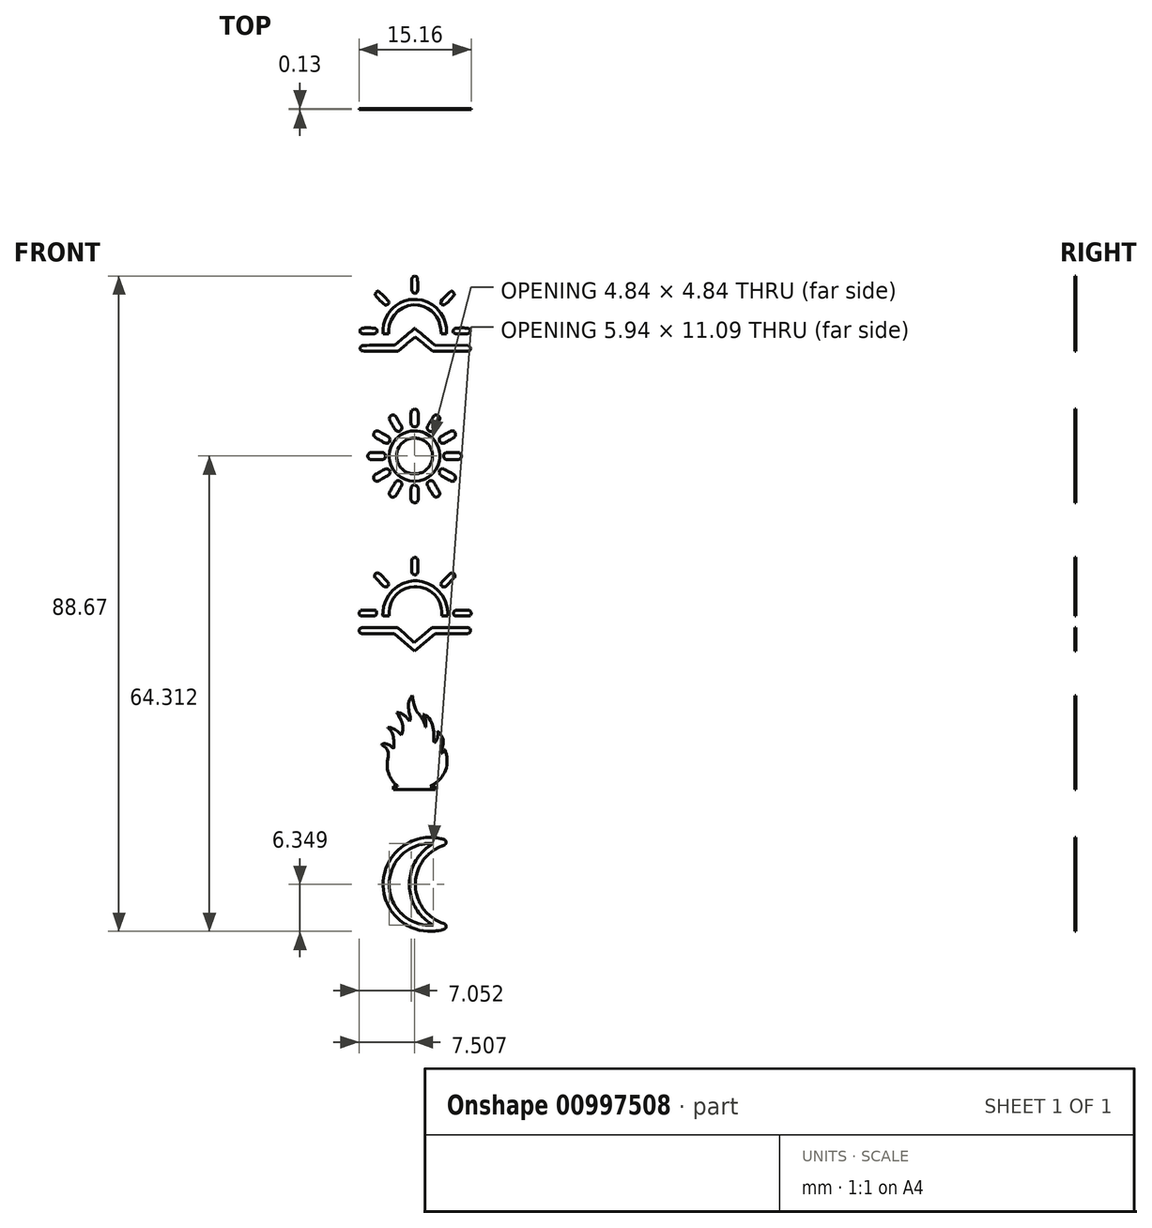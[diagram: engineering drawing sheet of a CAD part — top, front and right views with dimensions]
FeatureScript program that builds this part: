
annotation { "Feature Type Name" : "Feature", "Feature Type Description" : "" }
export const myFeature = defineFeature(function(context is Context, id is Id, definition is map)
    precondition{}
    {
        {
            var Q0;
            Q0=qCreatedBy(makeId("Front.planeOp"),FACE);
            var sketch = newSketch(context, id + "F0", { "sketchPlane" : qUnion([Q0])});
            skLineSegment(sketch, "E0", {"start": v(10.8, 42.86) * mm, "end": v(-8.25, 61.91) * mm});
            skLineSegment(sketch, "E1", {"start": v(-8.26, 61.91) * mm, "end": v(-10.8, 61.91) * mm});
            skLineSegment(sketch, "E2", {"start": v(-10.8, 61.91) * mm, "end": v(-10.8, -61.91) * mm});
            skLineSegment(sketch, "E3", {"start": v(-8.26, -61.91) * mm, "end": v(-10.8, -61.91) * mm});
            skLineSegment(sketch, "E4", {"start": v(-8.26, -61.91) * mm, "end": v(10.8, -42.86) * mm});
            skLineSegment(sketch, "E5", {"start": v(10.8, 42.86) * mm, "end": v(10.8, -42.86) * mm});
            skSolve(sketch);
        }
        {
            var Q0;
            Q0=makeQuery(id+"F0.imprint","IMPRINT",FACE,{"disambiguationData":[TD([[makeQuery(id+"F0.imprint","IMPRINT",EDGE,{"derivedFrom":sQuery(id+"F0.wireOp",EDGE,"E0")}),1.0]])]});
            var sketch = newSketch(context, id + "F1", { "sketchPlane" : qUnion([Q0])});
            skLineSegment(sketch, "E6", {"start": v(4.23, 3.04) * mm, "end": v(5.34, 4.15) * mm});
            skLineSegment(sketch, "E7", {"start": v(5.34, 4.15) * mm, "end": v(5.36, 4.18) * mm});
            skLineSegment(sketch, "E8", {"start": v(5.36, 4.18) * mm, "end": v(5.43, 4.28) * mm});
            skLineSegment(sketch, "E9", {"start": v(5.43, 4.28) * mm, "end": v(5.46, 4.43) * mm});
            skLineSegment(sketch, "E10", {"start": v(5.46, 4.43) * mm, "end": v(5.43, 4.57) * mm});
            skLineSegment(sketch, "E11", {"start": v(5.43, 4.57) * mm, "end": v(5.36, 4.68) * mm});
            skLineSegment(sketch, "E12", {"start": v(5.36, 4.68) * mm, "end": v(5.34, 4.7) * mm});
            skLineSegment(sketch, "E13", {"start": v(5.34, 4.7) * mm, "end": v(5.3, 4.73) * mm});
            skLineSegment(sketch, "E14", {"start": v(5.3, 4.73) * mm, "end": v(5.2, 4.8) * mm});
            skLineSegment(sketch, "E15", {"start": v(5.2, 4.8) * mm, "end": v(5.06, 4.82) * mm});
            skLineSegment(sketch, "E16", {"start": v(5.06, 4.82) * mm, "end": v(4.91, 4.8) * mm});
            skLineSegment(sketch, "E17", {"start": v(4.91, 4.8) * mm, "end": v(4.8, 4.73) * mm});
            skLineSegment(sketch, "E18", {"start": v(4.8, 4.73) * mm, "end": v(4.78, 4.7) * mm});
            skLineSegment(sketch, "E19", {"start": v(4.78, 4.7) * mm, "end": v(3.67, 3.6) * mm});
            skLineSegment(sketch, "E20", {"start": v(3.67, 3.6) * mm, "end": v(3.64, 3.57) * mm});
            skLineSegment(sketch, "E21", {"start": v(3.64, 3.57) * mm, "end": v(3.58, 3.46) * mm});
            skLineSegment(sketch, "E22", {"start": v(3.58, 3.46) * mm, "end": v(3.55, 3.32) * mm});
            skLineSegment(sketch, "E23", {"start": v(3.55, 3.32) * mm, "end": v(3.58, 3.17) * mm});
            skLineSegment(sketch, "E24", {"start": v(3.58, 3.17) * mm, "end": v(3.64, 3.07) * mm});
            skLineSegment(sketch, "E25", {"start": v(3.64, 3.07) * mm, "end": v(3.67, 3.04) * mm});
            skLineSegment(sketch, "E26", {"start": v(3.67, 3.04) * mm, "end": v(3.7, 3) * mm});
            skLineSegment(sketch, "E27", {"start": v(3.7, 3) * mm, "end": v(3.81, 2.95) * mm});
            skLineSegment(sketch, "E28", {"start": v(3.81, 2.95) * mm, "end": v(3.98, 2.92) * mm});
            skLineSegment(sketch, "E29", {"start": v(3.98, 2.92) * mm, "end": v(4.13, 2.95) * mm});
            skLineSegment(sketch, "E30", {"start": v(4.13, 2.95) * mm, "end": v(4.21, 3.01) * mm});
            skLineSegment(sketch, "E31", {"start": v(4.21, 3.01) * mm, "end": v(4.23, 3.04) * mm});
            skLineSegment(sketch, "E32", {"start": v(0.02, 4.54) * mm, "end": v(0.06, 4.54) * mm});
            skLineSegment(sketch, "E33", {"start": v(0.06, 4.54) * mm, "end": v(0.18, 4.57) * mm});
            skLineSegment(sketch, "E34", {"start": v(0.18, 4.57) * mm, "end": v(0.31, 4.65) * mm});
            skLineSegment(sketch, "E35", {"start": v(0.31, 4.65) * mm, "end": v(0.4, 4.78) * mm});
            skLineSegment(sketch, "E36", {"start": v(0.4, 4.78) * mm, "end": v(0.42, 4.9) * mm});
            skLineSegment(sketch, "E37", {"start": v(0.42, 4.9) * mm, "end": v(0.42, 4.94) * mm});
            skLineSegment(sketch, "E38", {"start": v(0.42, 4.94) * mm, "end": v(0.42, 6.53) * mm});
            skLineSegment(sketch, "E39", {"start": v(0.42, 6.53) * mm, "end": v(0.42, 6.57) * mm});
            skLineSegment(sketch, "E40", {"start": v(0.42, 6.57) * mm, "end": v(0.4, 6.69) * mm});
            skLineSegment(sketch, "E41", {"start": v(0.4, 6.69) * mm, "end": v(0.31, 6.82) * mm});
            skLineSegment(sketch, "E42", {"start": v(0.31, 6.82) * mm, "end": v(0.19, 6.9) * mm});
            skLineSegment(sketch, "E43", {"start": v(0.19, 6.9) * mm, "end": v(0.06, 6.93) * mm});
            skLineSegment(sketch, "E44", {"start": v(0.06, 6.93) * mm, "end": v(0.02, 6.93) * mm});
            skLineSegment(sketch, "E45", {"start": v(0.02, 6.93) * mm, "end": v(0, 6.93) * mm});
            skLineSegment(sketch, "E46", {"start": v(0, 6.93) * mm, "end": v(-0.1, 6.9) * mm});
            skLineSegment(sketch, "E47", {"start": v(-0.1, 6.9) * mm, "end": v(-0.24, 6.82) * mm});
            skLineSegment(sketch, "E48", {"start": v(-0.24, 6.82) * mm, "end": v(-0.34, 6.7) * mm});
            skLineSegment(sketch, "E49", {"start": v(-0.34, 6.7) * mm, "end": v(-0.38, 6.57) * mm});
            skLineSegment(sketch, "E50", {"start": v(-0.38, 6.57) * mm, "end": v(-0.38, 6.53) * mm});
            skLineSegment(sketch, "E51", {"start": v(-0.38, 6.53) * mm, "end": v(-0.38, 4.94) * mm});
            skLineSegment(sketch, "E52", {"start": v(-0.38, 4.94) * mm, "end": v(-0.38, 4.9) * mm});
            skLineSegment(sketch, "E53", {"start": v(-0.38, 4.9) * mm, "end": v(-0.34, 4.78) * mm});
            skLineSegment(sketch, "E54", {"start": v(-0.34, 4.78) * mm, "end": v(-0.24, 4.65) * mm});
            skLineSegment(sketch, "E55", {"start": v(-0.24, 4.65) * mm, "end": v(-0.1, 4.57) * mm});
            skLineSegment(sketch, "E56", {"start": v(-0.1, 4.57) * mm, "end": v(-0.01, 4.54) * mm});
            skLineSegment(sketch, "E57", {"start": v(-0.01, 4.54) * mm, "end": v(0.02, 4.54) * mm});
            skLineSegment(sketch, "E58", {"start": v(5.26, -0.61) * mm, "end": v(5.26, -0.65) * mm});
            skLineSegment(sketch, "E59", {"start": v(5.26, -0.65) * mm, "end": v(5.29, -0.78) * mm});
            skLineSegment(sketch, "E60", {"start": v(5.29, -0.78) * mm, "end": v(5.37, -0.9) * mm});
            skLineSegment(sketch, "E61", {"start": v(5.37, -0.9) * mm, "end": v(5.5, -0.98) * mm});
            skLineSegment(sketch, "E62", {"start": v(5.5, -0.98) * mm, "end": v(5.62, -1.01) * mm});
            skLineSegment(sketch, "E63", {"start": v(5.62, -1.01) * mm, "end": v(5.66, -1.01) * mm});
            skLineSegment(sketch, "E64", {"start": v(5.66, -1.01) * mm, "end": v(7.24, -1.01) * mm});
            skLineSegment(sketch, "E65", {"start": v(7.24, -1.01) * mm, "end": v(7.28, -1.01) * mm});
            skLineSegment(sketch, "E66", {"start": v(7.28, -1.01) * mm, "end": v(7.4, -0.98) * mm});
            skLineSegment(sketch, "E67", {"start": v(7.4, -0.98) * mm, "end": v(7.53, -0.9) * mm});
            skLineSegment(sketch, "E68", {"start": v(7.53, -0.9) * mm, "end": v(7.61, -0.78) * mm});
            skLineSegment(sketch, "E69", {"start": v(7.61, -0.78) * mm, "end": v(7.64, -0.65) * mm});
            skLineSegment(sketch, "E70", {"start": v(7.64, -0.65) * mm, "end": v(7.64, -0.61) * mm});
            skLineSegment(sketch, "E71", {"start": v(7.64, -0.61) * mm, "end": v(7.64, -0.57) * mm});
            skLineSegment(sketch, "E72", {"start": v(7.64, -0.57) * mm, "end": v(7.61, -0.45) * mm});
            skLineSegment(sketch, "E73", {"start": v(7.61, -0.45) * mm, "end": v(7.53, -0.32) * mm});
            skLineSegment(sketch, "E74", {"start": v(7.53, -0.32) * mm, "end": v(7.4, -0.24) * mm});
            skLineSegment(sketch, "E75", {"start": v(7.4, -0.24) * mm, "end": v(7.28, -0.21) * mm});
            skLineSegment(sketch, "E76", {"start": v(7.28, -0.21) * mm, "end": v(7.24, -0.21) * mm});
            skLineSegment(sketch, "E77", {"start": v(7.24, -0.21) * mm, "end": v(5.66, -0.21) * mm});
            skLineSegment(sketch, "E78", {"start": v(5.66, -0.21) * mm, "end": v(5.62, -0.21) * mm});
            skLineSegment(sketch, "E79", {"start": v(5.62, -0.21) * mm, "end": v(5.5, -0.25) * mm});
            skLineSegment(sketch, "E80", {"start": v(5.5, -0.25) * mm, "end": v(5.37, -0.35) * mm});
            skLineSegment(sketch, "E81", {"start": v(5.37, -0.35) * mm, "end": v(5.29, -0.48) * mm});
            skLineSegment(sketch, "E82", {"start": v(5.29, -0.48) * mm, "end": v(5.26, -0.58) * mm});
            skLineSegment(sketch, "E83", {"start": v(5.26, -0.58) * mm, "end": v(5.26, -0.61) * mm});
            skLineSegment(sketch, "E84", {"start": v(-4.18, 3.04) * mm, "end": v(-4.16, 3.01) * mm});
            skLineSegment(sketch, "E85", {"start": v(-4.16, 3.01) * mm, "end": v(-4.05, 2.95) * mm});
            skLineSegment(sketch, "E86", {"start": v(-4.05, 2.95) * mm, "end": v(-3.9, 2.92) * mm});
            skLineSegment(sketch, "E87", {"start": v(-3.9, 2.92) * mm, "end": v(-3.76, 2.95) * mm});
            skLineSegment(sketch, "E88", {"start": v(-3.76, 2.95) * mm, "end": v(-3.66, 3.01) * mm});
            skLineSegment(sketch, "E89", {"start": v(-3.66, 3.01) * mm, "end": v(-3.63, 3.04) * mm});
            skLineSegment(sketch, "E90", {"start": v(-3.63, 3.04) * mm, "end": v(-3.6, 3.07) * mm});
            skLineSegment(sketch, "E91", {"start": v(-3.6, 3.07) * mm, "end": v(-3.54, 3.17) * mm});
            skLineSegment(sketch, "E92", {"start": v(-3.54, 3.17) * mm, "end": v(-3.51, 3.32) * mm});
            skLineSegment(sketch, "E93", {"start": v(-3.51, 3.32) * mm, "end": v(-3.54, 3.46) * mm});
            skLineSegment(sketch, "E94", {"start": v(-3.54, 3.46) * mm, "end": v(-3.6, 3.57) * mm});
            skLineSegment(sketch, "E95", {"start": v(-3.6, 3.57) * mm, "end": v(-3.63, 3.6) * mm});
            skLineSegment(sketch, "E96", {"start": v(-3.63, 3.6) * mm, "end": v(-4.74, 4.7) * mm});
            skLineSegment(sketch, "E97", {"start": v(-4.74, 4.7) * mm, "end": v(-4.77, 4.73) * mm});
            skLineSegment(sketch, "E98", {"start": v(-4.77, 4.73) * mm, "end": v(-4.87, 4.8) * mm});
            skLineSegment(sketch, "E99", {"start": v(-4.87, 4.8) * mm, "end": v(-5.02, 4.82) * mm});
            skLineSegment(sketch, "E100", {"start": v(-5.02, 4.82) * mm, "end": v(-5.17, 4.8) * mm});
            skLineSegment(sketch, "E101", {"start": v(-5.17, 4.8) * mm, "end": v(-5.27, 4.73) * mm});
            skLineSegment(sketch, "E102", {"start": v(-5.27, 4.73) * mm, "end": v(-5.3, 4.7) * mm});
            skLineSegment(sketch, "E103", {"start": v(-5.3, 4.7) * mm, "end": v(-5.32, 4.68) * mm});
            skLineSegment(sketch, "E104", {"start": v(-5.32, 4.68) * mm, "end": v(-5.39, 4.57) * mm});
            skLineSegment(sketch, "E105", {"start": v(-5.39, 4.57) * mm, "end": v(-5.41, 4.43) * mm});
            skLineSegment(sketch, "E106", {"start": v(-5.41, 4.43) * mm, "end": v(-5.39, 4.28) * mm});
            skLineSegment(sketch, "E107", {"start": v(-5.39, 4.28) * mm, "end": v(-5.32, 4.18) * mm});
            skLineSegment(sketch, "E108", {"start": v(-5.32, 4.18) * mm, "end": v(-5.3, 4.15) * mm});
            skLineSegment(sketch, "E109", {"start": v(-5.3, 4.15) * mm, "end": v(-4.18, 3.04) * mm});
            skLineSegment(sketch, "E110", {"start": v(-7.12, -1) * mm, "end": v(-5.54, -1) * mm});
            skLineSegment(sketch, "E111", {"start": v(-5.54, -1) * mm, "end": v(-5.5, -1) * mm});
            skLineSegment(sketch, "E112", {"start": v(-5.5, -1) * mm, "end": v(-5.38, -0.98) * mm});
            skLineSegment(sketch, "E113", {"start": v(-5.38, -0.98) * mm, "end": v(-5.25, -0.9) * mm});
            skLineSegment(sketch, "E114", {"start": v(-5.25, -0.9) * mm, "end": v(-5.17, -0.77) * mm});
            skLineSegment(sketch, "E115", {"start": v(-5.17, -0.77) * mm, "end": v(-5.14, -0.65) * mm});
            skLineSegment(sketch, "E116", {"start": v(-5.14, -0.65) * mm, "end": v(-5.14, -0.6) * mm});
            skLineSegment(sketch, "E117", {"start": v(-5.14, -0.6) * mm, "end": v(-5.14, -0.57) * mm});
            skLineSegment(sketch, "E118", {"start": v(-5.14, -0.57) * mm, "end": v(-5.17, -0.45) * mm});
            skLineSegment(sketch, "E119", {"start": v(-5.17, -0.45) * mm, "end": v(-5.25, -0.32) * mm});
            skLineSegment(sketch, "E120", {"start": v(-5.25, -0.32) * mm, "end": v(-5.37, -0.24) * mm});
            skLineSegment(sketch, "E121", {"start": v(-5.37, -0.24) * mm, "end": v(-5.5, -0.21) * mm});
            skLineSegment(sketch, "E122", {"start": v(-5.5, -0.21) * mm, "end": v(-5.54, -0.21) * mm});
            skLineSegment(sketch, "E123", {"start": v(-5.54, -0.21) * mm, "end": v(-7.12, -0.21) * mm});
            skLineSegment(sketch, "E124", {"start": v(-7.12, -0.21) * mm, "end": v(-7.16, -0.21) * mm});
            skLineSegment(sketch, "E125", {"start": v(-7.16, -0.21) * mm, "end": v(-7.28, -0.25) * mm});
            skLineSegment(sketch, "E126", {"start": v(-7.28, -0.25) * mm, "end": v(-7.41, -0.35) * mm});
            skLineSegment(sketch, "E127", {"start": v(-7.41, -0.35) * mm, "end": v(-7.5, -0.48) * mm});
            skLineSegment(sketch, "E128", {"start": v(-7.5, -0.48) * mm, "end": v(-7.52, -0.58) * mm});
            skLineSegment(sketch, "E129", {"start": v(-7.52, -0.58) * mm, "end": v(-7.52, -0.6) * mm});
            skLineSegment(sketch, "E130", {"start": v(-7.52, -0.6) * mm, "end": v(-7.52, -0.65) * mm});
            skLineSegment(sketch, "E131", {"start": v(-7.52, -0.65) * mm, "end": v(-7.49, -0.77) * mm});
            skLineSegment(sketch, "E132", {"start": v(-7.49, -0.77) * mm, "end": v(-7.4, -0.9) * mm});
            skLineSegment(sketch, "E133", {"start": v(-7.4, -0.9) * mm, "end": v(-7.28, -0.98) * mm});
            skLineSegment(sketch, "E134", {"start": v(-7.28, -0.98) * mm, "end": v(-7.16, -1) * mm});
            skLineSegment(sketch, "E135", {"start": v(-7.16, -1) * mm, "end": v(-7.12, -1) * mm});
            skLineSegment(sketch, "E136", {"start": v(7.16, -2.6) * mm, "end": v(2.32, -2.6) * mm});
            skLineSegment(sketch, "E137", {"start": v(2.32, -2.6) * mm, "end": v(1.37, -3.39) * mm});
            skLineSegment(sketch, "E138", {"start": v(1.37, -3.39) * mm, "end": v(-0.06, -4.58) * mm});
            skLineSegment(sketch, "E139", {"start": v(-0.06, -4.58) * mm, "end": v(-1.33, -3.39) * mm});
            skLineSegment(sketch, "E140", {"start": v(-1.33, -3.39) * mm, "end": v(-2.28, -2.6) * mm});
            skLineSegment(sketch, "E141", {"start": v(-2.28, -2.6) * mm, "end": v(-7.12, -2.6) * mm});
            skLineSegment(sketch, "E142", {"start": v(-7.12, -2.6) * mm, "end": v(-7.15, -2.6) * mm});
            skLineSegment(sketch, "E143", {"start": v(-7.15, -2.6) * mm, "end": v(-7.25, -2.62) * mm});
            skLineSegment(sketch, "E144", {"start": v(-7.25, -2.62) * mm, "end": v(-7.38, -2.7) * mm});
            skLineSegment(sketch, "E145", {"start": v(-7.38, -2.7) * mm, "end": v(-7.48, -2.83) * mm});
            skLineSegment(sketch, "E146", {"start": v(-7.48, -2.83) * mm, "end": v(-7.52, -2.95) * mm});
            skLineSegment(sketch, "E147", {"start": v(-7.52, -2.95) * mm, "end": v(-7.52, -3) * mm});
            skLineSegment(sketch, "E148", {"start": v(-7.52, -3) * mm, "end": v(-7.52, -3.04) * mm});
            skLineSegment(sketch, "E149", {"start": v(-7.52, -3.04) * mm, "end": v(-7.48, -3.16) * mm});
            skLineSegment(sketch, "E150", {"start": v(-7.48, -3.16) * mm, "end": v(-7.38, -3.28) * mm});
            skLineSegment(sketch, "E151", {"start": v(-7.38, -3.28) * mm, "end": v(-7.25, -3.36) * mm});
            skLineSegment(sketch, "E152", {"start": v(-7.25, -3.36) * mm, "end": v(-7.15, -3.4) * mm});
            skLineSegment(sketch, "E153", {"start": v(-7.15, -3.4) * mm, "end": v(-7.12, -3.4) * mm});
            skLineSegment(sketch, "E154", {"start": v(-7.12, -3.4) * mm, "end": v(-2.76, -3.4) * mm});
            skLineSegment(sketch, "E155", {"start": v(-2.76, -3.4) * mm, "end": v(0.02, -5.77) * mm});
            skLineSegment(sketch, "E156", {"start": v(0.02, -5.77) * mm, "end": v(2.8, -3.4) * mm});
            skLineSegment(sketch, "E157", {"start": v(2.8, -3.4) * mm, "end": v(7.16, -3.4) * mm});
            skLineSegment(sketch, "E158", {"start": v(7.16, -3.4) * mm, "end": v(7.2, -3.4) * mm});
            skLineSegment(sketch, "E159", {"start": v(7.2, -3.4) * mm, "end": v(7.32, -3.36) * mm});
            skLineSegment(sketch, "E160", {"start": v(7.32, -3.36) * mm, "end": v(7.45, -3.28) * mm});
            skLineSegment(sketch, "E161", {"start": v(7.45, -3.28) * mm, "end": v(7.53, -3.16) * mm});
            skLineSegment(sketch, "E162", {"start": v(7.53, -3.16) * mm, "end": v(7.56, -3.04) * mm});
            skLineSegment(sketch, "E163", {"start": v(7.56, -3.04) * mm, "end": v(7.56, -3) * mm});
            skLineSegment(sketch, "E164", {"start": v(7.56, -3) * mm, "end": v(7.56, -2.95) * mm});
            skLineSegment(sketch, "E165", {"start": v(7.56, -2.95) * mm, "end": v(7.53, -2.83) * mm});
            skLineSegment(sketch, "E166", {"start": v(7.53, -2.83) * mm, "end": v(7.45, -2.7) * mm});
            skLineSegment(sketch, "E167", {"start": v(7.45, -2.7) * mm, "end": v(7.32, -2.62) * mm});
            skLineSegment(sketch, "E168", {"start": v(7.32, -2.62) * mm, "end": v(7.2, -2.6) * mm});
            skLineSegment(sketch, "E169", {"start": v(7.2, -2.6) * mm, "end": v(7.16, -2.6) * mm});
            skLineSegment(sketch, "E170", {"start": v(-4.26, -1) * mm, "end": v(-3.47, -1) * mm});
            skLineSegment(sketch, "E171", {"start": v(-3.47, -1) * mm, "end": v(-3.47, -0.96) * mm});
            skLineSegment(sketch, "E172", {"start": v(-3.47, -0.96) * mm, "end": v(-3.47, -0.8) * mm});
            skLineSegment(sketch, "E173", {"start": v(-3.47, -0.8) * mm, "end": v(-3.47, -0.66) * mm});
            skLineSegment(sketch, "E174", {"start": v(-3.47, -0.66) * mm, "end": v(-3.47, -0.6) * mm});
            skLineSegment(sketch, "E175", {"start": v(-3.47, -0.6) * mm, "end": v(-3.47, -0.43) * mm});
            skLineSegment(sketch, "E176", {"start": v(-3.47, -0.43) * mm, "end": v(-3.4, 0.11) * mm});
            skLineSegment(sketch, "E177", {"start": v(-3.4, 0.11) * mm, "end": v(-3.2, 0.79) * mm});
            skLineSegment(sketch, "E178", {"start": v(-3.2, 0.79) * mm, "end": v(-2.86, 1.4) * mm});
            skLineSegment(sketch, "E179", {"start": v(-2.86, 1.4) * mm, "end": v(-2.43, 1.92) * mm});
            skLineSegment(sketch, "E180", {"start": v(-2.43, 1.92) * mm, "end": v(-1.9, 2.36) * mm});
            skLineSegment(sketch, "E181", {"start": v(-1.9, 2.36) * mm, "end": v(-1.3, 2.68) * mm});
            skLineSegment(sketch, "E182", {"start": v(-1.3, 2.68) * mm, "end": v(-0.62, 2.9) * mm});
            skLineSegment(sketch, "E183", {"start": v(-0.62, 2.9) * mm, "end": v(-0.08, 2.96) * mm});
            skLineSegment(sketch, "E184", {"start": v(-0.08, 2.96) * mm, "end": v(0.1, 2.96) * mm});
            skLineSegment(sketch, "E185", {"start": v(0.1, 2.96) * mm, "end": v(0.28, 2.96) * mm});
            skLineSegment(sketch, "E186", {"start": v(0.28, 2.96) * mm, "end": v(0.82, 2.9) * mm});
            skLineSegment(sketch, "E187", {"start": v(0.82, 2.9) * mm, "end": v(1.5, 2.68) * mm});
            skLineSegment(sketch, "E188", {"start": v(1.5, 2.68) * mm, "end": v(2.1, 2.36) * mm});
            skLineSegment(sketch, "E189", {"start": v(2.1, 2.36) * mm, "end": v(2.63, 1.92) * mm});
            skLineSegment(sketch, "E190", {"start": v(2.63, 1.92) * mm, "end": v(3.07, 1.4) * mm});
            skLineSegment(sketch, "E191", {"start": v(3.07, 1.4) * mm, "end": v(3.4, 0.79) * mm});
            skLineSegment(sketch, "E192", {"start": v(3.4, 0.79) * mm, "end": v(3.6, 0.12) * mm});
            skLineSegment(sketch, "E193", {"start": v(3.6, 0.12) * mm, "end": v(3.67, -0.43) * mm});
            skLineSegment(sketch, "E194", {"start": v(3.67, -0.43) * mm, "end": v(3.67, -0.6) * mm});
            skLineSegment(sketch, "E195", {"start": v(3.67, -0.6) * mm, "end": v(3.67, -0.66) * mm});
            skLineSegment(sketch, "E196", {"start": v(3.67, -0.66) * mm, "end": v(3.67, -0.8) * mm});
            skLineSegment(sketch, "E197", {"start": v(3.67, -0.8) * mm, "end": v(3.67, -0.96) * mm});
            skLineSegment(sketch, "E198", {"start": v(3.67, -0.96) * mm, "end": v(3.67, -1) * mm});
            skLineSegment(sketch, "E199", {"start": v(3.67, -1) * mm, "end": v(4.47, -1) * mm});
            skLineSegment(sketch, "E200", {"start": v(4.47, -1) * mm, "end": v(4.47, -0.96) * mm});
            skLineSegment(sketch, "E201", {"start": v(4.47, -0.96) * mm, "end": v(4.47, -0.8) * mm});
            skLineSegment(sketch, "E202", {"start": v(4.47, -0.8) * mm, "end": v(4.47, -0.66) * mm});
            skLineSegment(sketch, "E203", {"start": v(4.47, -0.66) * mm, "end": v(4.47, -0.6) * mm});
            skLineSegment(sketch, "E204", {"start": v(4.47, -0.6) * mm, "end": v(4.47, -0.4) * mm});
            skLineSegment(sketch, "E205", {"start": v(4.47, -0.4) * mm, "end": v(4.38, 0.26) * mm});
            skLineSegment(sketch, "E206", {"start": v(4.38, 0.26) * mm, "end": v(4.12, 1.08) * mm});
            skLineSegment(sketch, "E207", {"start": v(4.12, 1.08) * mm, "end": v(3.71, 1.82) * mm});
            skLineSegment(sketch, "E208", {"start": v(3.71, 1.82) * mm, "end": v(3.18, 2.47) * mm});
            skLineSegment(sketch, "E209", {"start": v(3.18, 2.47) * mm, "end": v(2.53, 3) * mm});
            skLineSegment(sketch, "E210", {"start": v(2.53, 3) * mm, "end": v(1.79, 3.4) * mm});
            skLineSegment(sketch, "E211", {"start": v(1.79, 3.4) * mm, "end": v(0.97, 3.67) * mm});
            skLineSegment(sketch, "E212", {"start": v(0.97, 3.67) * mm, "end": v(0.32, 3.76) * mm});
            skLineSegment(sketch, "E213", {"start": v(0.32, 3.76) * mm, "end": v(0.1, 3.76) * mm});
            skLineSegment(sketch, "E214", {"start": v(0.1, 3.76) * mm, "end": v(-0.12, 3.76) * mm});
            skLineSegment(sketch, "E215", {"start": v(-0.12, 3.76) * mm, "end": v(-0.77, 3.67) * mm});
            skLineSegment(sketch, "E216", {"start": v(-0.77, 3.67) * mm, "end": v(-1.59, 3.4) * mm});
            skLineSegment(sketch, "E217", {"start": v(-1.59, 3.4) * mm, "end": v(-2.33, 3) * mm});
            skLineSegment(sketch, "E218", {"start": v(-2.33, 3) * mm, "end": v(-2.97, 2.47) * mm});
            skLineSegment(sketch, "E219", {"start": v(-2.97, 2.47) * mm, "end": v(-3.51, 1.82) * mm});
            skLineSegment(sketch, "E220", {"start": v(-3.51, 1.82) * mm, "end": v(-3.92, 1.08) * mm});
            skLineSegment(sketch, "E221", {"start": v(-3.92, 1.08) * mm, "end": v(-4.17, 0.26) * mm});
            skLineSegment(sketch, "E222", {"start": v(-4.17, 0.26) * mm, "end": v(-4.26, -0.4) * mm});
            skLineSegment(sketch, "E223", {"start": v(-4.26, -0.4) * mm, "end": v(-4.26, -0.6) * mm});
            skLineSegment(sketch, "E224", {"start": v(-4.26, -0.6) * mm, "end": v(-4.28, -0.63) * mm});
            skLineSegment(sketch, "E225", {"start": v(-4.28, -0.63) * mm, "end": v(-4.3, -0.72) * mm});
            skLineSegment(sketch, "E226", {"start": v(-4.3, -0.72) * mm, "end": v(-4.32, -0.8) * mm});
            skLineSegment(sketch, "E227", {"start": v(-4.32, -0.8) * mm, "end": v(-4.3, -0.9) * mm});
            skLineSegment(sketch, "E228", {"start": v(-4.3, -0.9) * mm, "end": v(-4.28, -0.98) * mm});
            skLineSegment(sketch, "E229", {"start": v(-4.28, -0.98) * mm, "end": v(-4.26, -1) * mm});
            skSolve(sketch);
        }
        {
            var Q0;
            Q0=makeQuery(id+"F0.imprint","IMPRINT",FACE,{"disambiguationData":[TD([[makeQuery(id+"F0.imprint","IMPRINT",EDGE,{"derivedFrom":sQuery(id+"F0.wireOp",EDGE,"E0")}),1.0]])]});
            var sketch = newSketch(context, id + "F2", { "sketchPlane" : qUnion([Q0])});
            skLineSegment(sketch, "E230", {"start": v(-0.25, 44.87) * mm, "end": v(-0.26, 44.86) * mm});
            skLineSegment(sketch, "E231", {"start": v(-0.26, 44.86) * mm, "end": v(-0.29, 44.83) * mm});
            skLineSegment(sketch, "E232", {"start": v(-0.29, 44.83) * mm, "end": v(-0.32, 44.77) * mm});
            skLineSegment(sketch, "E233", {"start": v(-0.32, 44.77) * mm, "end": v(-0.34, 44.7) * mm});
            skLineSegment(sketch, "E234", {"start": v(-0.34, 44.7) * mm, "end": v(-0.36, 44.61) * mm});
            skLineSegment(sketch, "E235", {"start": v(-0.36, 44.61) * mm, "end": v(-0.37, 44.49) * mm});
            skLineSegment(sketch, "E236", {"start": v(-0.37, 44.49) * mm, "end": v(-0.38, 44.32) * mm});
            skLineSegment(sketch, "E237", {"start": v(-0.38, 44.32) * mm, "end": v(-0.38, 44.1) * mm});
            skLineSegment(sketch, "E238", {"start": v(-0.38, 44.1) * mm, "end": v(-0.38, 43.9) * mm});
            skLineSegment(sketch, "E239", {"start": v(-0.38, 43.9) * mm, "end": v(-0.38, 43.83) * mm});
            skLineSegment(sketch, "E240", {"start": v(-0.38, 43.83) * mm, "end": v(-0.38, 43.77) * mm});
            skLineSegment(sketch, "E241", {"start": v(-0.38, 43.77) * mm, "end": v(-0.38, 43.56) * mm});
            skLineSegment(sketch, "E242", {"start": v(-0.38, 43.56) * mm, "end": v(-0.38, 43.34) * mm});
            skLineSegment(sketch, "E243", {"start": v(-0.38, 43.34) * mm, "end": v(-0.37, 43.18) * mm});
            skLineSegment(sketch, "E244", {"start": v(-0.37, 43.18) * mm, "end": v(-0.36, 43.05) * mm});
            skLineSegment(sketch, "E245", {"start": v(-0.36, 43.05) * mm, "end": v(-0.34, 42.96) * mm});
            skLineSegment(sketch, "E246", {"start": v(-0.34, 42.96) * mm, "end": v(-0.32, 42.9) * mm});
            skLineSegment(sketch, "E247", {"start": v(-0.32, 42.9) * mm, "end": v(-0.29, 42.84) * mm});
            skLineSegment(sketch, "E248", {"start": v(-0.29, 42.84) * mm, "end": v(-0.26, 42.8) * mm});
            skLineSegment(sketch, "E249", {"start": v(-0.26, 42.8) * mm, "end": v(-0.25, 42.8) * mm});
            skLineSegment(sketch, "E250", {"start": v(-0.25, 42.8) * mm, "end": v(-0.22, 42.76) * mm});
            skLineSegment(sketch, "E251", {"start": v(-0.22, 42.76) * mm, "end": v(-0.1, 42.7) * mm});
            skLineSegment(sketch, "E252", {"start": v(-0.1, 42.7) * mm, "end": v(0.06, 42.66) * mm});
            skLineSegment(sketch, "E253", {"start": v(0.06, 42.66) * mm, "end": v(0.2, 42.7) * mm});
            skLineSegment(sketch, "E254", {"start": v(0.2, 42.7) * mm, "end": v(0.3, 42.79) * mm});
            skLineSegment(sketch, "E255", {"start": v(0.3, 42.79) * mm, "end": v(0.33, 42.82) * mm});
            skLineSegment(sketch, "E256", {"start": v(0.33, 42.82) * mm, "end": v(0.35, 42.85) * mm});
            skLineSegment(sketch, "E257", {"start": v(0.35, 42.85) * mm, "end": v(0.38, 42.94) * mm});
            skLineSegment(sketch, "E258", {"start": v(0.38, 42.94) * mm, "end": v(0.4, 43.13) * mm});
            skLineSegment(sketch, "E259", {"start": v(0.4, 43.13) * mm, "end": v(0.42, 43.44) * mm});
            skLineSegment(sketch, "E260", {"start": v(0.42, 43.44) * mm, "end": v(0.41, 43.78) * mm});
            skLineSegment(sketch, "E261", {"start": v(0.41, 43.78) * mm, "end": v(0.4, 43.9) * mm});
            skLineSegment(sketch, "E262", {"start": v(0.4, 43.9) * mm, "end": v(0.4, 43.97) * mm});
            skLineSegment(sketch, "E263", {"start": v(0.4, 43.97) * mm, "end": v(0.4, 44.18) * mm});
            skLineSegment(sketch, "E264", {"start": v(0.4, 44.18) * mm, "end": v(0.4, 44.4) * mm});
            skLineSegment(sketch, "E265", {"start": v(0.4, 44.4) * mm, "end": v(0.38, 44.56) * mm});
            skLineSegment(sketch, "E266", {"start": v(0.38, 44.56) * mm, "end": v(0.37, 44.68) * mm});
            skLineSegment(sketch, "E267", {"start": v(0.37, 44.68) * mm, "end": v(0.35, 44.77) * mm});
            skLineSegment(sketch, "E268", {"start": v(0.35, 44.77) * mm, "end": v(0.33, 44.83) * mm});
            skLineSegment(sketch, "E269", {"start": v(0.33, 44.83) * mm, "end": v(0.3, 44.88) * mm});
            skLineSegment(sketch, "E270", {"start": v(0.3, 44.88) * mm, "end": v(0.27, 44.9) * mm});
            skLineSegment(sketch, "E271", {"start": v(0.27, 44.9) * mm, "end": v(0.26, 44.91) * mm});
            skLineSegment(sketch, "E272", {"start": v(0.26, 44.91) * mm, "end": v(0.22, 44.94) * mm});
            skLineSegment(sketch, "E273", {"start": v(0.22, 44.94) * mm, "end": v(0, 45) * mm});
            skLineSegment(sketch, "E274", {"start": v(0, 45) * mm, "end": v(-0.2, 44.91) * mm});
            skLineSegment(sketch, "E275", {"start": v(-0.2, 44.91) * mm, "end": v(-0.25, 44.87) * mm});
            skLineSegment(sketch, "E276", {"start": v(-5.2, 42.8) * mm, "end": v(-5.22, 42.78) * mm});
            skLineSegment(sketch, "E277", {"start": v(-5.22, 42.78) * mm, "end": v(-5.3, 42.66) * mm});
            skLineSegment(sketch, "E278", {"start": v(-5.3, 42.66) * mm, "end": v(-5.34, 42.55) * mm});
            skLineSegment(sketch, "E279", {"start": v(-5.34, 42.55) * mm, "end": v(-5.34, 42.51) * mm});
            skLineSegment(sketch, "E280", {"start": v(-5.34, 42.51) * mm, "end": v(-5.34, 42.48) * mm});
            skLineSegment(sketch, "E281", {"start": v(-5.34, 42.48) * mm, "end": v(-5.28, 42.4) * mm});
            skLineSegment(sketch, "E282", {"start": v(-5.28, 42.4) * mm, "end": v(-5.14, 42.2) * mm});
            skLineSegment(sketch, "E283", {"start": v(-5.14, 42.2) * mm, "end": v(-4.93, 41.96) * mm});
            skLineSegment(sketch, "E284", {"start": v(-4.93, 41.96) * mm, "end": v(-4.68, 41.7) * mm});
            skLineSegment(sketch, "E285", {"start": v(-4.68, 41.7) * mm, "end": v(-4.43, 41.46) * mm});
            skLineSegment(sketch, "E286", {"start": v(-4.43, 41.46) * mm, "end": v(-4.2, 41.25) * mm});
            skLineSegment(sketch, "E287", {"start": v(-4.2, 41.25) * mm, "end": v(-4, 41.1) * mm});
            skLineSegment(sketch, "E288", {"start": v(-4, 41.1) * mm, "end": v(-3.9, 41.05) * mm});
            skLineSegment(sketch, "E289", {"start": v(-3.9, 41.05) * mm, "end": v(-3.88, 41.05) * mm});
            skLineSegment(sketch, "E290", {"start": v(-3.88, 41.05) * mm, "end": v(-3.84, 41.05) * mm});
            skLineSegment(sketch, "E291", {"start": v(-3.84, 41.05) * mm, "end": v(-3.74, 41.1) * mm});
            skLineSegment(sketch, "E292", {"start": v(-3.74, 41.1) * mm, "end": v(-3.6, 41.18) * mm});
            skLineSegment(sketch, "E293", {"start": v(-3.6, 41.18) * mm, "end": v(-3.5, 41.3) * mm});
            skLineSegment(sketch, "E294", {"start": v(-3.5, 41.3) * mm, "end": v(-3.46, 41.4) * mm});
            skLineSegment(sketch, "E295", {"start": v(-3.46, 41.4) * mm, "end": v(-3.46, 41.43) * mm});
            skLineSegment(sketch, "E296", {"start": v(-3.46, 41.43) * mm, "end": v(-3.46, 41.46) * mm});
            skLineSegment(sketch, "E297", {"start": v(-3.46, 41.46) * mm, "end": v(-3.52, 41.54) * mm});
            skLineSegment(sketch, "E298", {"start": v(-3.52, 41.54) * mm, "end": v(-3.67, 41.73) * mm});
            skLineSegment(sketch, "E299", {"start": v(-3.67, 41.73) * mm, "end": v(-3.9, 41.97) * mm});
            skLineSegment(sketch, "E300", {"start": v(-3.9, 41.97) * mm, "end": v(-4.15, 42.24) * mm});
            skLineSegment(sketch, "E301", {"start": v(-4.15, 42.24) * mm, "end": v(-4.41, 42.5) * mm});
            skLineSegment(sketch, "E302", {"start": v(-4.41, 42.5) * mm, "end": v(-4.65, 42.72) * mm});
            skLineSegment(sketch, "E303", {"start": v(-4.65, 42.72) * mm, "end": v(-4.84, 42.87) * mm});
            skLineSegment(sketch, "E304", {"start": v(-4.84, 42.87) * mm, "end": v(-4.92, 42.93) * mm});
            skLineSegment(sketch, "E305", {"start": v(-4.92, 42.93) * mm, "end": v(-4.95, 42.93) * mm});
            skLineSegment(sketch, "E306", {"start": v(-4.95, 42.93) * mm, "end": v(-4.98, 42.93) * mm});
            skLineSegment(sketch, "E307", {"start": v(-4.98, 42.93) * mm, "end": v(-5.07, 42.9) * mm});
            skLineSegment(sketch, "E308", {"start": v(-5.07, 42.9) * mm, "end": v(-5.19, 42.81) * mm});
            skLineSegment(sketch, "E309", {"start": v(-5.19, 42.81) * mm, "end": v(-5.2, 42.8) * mm});
            skLineSegment(sketch, "E310", {"start": v(4.18, 42.25) * mm, "end": v(4.07, 42.14) * mm});
            skLineSegment(sketch, "E311", {"start": v(4.07, 42.14) * mm, "end": v(3.75, 41.8) * mm});
            skLineSegment(sketch, "E312", {"start": v(3.75, 41.8) * mm, "end": v(3.54, 41.5) * mm});
            skLineSegment(sketch, "E313", {"start": v(3.54, 41.5) * mm, "end": v(3.52, 41.3) * mm});
            skLineSegment(sketch, "E314", {"start": v(3.52, 41.3) * mm, "end": v(3.63, 41.18) * mm});
            skLineSegment(sketch, "E315", {"start": v(3.63, 41.18) * mm, "end": v(3.67, 41.15) * mm});
            skLineSegment(sketch, "E316", {"start": v(3.67, 41.15) * mm, "end": v(3.7, 41.13) * mm});
            skLineSegment(sketch, "E317", {"start": v(3.7, 41.13) * mm, "end": v(3.83, 41.08) * mm});
            skLineSegment(sketch, "E318", {"start": v(3.83, 41.08) * mm, "end": v(3.97, 41.07) * mm});
            skLineSegment(sketch, "E319", {"start": v(3.97, 41.07) * mm, "end": v(4, 41.08) * mm});
            skLineSegment(sketch, "E320", {"start": v(4, 41.08) * mm, "end": v(4.03, 41.09) * mm});
            skLineSegment(sketch, "E321", {"start": v(4.03, 41.09) * mm, "end": v(4.12, 41.15) * mm});
            skLineSegment(sketch, "E322", {"start": v(4.12, 41.15) * mm, "end": v(4.3, 41.3) * mm});
            skLineSegment(sketch, "E323", {"start": v(4.3, 41.3) * mm, "end": v(4.53, 41.51) * mm});
            skLineSegment(sketch, "E324", {"start": v(4.53, 41.51) * mm, "end": v(4.77, 41.75) * mm});
            skLineSegment(sketch, "E325", {"start": v(4.77, 41.75) * mm, "end": v(5, 42) * mm});
            skLineSegment(sketch, "E326", {"start": v(5, 42) * mm, "end": v(5.2, 42.22) * mm});
            skLineSegment(sketch, "E327", {"start": v(5.2, 42.22) * mm, "end": v(5.33, 42.4) * mm});
            skLineSegment(sketch, "E328", {"start": v(5.33, 42.4) * mm, "end": v(5.38, 42.49) * mm});
            skLineSegment(sketch, "E329", {"start": v(5.38, 42.49) * mm, "end": v(5.38, 42.51) * mm});
            skLineSegment(sketch, "E330", {"start": v(5.38, 42.51) * mm, "end": v(5.38, 42.55) * mm});
            skLineSegment(sketch, "E331", {"start": v(5.38, 42.55) * mm, "end": v(5.34, 42.65) * mm});
            skLineSegment(sketch, "E332", {"start": v(5.34, 42.65) * mm, "end": v(5.24, 42.78) * mm});
            skLineSegment(sketch, "E333", {"start": v(5.24, 42.78) * mm, "end": v(5.1, 42.89) * mm});
            skLineSegment(sketch, "E334", {"start": v(5.1, 42.89) * mm, "end": v(5, 42.93) * mm});
            skLineSegment(sketch, "E335", {"start": v(5, 42.93) * mm, "end": v(4.97, 42.93) * mm});
            skLineSegment(sketch, "E336", {"start": v(4.97, 42.93) * mm, "end": v(4.95, 42.93) * mm});
            skLineSegment(sketch, "E337", {"start": v(4.95, 42.93) * mm, "end": v(4.87, 42.88) * mm});
            skLineSegment(sketch, "E338", {"start": v(4.87, 42.88) * mm, "end": v(4.69, 42.73) * mm});
            skLineSegment(sketch, "E339", {"start": v(4.69, 42.73) * mm, "end": v(4.45, 42.52) * mm});
            skLineSegment(sketch, "E340", {"start": v(4.45, 42.52) * mm, "end": v(4.25, 42.32) * mm});
            skLineSegment(sketch, "E341", {"start": v(4.25, 42.32) * mm, "end": v(4.18, 42.25) * mm});
            skLineSegment(sketch, "E342", {"start": v(-0.75, 41.8) * mm, "end": v(-0.91, 41.76) * mm});
            skLineSegment(sketch, "E343", {"start": v(-0.91, 41.76) * mm, "end": v(-1.4, 41.6) * mm});
            skLineSegment(sketch, "E344", {"start": v(-1.4, 41.6) * mm, "end": v(-1.98, 41.34) * mm});
            skLineSegment(sketch, "E345", {"start": v(-1.98, 41.34) * mm, "end": v(-2.52, 41) * mm});
            skLineSegment(sketch, "E346", {"start": v(-2.52, 41) * mm, "end": v(-2.9, 40.66) * mm});
            skLineSegment(sketch, "E347", {"start": v(-2.9, 40.66) * mm, "end": v(-3.03, 40.54) * mm});
            skLineSegment(sketch, "E348", {"start": v(-3.03, 40.54) * mm, "end": v(-3.17, 40.4) * mm});
            skLineSegment(sketch, "E349", {"start": v(-3.17, 40.4) * mm, "end": v(-3.55, 39.9) * mm});
            skLineSegment(sketch, "E350", {"start": v(-3.55, 39.9) * mm, "end": v(-3.94, 39.19) * mm});
            skLineSegment(sketch, "E351", {"start": v(-3.94, 39.19) * mm, "end": v(-4.18, 38.41) * mm});
            skLineSegment(sketch, "E352", {"start": v(-4.18, 38.41) * mm, "end": v(-4.27, 37.82) * mm});
            skLineSegment(sketch, "E353", {"start": v(-4.27, 37.82) * mm, "end": v(-4.27, 37.62) * mm});
            skLineSegment(sketch, "E354", {"start": v(-4.27, 37.62) * mm, "end": v(-4.27, 37.17) * mm});
            skLineSegment(sketch, "E355", {"start": v(-4.27, 37.17) * mm, "end": v(-3.53, 37.17) * mm});
            skLineSegment(sketch, "E356", {"start": v(-3.53, 37.17) * mm, "end": v(-3.53, 37.5) * mm});
            skLineSegment(sketch, "E357", {"start": v(-3.53, 37.5) * mm, "end": v(-3.53, 37.7) * mm});
            skLineSegment(sketch, "E358", {"start": v(-3.53, 37.7) * mm, "end": v(-3.44, 38.3) * mm});
            skLineSegment(sketch, "E359", {"start": v(-3.44, 38.3) * mm, "end": v(-3.18, 39.05) * mm});
            skLineSegment(sketch, "E360", {"start": v(-3.18, 39.05) * mm, "end": v(-2.77, 39.7) * mm});
            skLineSegment(sketch, "E361", {"start": v(-2.77, 39.7) * mm, "end": v(-2.25, 40.26) * mm});
            skLineSegment(sketch, "E362", {"start": v(-2.25, 40.26) * mm, "end": v(-1.62, 40.68) * mm});
            skLineSegment(sketch, "E363", {"start": v(-1.62, 40.68) * mm, "end": v(-0.91, 40.97) * mm});
            skLineSegment(sketch, "E364", {"start": v(-0.91, 40.97) * mm, "end": v(-0.15, 41.09) * mm});
            skLineSegment(sketch, "E365", {"start": v(-0.15, 41.09) * mm, "end": v(0.45, 41.06) * mm});
            skLineSegment(sketch, "E366", {"start": v(0.45, 41.06) * mm, "end": v(0.64, 41.03) * mm});
            skLineSegment(sketch, "E367", {"start": v(0.64, 41.03) * mm, "end": v(0.8, 41) * mm});
            skLineSegment(sketch, "E368", {"start": v(0.8, 41) * mm, "end": v(1.24, 40.86) * mm});
            skLineSegment(sketch, "E369", {"start": v(1.24, 40.86) * mm, "end": v(1.77, 40.62) * mm});
            skLineSegment(sketch, "E370", {"start": v(1.77, 40.62) * mm, "end": v(2.25, 40.3) * mm});
            skLineSegment(sketch, "E371", {"start": v(2.25, 40.3) * mm, "end": v(2.66, 39.9) * mm});
            skLineSegment(sketch, "E372", {"start": v(2.66, 39.9) * mm, "end": v(3, 39.44) * mm});
            skLineSegment(sketch, "E373", {"start": v(3, 39.44) * mm, "end": v(3.26, 38.92) * mm});
            skLineSegment(sketch, "E374", {"start": v(3.26, 38.92) * mm, "end": v(3.44, 38.35) * mm});
            skLineSegment(sketch, "E375", {"start": v(3.44, 38.35) * mm, "end": v(3.52, 37.88) * mm});
            skLineSegment(sketch, "E376", {"start": v(3.52, 37.88) * mm, "end": v(3.54, 37.72) * mm});
            skLineSegment(sketch, "E377", {"start": v(3.54, 37.72) * mm, "end": v(3.58, 37.17) * mm});
            skLineSegment(sketch, "E378", {"start": v(3.58, 37.17) * mm, "end": v(4.33, 37.17) * mm});
            skLineSegment(sketch, "E379", {"start": v(4.33, 37.17) * mm, "end": v(4.29, 37.8) * mm});
            skLineSegment(sketch, "E380", {"start": v(4.29, 37.8) * mm, "end": v(4.28, 38) * mm});
            skLineSegment(sketch, "E381", {"start": v(4.28, 38) * mm, "end": v(4.18, 38.59) * mm});
            skLineSegment(sketch, "E382", {"start": v(4.18, 38.59) * mm, "end": v(3.93, 39.31) * mm});
            skLineSegment(sketch, "E383", {"start": v(3.93, 39.31) * mm, "end": v(3.55, 39.98) * mm});
            skLineSegment(sketch, "E384", {"start": v(3.55, 39.98) * mm, "end": v(3.17, 40.44) * mm});
            skLineSegment(sketch, "E385", {"start": v(3.17, 40.44) * mm, "end": v(3.03, 40.58) * mm});
            skLineSegment(sketch, "E386", {"start": v(3.03, 40.58) * mm, "end": v(2.88, 40.73) * mm});
            skLineSegment(sketch, "E387", {"start": v(2.88, 40.73) * mm, "end": v(2.4, 41.12) * mm});
            skLineSegment(sketch, "E388", {"start": v(2.4, 41.12) * mm, "end": v(1.72, 41.5) * mm});
            skLineSegment(sketch, "E389", {"start": v(1.72, 41.5) * mm, "end": v(1, 41.73) * mm});
            skLineSegment(sketch, "E390", {"start": v(1, 41.73) * mm, "end": v(0.39, 41.82) * mm});
            skLineSegment(sketch, "E391", {"start": v(0.39, 41.82) * mm, "end": v(0.19, 41.82) * mm});
            skLineSegment(sketch, "E392", {"start": v(0.19, 41.82) * mm, "end": v(0.12, 41.83) * mm});
            skLineSegment(sketch, "E393", {"start": v(0.12, 41.83) * mm, "end": v(-0.1, 41.83) * mm});
            skLineSegment(sketch, "E394", {"start": v(-0.1, 41.83) * mm, "end": v(-0.36, 41.83) * mm});
            skLineSegment(sketch, "E395", {"start": v(-0.36, 41.83) * mm, "end": v(-0.6, 41.81) * mm});
            skLineSegment(sketch, "E396", {"start": v(-0.6, 41.81) * mm, "end": v(-0.71, 41.8) * mm});
            skLineSegment(sketch, "E397", {"start": v(-0.71, 41.8) * mm, "end": v(-0.75, 41.8) * mm});
            skLineSegment(sketch, "E398", {"start": v(-7.27, 37.82) * mm, "end": v(-7.3, 37.79) * mm});
            skLineSegment(sketch, "E399", {"start": v(-7.3, 37.79) * mm, "end": v(-7.37, 37.68) * mm});
            skLineSegment(sketch, "E400", {"start": v(-7.37, 37.68) * mm, "end": v(-7.4, 37.55) * mm});
            skLineSegment(sketch, "E401", {"start": v(-7.4, 37.55) * mm, "end": v(-7.38, 37.43) * mm});
            skLineSegment(sketch, "E402", {"start": v(-7.38, 37.43) * mm, "end": v(-7.3, 37.33) * mm});
            skLineSegment(sketch, "E403", {"start": v(-7.3, 37.33) * mm, "end": v(-7.28, 37.3) * mm});
            skLineSegment(sketch, "E404", {"start": v(-7.28, 37.3) * mm, "end": v(-7.27, 37.3) * mm});
            skLineSegment(sketch, "E405", {"start": v(-7.27, 37.3) * mm, "end": v(-7.24, 37.26) * mm});
            skLineSegment(sketch, "E406", {"start": v(-7.24, 37.26) * mm, "end": v(-7.18, 37.23) * mm});
            skLineSegment(sketch, "E407", {"start": v(-7.18, 37.23) * mm, "end": v(-7.11, 37.2) * mm});
            skLineSegment(sketch, "E408", {"start": v(-7.11, 37.2) * mm, "end": v(-7.02, 37.2) * mm});
            skLineSegment(sketch, "E409", {"start": v(-7.02, 37.2) * mm, "end": v(-6.9, 37.18) * mm});
            skLineSegment(sketch, "E410", {"start": v(-6.9, 37.18) * mm, "end": v(-6.73, 37.17) * mm});
            skLineSegment(sketch, "E411", {"start": v(-6.73, 37.17) * mm, "end": v(-6.52, 37.17) * mm});
            skLineSegment(sketch, "E412", {"start": v(-6.52, 37.17) * mm, "end": v(-6.31, 37.17) * mm});
            skLineSegment(sketch, "E413", {"start": v(-6.31, 37.17) * mm, "end": v(-6.24, 37.17) * mm});
            skLineSegment(sketch, "E414", {"start": v(-6.24, 37.17) * mm, "end": v(-6.17, 37.17) * mm});
            skLineSegment(sketch, "E415", {"start": v(-6.17, 37.17) * mm, "end": v(-5.97, 37.17) * mm});
            skLineSegment(sketch, "E416", {"start": v(-5.97, 37.17) * mm, "end": v(-5.75, 37.17) * mm});
            skLineSegment(sketch, "E417", {"start": v(-5.75, 37.17) * mm, "end": v(-5.59, 37.18) * mm});
            skLineSegment(sketch, "E418", {"start": v(-5.59, 37.18) * mm, "end": v(-5.46, 37.2) * mm});
            skLineSegment(sketch, "E419", {"start": v(-5.46, 37.2) * mm, "end": v(-5.37, 37.2) * mm});
            skLineSegment(sketch, "E420", {"start": v(-5.37, 37.2) * mm, "end": v(-5.3, 37.23) * mm});
            skLineSegment(sketch, "E421", {"start": v(-5.3, 37.23) * mm, "end": v(-5.25, 37.26) * mm});
            skLineSegment(sketch, "E422", {"start": v(-5.25, 37.26) * mm, "end": v(-5.21, 37.3) * mm});
            skLineSegment(sketch, "E423", {"start": v(-5.21, 37.3) * mm, "end": v(-5.2, 37.3) * mm});
            skLineSegment(sketch, "E424", {"start": v(-5.2, 37.3) * mm, "end": v(-5.18, 37.33) * mm});
            skLineSegment(sketch, "E425", {"start": v(-5.18, 37.33) * mm, "end": v(-5.1, 37.43) * mm});
            skLineSegment(sketch, "E426", {"start": v(-5.1, 37.43) * mm, "end": v(-5.08, 37.57) * mm});
            skLineSegment(sketch, "E427", {"start": v(-5.08, 37.57) * mm, "end": v(-5.1, 37.7) * mm});
            skLineSegment(sketch, "E428", {"start": v(-5.1, 37.7) * mm, "end": v(-5.18, 37.81) * mm});
            skLineSegment(sketch, "E429", {"start": v(-5.18, 37.81) * mm, "end": v(-5.2, 37.84) * mm});
            skLineSegment(sketch, "E430", {"start": v(-5.2, 37.84) * mm, "end": v(-5.22, 37.85) * mm});
            skLineSegment(sketch, "E431", {"start": v(-5.22, 37.85) * mm, "end": v(-5.25, 37.88) * mm});
            skLineSegment(sketch, "E432", {"start": v(-5.25, 37.88) * mm, "end": v(-5.3, 37.91) * mm});
            skLineSegment(sketch, "E433", {"start": v(-5.3, 37.91) * mm, "end": v(-5.37, 37.93) * mm});
            skLineSegment(sketch, "E434", {"start": v(-5.37, 37.93) * mm, "end": v(-5.46, 37.95) * mm});
            skLineSegment(sketch, "E435", {"start": v(-5.46, 37.95) * mm, "end": v(-5.58, 37.96) * mm});
            skLineSegment(sketch, "E436", {"start": v(-5.58, 37.96) * mm, "end": v(-5.75, 37.97) * mm});
            skLineSegment(sketch, "E437", {"start": v(-5.75, 37.97) * mm, "end": v(-5.96, 37.97) * mm});
            skLineSegment(sketch, "E438", {"start": v(-5.96, 37.97) * mm, "end": v(-6.16, 37.97) * mm});
            skLineSegment(sketch, "E439", {"start": v(-6.16, 37.97) * mm, "end": v(-6.23, 37.97) * mm});
            skLineSegment(sketch, "E440", {"start": v(-6.23, 37.97) * mm, "end": v(-6.3, 37.97) * mm});
            skLineSegment(sketch, "E441", {"start": v(-6.3, 37.97) * mm, "end": v(-6.51, 37.97) * mm});
            skLineSegment(sketch, "E442", {"start": v(-6.51, 37.97) * mm, "end": v(-6.73, 37.97) * mm});
            skLineSegment(sketch, "E443", {"start": v(-6.73, 37.97) * mm, "end": v(-6.9, 37.96) * mm});
            skLineSegment(sketch, "E444", {"start": v(-6.9, 37.96) * mm, "end": v(-7.02, 37.95) * mm});
            skLineSegment(sketch, "E445", {"start": v(-7.02, 37.95) * mm, "end": v(-7.1, 37.93) * mm});
            skLineSegment(sketch, "E446", {"start": v(-7.1, 37.93) * mm, "end": v(-7.17, 37.9) * mm});
            skLineSegment(sketch, "E447", {"start": v(-7.17, 37.9) * mm, "end": v(-7.22, 37.87) * mm});
            skLineSegment(sketch, "E448", {"start": v(-7.22, 37.87) * mm, "end": v(-7.26, 37.83) * mm});
            skLineSegment(sketch, "E449", {"start": v(-7.26, 37.83) * mm, "end": v(-7.27, 37.82) * mm});
            skLineSegment(sketch, "E450", {"start": v(5.35, 37.83) * mm, "end": v(5.32, 37.8) * mm});
            skLineSegment(sketch, "E451", {"start": v(5.32, 37.8) * mm, "end": v(5.23, 37.7) * mm});
            skLineSegment(sketch, "E452", {"start": v(5.23, 37.7) * mm, "end": v(5.19, 37.57) * mm});
            skLineSegment(sketch, "E453", {"start": v(5.19, 37.57) * mm, "end": v(5.21, 37.44) * mm});
            skLineSegment(sketch, "E454", {"start": v(5.21, 37.44) * mm, "end": v(5.28, 37.33) * mm});
            skLineSegment(sketch, "E455", {"start": v(5.28, 37.33) * mm, "end": v(5.31, 37.3) * mm});
            skLineSegment(sketch, "E456", {"start": v(5.31, 37.3) * mm, "end": v(5.32, 37.3) * mm});
            skLineSegment(sketch, "E457", {"start": v(5.32, 37.3) * mm, "end": v(5.36, 37.26) * mm});
            skLineSegment(sketch, "E458", {"start": v(5.36, 37.26) * mm, "end": v(5.41, 37.23) * mm});
            skLineSegment(sketch, "E459", {"start": v(5.41, 37.23) * mm, "end": v(5.48, 37.2) * mm});
            skLineSegment(sketch, "E460", {"start": v(5.48, 37.2) * mm, "end": v(5.57, 37.2) * mm});
            skLineSegment(sketch, "E461", {"start": v(5.57, 37.2) * mm, "end": v(5.7, 37.18) * mm});
            skLineSegment(sketch, "E462", {"start": v(5.7, 37.18) * mm, "end": v(5.86, 37.17) * mm});
            skLineSegment(sketch, "E463", {"start": v(5.86, 37.17) * mm, "end": v(6.08, 37.17) * mm});
            skLineSegment(sketch, "E464", {"start": v(6.08, 37.17) * mm, "end": v(6.28, 37.17) * mm});
            skLineSegment(sketch, "E465", {"start": v(6.28, 37.17) * mm, "end": v(6.35, 37.17) * mm});
            skLineSegment(sketch, "E466", {"start": v(6.35, 37.17) * mm, "end": v(6.42, 37.17) * mm});
            skLineSegment(sketch, "E467", {"start": v(6.42, 37.17) * mm, "end": v(6.62, 37.17) * mm});
            skLineSegment(sketch, "E468", {"start": v(6.62, 37.17) * mm, "end": v(6.84, 37.17) * mm});
            skLineSegment(sketch, "E469", {"start": v(6.84, 37.17) * mm, "end": v(7, 37.18) * mm});
            skLineSegment(sketch, "E470", {"start": v(7, 37.18) * mm, "end": v(7.13, 37.2) * mm});
            skLineSegment(sketch, "E471", {"start": v(7.13, 37.2) * mm, "end": v(7.22, 37.2) * mm});
            skLineSegment(sketch, "E472", {"start": v(7.22, 37.2) * mm, "end": v(7.3, 37.23) * mm});
            skLineSegment(sketch, "E473", {"start": v(7.3, 37.23) * mm, "end": v(7.34, 37.26) * mm});
            skLineSegment(sketch, "E474", {"start": v(7.34, 37.26) * mm, "end": v(7.38, 37.3) * mm});
            skLineSegment(sketch, "E475", {"start": v(7.38, 37.3) * mm, "end": v(7.39, 37.3) * mm});
            skLineSegment(sketch, "E476", {"start": v(7.39, 37.3) * mm, "end": v(7.4, 37.32) * mm});
            skLineSegment(sketch, "E477", {"start": v(7.4, 37.32) * mm, "end": v(7.48, 37.44) * mm});
            skLineSegment(sketch, "E478", {"start": v(7.48, 37.44) * mm, "end": v(7.52, 37.54) * mm});
            skLineSegment(sketch, "E479", {"start": v(7.52, 37.54) * mm, "end": v(7.52, 37.57) * mm});
            skLineSegment(sketch, "E480", {"start": v(7.52, 37.57) * mm, "end": v(7.52, 37.6) * mm});
            skLineSegment(sketch, "E481", {"start": v(7.52, 37.6) * mm, "end": v(7.48, 37.7) * mm});
            skLineSegment(sketch, "E482", {"start": v(7.48, 37.7) * mm, "end": v(7.4, 37.82) * mm});
            skLineSegment(sketch, "E483", {"start": v(7.4, 37.82) * mm, "end": v(7.39, 37.84) * mm});
            skLineSegment(sketch, "E484", {"start": v(7.39, 37.84) * mm, "end": v(7.38, 37.85) * mm});
            skLineSegment(sketch, "E485", {"start": v(7.38, 37.85) * mm, "end": v(7.34, 37.88) * mm});
            skLineSegment(sketch, "E486", {"start": v(7.34, 37.88) * mm, "end": v(7.3, 37.91) * mm});
            skLineSegment(sketch, "E487", {"start": v(7.3, 37.91) * mm, "end": v(7.22, 37.93) * mm});
            skLineSegment(sketch, "E488", {"start": v(7.22, 37.93) * mm, "end": v(7.14, 37.95) * mm});
            skLineSegment(sketch, "E489", {"start": v(7.14, 37.95) * mm, "end": v(7.02, 37.96) * mm});
            skLineSegment(sketch, "E490", {"start": v(7.02, 37.96) * mm, "end": v(6.86, 37.97) * mm});
            skLineSegment(sketch, "E491", {"start": v(6.86, 37.97) * mm, "end": v(6.65, 37.97) * mm});
            skLineSegment(sketch, "E492", {"start": v(6.65, 37.97) * mm, "end": v(6.46, 37.97) * mm});
            skLineSegment(sketch, "E493", {"start": v(6.46, 37.97) * mm, "end": v(6.4, 37.97) * mm});
            skLineSegment(sketch, "E494", {"start": v(6.4, 37.97) * mm, "end": v(6.33, 37.97) * mm});
            skLineSegment(sketch, "E495", {"start": v(6.33, 37.97) * mm, "end": v(6.13, 37.97) * mm});
            skLineSegment(sketch, "E496", {"start": v(6.13, 37.97) * mm, "end": v(5.93, 37.97) * mm});
            skLineSegment(sketch, "E497", {"start": v(5.93, 37.97) * mm, "end": v(5.77, 37.96) * mm});
            skLineSegment(sketch, "E498", {"start": v(5.77, 37.96) * mm, "end": v(5.64, 37.95) * mm});
            skLineSegment(sketch, "E499", {"start": v(5.64, 37.95) * mm, "end": v(5.55, 37.93) * mm});
            skLineSegment(sketch, "E500", {"start": v(5.55, 37.93) * mm, "end": v(5.47, 37.9) * mm});
            skLineSegment(sketch, "E501", {"start": v(5.47, 37.9) * mm, "end": v(5.41, 37.87) * mm});
            skLineSegment(sketch, "E502", {"start": v(5.41, 37.87) * mm, "end": v(5.37, 37.84) * mm});
            skLineSegment(sketch, "E503", {"start": v(5.37, 37.84) * mm, "end": v(5.35, 37.83) * mm});
            skLineSegment(sketch, "E504", {"start": v(-1.36, 36.77) * mm, "end": v(-2.69, 35.63) * mm});
            skLineSegment(sketch, "E505", {"start": v(-2.69, 35.63) * mm, "end": v(-4.87, 35.63) * mm});
            skLineSegment(sketch, "E506", {"start": v(-4.87, 35.63) * mm, "end": v(-5.04, 35.63) * mm});
            skLineSegment(sketch, "E507", {"start": v(-5.04, 35.63) * mm, "end": v(-5.57, 35.63) * mm});
            skLineSegment(sketch, "E508", {"start": v(-5.57, 35.63) * mm, "end": v(-6.1, 35.63) * mm});
            skLineSegment(sketch, "E509", {"start": v(-6.1, 35.63) * mm, "end": v(-6.5, 35.62) * mm});
            skLineSegment(sketch, "E510", {"start": v(-6.5, 35.62) * mm, "end": v(-6.78, 35.6) * mm});
            skLineSegment(sketch, "E511", {"start": v(-6.78, 35.6) * mm, "end": v(-6.97, 35.6) * mm});
            skLineSegment(sketch, "E512", {"start": v(-6.97, 35.6) * mm, "end": v(-7.1, 35.57) * mm});
            skLineSegment(sketch, "E513", {"start": v(-7.1, 35.57) * mm, "end": v(-7.18, 35.53) * mm});
            skLineSegment(sketch, "E514", {"start": v(-7.18, 35.53) * mm, "end": v(-7.22, 35.5) * mm});
            skLineSegment(sketch, "E515", {"start": v(-7.22, 35.5) * mm, "end": v(-7.24, 35.49) * mm});
            skLineSegment(sketch, "E516", {"start": v(-7.24, 35.49) * mm, "end": v(-7.27, 35.46) * mm});
            skLineSegment(sketch, "E517", {"start": v(-7.27, 35.46) * mm, "end": v(-7.36, 35.36) * mm});
            skLineSegment(sketch, "E518", {"start": v(-7.36, 35.36) * mm, "end": v(-7.4, 35.23) * mm});
            skLineSegment(sketch, "E519", {"start": v(-7.4, 35.23) * mm, "end": v(-7.38, 35.1) * mm});
            skLineSegment(sketch, "E520", {"start": v(-7.38, 35.1) * mm, "end": v(-7.31, 34.99) * mm});
            skLineSegment(sketch, "E521", {"start": v(-7.31, 34.99) * mm, "end": v(-7.28, 34.96) * mm});
            skLineSegment(sketch, "E522", {"start": v(-7.28, 34.96) * mm, "end": v(-7.27, 34.95) * mm});
            skLineSegment(sketch, "E523", {"start": v(-7.27, 34.95) * mm, "end": v(-7.23, 34.92) * mm});
            skLineSegment(sketch, "E524", {"start": v(-7.23, 34.92) * mm, "end": v(-7.16, 34.88) * mm});
            skLineSegment(sketch, "E525", {"start": v(-7.16, 34.88) * mm, "end": v(-7.03, 34.86) * mm});
            skLineSegment(sketch, "E526", {"start": v(-7.03, 34.86) * mm, "end": v(-6.83, 34.84) * mm});
            skLineSegment(sketch, "E527", {"start": v(-6.83, 34.84) * mm, "end": v(-6.52, 34.83) * mm});
            skLineSegment(sketch, "E528", {"start": v(-6.52, 34.83) * mm, "end": v(-6.08, 34.83) * mm});
            skLineSegment(sketch, "E529", {"start": v(-6.08, 34.83) * mm, "end": v(-5.48, 34.83) * mm});
            skLineSegment(sketch, "E530", {"start": v(-5.48, 34.83) * mm, "end": v(-4.9, 34.82) * mm});
            skLineSegment(sketch, "E531", {"start": v(-4.9, 34.82) * mm, "end": v(-4.7, 34.82) * mm});
            skLineSegment(sketch, "E532", {"start": v(-4.7, 34.82) * mm, "end": v(-2.26, 34.82) * mm});
            skLineSegment(sketch, "E533", {"start": v(-2.26, 34.82) * mm, "end": v(-1.11, 35.78) * mm});
            skLineSegment(sketch, "E534", {"start": v(-1.11, 35.78) * mm, "end": v(-1, 35.88) * mm});
            skLineSegment(sketch, "E535", {"start": v(-1, 35.88) * mm, "end": v(-0.66, 36.15) * mm});
            skLineSegment(sketch, "E536", {"start": v(-0.66, 36.15) * mm, "end": v(-0.3, 36.46) * mm});
            skLineSegment(sketch, "E537", {"start": v(-0.3, 36.46) * mm, "end": v(-0.03, 36.67) * mm});
            skLineSegment(sketch, "E538", {"start": v(-0.03, 36.67) * mm, "end": v(0.07, 36.75) * mm});
            skLineSegment(sketch, "E539", {"start": v(0.07, 36.75) * mm, "end": v(0.07, 36.75) * mm});
            skLineSegment(sketch, "E540", {"start": v(0.07, 36.75) * mm, "end": v(0.08, 36.75) * mm});
            skLineSegment(sketch, "E541", {"start": v(0.08, 36.75) * mm, "end": v(0.18, 36.68) * mm});
            skLineSegment(sketch, "E542", {"start": v(0.18, 36.68) * mm, "end": v(0.45, 36.47) * mm});
            skLineSegment(sketch, "E543", {"start": v(0.45, 36.47) * mm, "end": v(0.83, 36.17) * mm});
            skLineSegment(sketch, "E544", {"start": v(0.83, 36.17) * mm, "end": v(1.17, 35.89) * mm});
            skLineSegment(sketch, "E545", {"start": v(1.17, 35.89) * mm, "end": v(1.28, 35.8) * mm});
            skLineSegment(sketch, "E546", {"start": v(1.28, 35.8) * mm, "end": v(2.45, 34.82) * mm});
            skLineSegment(sketch, "E547", {"start": v(2.45, 34.82) * mm, "end": v(4.9, 34.82) * mm});
            skLineSegment(sketch, "E548", {"start": v(4.9, 34.82) * mm, "end": v(5.1, 34.82) * mm});
            skLineSegment(sketch, "E549", {"start": v(5.1, 34.82) * mm, "end": v(5.67, 34.82) * mm});
            skLineSegment(sketch, "E550", {"start": v(5.67, 34.82) * mm, "end": v(6.26, 34.83) * mm});
            skLineSegment(sketch, "E551", {"start": v(6.26, 34.83) * mm, "end": v(6.7, 34.83) * mm});
            skLineSegment(sketch, "E552", {"start": v(6.7, 34.83) * mm, "end": v(7.02, 34.84) * mm});
            skLineSegment(sketch, "E553", {"start": v(7.02, 34.84) * mm, "end": v(7.23, 34.86) * mm});
            skLineSegment(sketch, "E554", {"start": v(7.23, 34.86) * mm, "end": v(7.36, 34.88) * mm});
            skLineSegment(sketch, "E555", {"start": v(7.36, 34.88) * mm, "end": v(7.43, 34.9) * mm});
            skLineSegment(sketch, "E556", {"start": v(7.43, 34.9) * mm, "end": v(7.47, 34.93) * mm});
            skLineSegment(sketch, "E557", {"start": v(7.47, 34.93) * mm, "end": v(7.48, 34.94) * mm});
            skLineSegment(sketch, "E558", {"start": v(7.48, 34.94) * mm, "end": v(7.5, 34.97) * mm});
            skLineSegment(sketch, "E559", {"start": v(7.5, 34.97) * mm, "end": v(7.56, 35.07) * mm});
            skLineSegment(sketch, "E560", {"start": v(7.56, 35.07) * mm, "end": v(7.58, 35.18) * mm});
            skLineSegment(sketch, "E561", {"start": v(7.58, 35.18) * mm, "end": v(7.53, 35.3) * mm});
            skLineSegment(sketch, "E562", {"start": v(7.53, 35.3) * mm, "end": v(7.45, 35.4) * mm});
            skLineSegment(sketch, "E563", {"start": v(7.45, 35.4) * mm, "end": v(7.42, 35.43) * mm});
            skLineSegment(sketch, "E564", {"start": v(7.42, 35.43) * mm, "end": v(7.24, 35.6) * mm});
            skLineSegment(sketch, "E565", {"start": v(7.24, 35.6) * mm, "end": v(2.71, 35.63) * mm});
            skLineSegment(sketch, "E566", {"start": v(2.71, 35.63) * mm, "end": v(1.39, 36.77) * mm});
            skLineSegment(sketch, "E567", {"start": v(1.39, 36.77) * mm, "end": v(1.26, 36.88) * mm});
            skLineSegment(sketch, "E568", {"start": v(1.26, 36.88) * mm, "end": v(0.87, 37.21) * mm});
            skLineSegment(sketch, "E569", {"start": v(0.87, 37.21) * mm, "end": v(0.44, 37.57) * mm});
            skLineSegment(sketch, "E570", {"start": v(0.44, 37.57) * mm, "end": v(0.14, 37.82) * mm});
            skLineSegment(sketch, "E571", {"start": v(0.14, 37.82) * mm, "end": v(0.04, 37.9) * mm});
            skLineSegment(sketch, "E572", {"start": v(0.04, 37.9) * mm, "end": v(0.01, 37.9) * mm});
            skLineSegment(sketch, "E573", {"start": v(0.01, 37.9) * mm, "end": v(-0.02, 37.9) * mm});
            skLineSegment(sketch, "E574", {"start": v(-0.02, 37.9) * mm, "end": v(-0.1, 37.82) * mm});
            skLineSegment(sketch, "E575", {"start": v(-0.1, 37.82) * mm, "end": v(-0.4, 37.57) * mm});
            skLineSegment(sketch, "E576", {"start": v(-0.4, 37.57) * mm, "end": v(-0.84, 37.21) * mm});
            skLineSegment(sketch, "E577", {"start": v(-0.84, 37.21) * mm, "end": v(-1.23, 36.88) * mm});
            skLineSegment(sketch, "E578", {"start": v(-1.23, 36.88) * mm, "end": v(-1.36, 36.77) * mm});
            skSolve(sketch);
        }
        {
            var Q0;
            Q0=makeQuery(id+"F1.imprint","IMPRINT",FACE,{"disambiguationData":[TD([[makeQuery(id+"F1.imprint","IMPRINT",EDGE,{"derivedFrom":sQuery(id+"F1.wireOp",EDGE,"E6")}),-1.0]])]});
            var sketch = newSketch(context, id + "F3", { "sketchPlane" : qUnion([Q0])});
            skLineSegment(sketch, "E579", {"start": v(-0.2, 26.94) * mm, "end": v(-0.22, 26.93) * mm});
            skLineSegment(sketch, "E580", {"start": v(-0.22, 26.93) * mm, "end": v(-0.28, 26.89) * mm});
            skLineSegment(sketch, "E581", {"start": v(-0.28, 26.89) * mm, "end": v(-0.37, 26.81) * mm});
            skLineSegment(sketch, "E582", {"start": v(-0.37, 26.81) * mm, "end": v(-0.43, 26.73) * mm});
            skLineSegment(sketch, "E583", {"start": v(-0.43, 26.73) * mm, "end": v(-0.47, 26.67) * mm});
            skLineSegment(sketch, "E584", {"start": v(-0.47, 26.67) * mm, "end": v(-0.47, 26.65) * mm});
            skLineSegment(sketch, "E585", {"start": v(-0.47, 26.65) * mm, "end": v(-0.48, 26.64) * mm});
            skLineSegment(sketch, "E586", {"start": v(-0.48, 26.64) * mm, "end": v(-0.48, 26.56) * mm});
            skLineSegment(sketch, "E587", {"start": v(-0.48, 26.56) * mm, "end": v(-0.49, 26.36) * mm});
            skLineSegment(sketch, "E588", {"start": v(-0.49, 26.36) * mm, "end": v(-0.5, 26.08) * mm});
            skLineSegment(sketch, "E589", {"start": v(-0.5, 26.08) * mm, "end": v(-0.5, 25.83) * mm});
            skLineSegment(sketch, "E590", {"start": v(-0.5, 25.83) * mm, "end": v(-0.5, 25.75) * mm});
            skLineSegment(sketch, "E591", {"start": v(-0.5, 25.75) * mm, "end": v(-0.5, 25.68) * mm});
            skLineSegment(sketch, "E592", {"start": v(-0.5, 25.68) * mm, "end": v(-0.5, 25.48) * mm});
            skLineSegment(sketch, "E593", {"start": v(-0.5, 25.48) * mm, "end": v(-0.5, 25.27) * mm});
            skLineSegment(sketch, "E594", {"start": v(-0.5, 25.27) * mm, "end": v(-0.49, 25.12) * mm});
            skLineSegment(sketch, "E595", {"start": v(-0.49, 25.12) * mm, "end": v(-0.49, 25.01) * mm});
            skLineSegment(sketch, "E596", {"start": v(-0.49, 25.01) * mm, "end": v(-0.48, 24.94) * mm});
            skLineSegment(sketch, "E597", {"start": v(-0.48, 24.94) * mm, "end": v(-0.47, 24.89) * mm});
            skLineSegment(sketch, "E598", {"start": v(-0.47, 24.89) * mm, "end": v(-0.45, 24.85) * mm});
            skLineSegment(sketch, "E599", {"start": v(-0.45, 24.85) * mm, "end": v(-0.44, 24.82) * mm});
            skLineSegment(sketch, "E600", {"start": v(-0.44, 24.82) * mm, "end": v(-0.44, 24.81) * mm});
            skLineSegment(sketch, "E601", {"start": v(-0.44, 24.81) * mm, "end": v(-0.41, 24.77) * mm});
            skLineSegment(sketch, "E602", {"start": v(-0.41, 24.77) * mm, "end": v(-0.3, 24.66) * mm});
            skLineSegment(sketch, "E603", {"start": v(-0.3, 24.66) * mm, "end": v(-0.1, 24.57) * mm});
            skLineSegment(sketch, "E604", {"start": v(-0.1, 24.57) * mm, "end": v(0.1, 24.57) * mm});
            skLineSegment(sketch, "E605", {"start": v(0.1, 24.57) * mm, "end": v(0.26, 24.63) * mm});
            skLineSegment(sketch, "E606", {"start": v(0.26, 24.63) * mm, "end": v(0.3, 24.66) * mm});
            skLineSegment(sketch, "E607", {"start": v(0.3, 24.66) * mm, "end": v(0.3, 24.67) * mm});
            skLineSegment(sketch, "E608", {"start": v(0.3, 24.67) * mm, "end": v(0.33, 24.7) * mm});
            skLineSegment(sketch, "E609", {"start": v(0.33, 24.7) * mm, "end": v(0.36, 24.73) * mm});
            skLineSegment(sketch, "E610", {"start": v(0.36, 24.73) * mm, "end": v(0.4, 24.77) * mm});
            skLineSegment(sketch, "E611", {"start": v(0.4, 24.77) * mm, "end": v(0.41, 24.8) * mm});
            skLineSegment(sketch, "E612", {"start": v(0.41, 24.8) * mm, "end": v(0.42, 24.81) * mm});
            skLineSegment(sketch, "E613", {"start": v(0.42, 24.81) * mm, "end": v(0.42, 24.82) * mm});
            skLineSegment(sketch, "E614", {"start": v(0.42, 24.82) * mm, "end": v(0.44, 24.85) * mm});
            skLineSegment(sketch, "E615", {"start": v(0.44, 24.85) * mm, "end": v(0.45, 24.89) * mm});
            skLineSegment(sketch, "E616", {"start": v(0.45, 24.89) * mm, "end": v(0.46, 24.94) * mm});
            skLineSegment(sketch, "E617", {"start": v(0.46, 24.94) * mm, "end": v(0.47, 25) * mm});
            skLineSegment(sketch, "E618", {"start": v(0.47, 25) * mm, "end": v(0.47, 25.1) * mm});
            skLineSegment(sketch, "E619", {"start": v(0.47, 25.1) * mm, "end": v(0.48, 25.23) * mm});
            skLineSegment(sketch, "E620", {"start": v(0.48, 25.23) * mm, "end": v(0.48, 25.4) * mm});
            skLineSegment(sketch, "E621", {"start": v(0.48, 25.4) * mm, "end": v(0.48, 25.58) * mm});
            skLineSegment(sketch, "E622", {"start": v(0.48, 25.58) * mm, "end": v(0.48, 25.64) * mm});
            skLineSegment(sketch, "E623", {"start": v(0.48, 25.64) * mm, "end": v(0.48, 25.71) * mm});
            skLineSegment(sketch, "E624", {"start": v(0.48, 25.71) * mm, "end": v(0.49, 25.94) * mm});
            skLineSegment(sketch, "E625", {"start": v(0.49, 25.94) * mm, "end": v(0.49, 26.17) * mm});
            skLineSegment(sketch, "E626", {"start": v(0.49, 26.17) * mm, "end": v(0.48, 26.35) * mm});
            skLineSegment(sketch, "E627", {"start": v(0.48, 26.35) * mm, "end": v(0.47, 26.49) * mm});
            skLineSegment(sketch, "E628", {"start": v(0.47, 26.49) * mm, "end": v(0.46, 26.59) * mm});
            skLineSegment(sketch, "E629", {"start": v(0.46, 26.59) * mm, "end": v(0.44, 26.66) * mm});
            skLineSegment(sketch, "E630", {"start": v(0.44, 26.66) * mm, "end": v(0.42, 26.72) * mm});
            skLineSegment(sketch, "E631", {"start": v(0.42, 26.72) * mm, "end": v(0.39, 26.76) * mm});
            skLineSegment(sketch, "E632", {"start": v(0.39, 26.76) * mm, "end": v(0.38, 26.77) * mm});
            skLineSegment(sketch, "E633", {"start": v(0.38, 26.77) * mm, "end": v(0.36, 26.8) * mm});
            skLineSegment(sketch, "E634", {"start": v(0.36, 26.8) * mm, "end": v(0.3, 26.86) * mm});
            skLineSegment(sketch, "E635", {"start": v(0.3, 26.86) * mm, "end": v(0.2, 26.93) * mm});
            skLineSegment(sketch, "E636", {"start": v(0.2, 26.93) * mm, "end": v(0.1, 26.97) * mm});
            skLineSegment(sketch, "E637", {"start": v(0.1, 26.97) * mm, "end": v(0.02, 26.99) * mm});
            skLineSegment(sketch, "E638", {"start": v(0.02, 26.99) * mm, "end": v(0, 26.99) * mm});
            skLineSegment(sketch, "E639", {"start": v(0, 26.99) * mm, "end": v(-0.03, 26.99) * mm});
            skLineSegment(sketch, "E640", {"start": v(-0.03, 26.99) * mm, "end": v(-0.1, 26.98) * mm});
            skLineSegment(sketch, "E641", {"start": v(-0.1, 26.98) * mm, "end": v(-0.18, 26.95) * mm});
            skLineSegment(sketch, "E642", {"start": v(-0.18, 26.95) * mm, "end": v(-0.2, 26.94) * mm});
            skLineSegment(sketch, "E643", {"start": v(-3.15, 26.14) * mm, "end": v(-3.2, 26.12) * mm});
            skLineSegment(sketch, "E644", {"start": v(-3.2, 26.12) * mm, "end": v(-3.3, 26.03) * mm});
            skLineSegment(sketch, "E645", {"start": v(-3.3, 26.03) * mm, "end": v(-3.4, 25.87) * mm});
            skLineSegment(sketch, "E646", {"start": v(-3.4, 25.87) * mm, "end": v(-3.42, 25.68) * mm});
            skLineSegment(sketch, "E647", {"start": v(-3.42, 25.68) * mm, "end": v(-3.39, 25.53) * mm});
            skLineSegment(sketch, "E648", {"start": v(-3.39, 25.53) * mm, "end": v(-3.36, 25.49) * mm});
            skLineSegment(sketch, "E649", {"start": v(-3.36, 25.49) * mm, "end": v(-3.35, 25.45) * mm});
            skLineSegment(sketch, "E650", {"start": v(-3.35, 25.45) * mm, "end": v(-3.29, 25.35) * mm});
            skLineSegment(sketch, "E651", {"start": v(-3.29, 25.35) * mm, "end": v(-3.18, 25.15) * mm});
            skLineSegment(sketch, "E652", {"start": v(-3.18, 25.15) * mm, "end": v(-3.05, 24.93) * mm});
            skLineSegment(sketch, "E653", {"start": v(-3.05, 24.93) * mm, "end": v(-2.91, 24.7) * mm});
            skLineSegment(sketch, "E654", {"start": v(-2.91, 24.7) * mm, "end": v(-2.78, 24.48) * mm});
            skLineSegment(sketch, "E655", {"start": v(-2.78, 24.48) * mm, "end": v(-2.66, 24.3) * mm});
            skLineSegment(sketch, "E656", {"start": v(-2.66, 24.3) * mm, "end": v(-2.57, 24.15) * mm});
            skLineSegment(sketch, "E657", {"start": v(-2.57, 24.15) * mm, "end": v(-2.54, 24.1) * mm});
            skLineSegment(sketch, "E658", {"start": v(-2.54, 24.1) * mm, "end": v(-2.52, 24.09) * mm});
            skLineSegment(sketch, "E659", {"start": v(-2.52, 24.09) * mm, "end": v(-2.5, 24.06) * mm});
            skLineSegment(sketch, "E660", {"start": v(-2.5, 24.06) * mm, "end": v(-2.38, 24) * mm});
            skLineSegment(sketch, "E661", {"start": v(-2.38, 24) * mm, "end": v(-2.23, 23.97) * mm});
            skLineSegment(sketch, "E662", {"start": v(-2.23, 23.97) * mm, "end": v(-2.07, 23.99) * mm});
            skLineSegment(sketch, "E663", {"start": v(-2.07, 23.99) * mm, "end": v(-1.96, 24.04) * mm});
            skLineSegment(sketch, "E664", {"start": v(-1.96, 24.04) * mm, "end": v(-1.93, 24.06) * mm});
            skLineSegment(sketch, "E665", {"start": v(-1.93, 24.06) * mm, "end": v(-1.9, 24.08) * mm});
            skLineSegment(sketch, "E666", {"start": v(-1.9, 24.08) * mm, "end": v(-1.78, 24.23) * mm});
            skLineSegment(sketch, "E667", {"start": v(-1.78, 24.23) * mm, "end": v(-1.73, 24.4) * mm});
            skLineSegment(sketch, "E668", {"start": v(-1.73, 24.4) * mm, "end": v(-1.73, 24.46) * mm});
            skLineSegment(sketch, "E669", {"start": v(-1.73, 24.46) * mm, "end": v(-1.73, 24.47) * mm});
            skLineSegment(sketch, "E670", {"start": v(-1.73, 24.47) * mm, "end": v(-1.73, 24.5) * mm});
            skLineSegment(sketch, "E671", {"start": v(-1.73, 24.5) * mm, "end": v(-1.74, 24.55) * mm});
            skLineSegment(sketch, "E672", {"start": v(-1.74, 24.55) * mm, "end": v(-1.75, 24.6) * mm});
            skLineSegment(sketch, "E673", {"start": v(-1.75, 24.6) * mm, "end": v(-1.78, 24.66) * mm});
            skLineSegment(sketch, "E674", {"start": v(-1.78, 24.66) * mm, "end": v(-1.82, 24.74) * mm});
            skLineSegment(sketch, "E675", {"start": v(-1.82, 24.74) * mm, "end": v(-1.88, 24.85) * mm});
            skLineSegment(sketch, "E676", {"start": v(-1.88, 24.85) * mm, "end": v(-1.96, 25) * mm});
            skLineSegment(sketch, "E677", {"start": v(-1.96, 25) * mm, "end": v(-2.04, 25.14) * mm});
            skLineSegment(sketch, "E678", {"start": v(-2.04, 25.14) * mm, "end": v(-2.06, 25.18) * mm});
            skLineSegment(sketch, "E679", {"start": v(-2.06, 25.18) * mm, "end": v(-2.1, 25.25) * mm});
            skLineSegment(sketch, "E680", {"start": v(-2.1, 25.25) * mm, "end": v(-2.22, 25.45) * mm});
            skLineSegment(sketch, "E681", {"start": v(-2.22, 25.45) * mm, "end": v(-2.34, 25.66) * mm});
            skLineSegment(sketch, "E682", {"start": v(-2.34, 25.66) * mm, "end": v(-2.44, 25.82) * mm});
            skLineSegment(sketch, "E683", {"start": v(-2.44, 25.82) * mm, "end": v(-2.52, 25.94) * mm});
            skLineSegment(sketch, "E684", {"start": v(-2.52, 25.94) * mm, "end": v(-2.58, 26.02) * mm});
            skLineSegment(sketch, "E685", {"start": v(-2.58, 26.02) * mm, "end": v(-2.63, 26.08) * mm});
            skLineSegment(sketch, "E686", {"start": v(-2.63, 26.08) * mm, "end": v(-2.67, 26.11) * mm});
            skLineSegment(sketch, "E687", {"start": v(-2.67, 26.11) * mm, "end": v(-2.7, 26.14) * mm});
            skLineSegment(sketch, "E688", {"start": v(-2.7, 26.14) * mm, "end": v(-2.72, 26.14) * mm});
            skLineSegment(sketch, "E689", {"start": v(-2.72, 26.14) * mm, "end": v(-2.75, 26.16) * mm});
            skLineSegment(sketch, "E690", {"start": v(-2.75, 26.16) * mm, "end": v(-2.94, 26.2) * mm});
            skLineSegment(sketch, "E691", {"start": v(-2.94, 26.2) * mm, "end": v(-3.12, 26.16) * mm});
            skLineSegment(sketch, "E692", {"start": v(-3.12, 26.16) * mm, "end": v(-3.15, 26.14) * mm});
            skLineSegment(sketch, "E693", {"start": v(2.75, 26.17) * mm, "end": v(2.74, 26.17) * mm});
            skLineSegment(sketch, "E694", {"start": v(2.74, 26.17) * mm, "end": v(2.71, 26.15) * mm});
            skLineSegment(sketch, "E695", {"start": v(2.71, 26.15) * mm, "end": v(2.67, 26.13) * mm});
            skLineSegment(sketch, "E696", {"start": v(2.67, 26.13) * mm, "end": v(2.63, 26.1) * mm});
            skLineSegment(sketch, "E697", {"start": v(2.63, 26.1) * mm, "end": v(2.6, 26.07) * mm});
            skLineSegment(sketch, "E698", {"start": v(2.6, 26.07) * mm, "end": v(2.6, 26.06) * mm});
            skLineSegment(sketch, "E699", {"start": v(2.6, 26.06) * mm, "end": v(2.57, 26.05) * mm});
            skLineSegment(sketch, "E700", {"start": v(2.57, 26.05) * mm, "end": v(2.54, 25.99) * mm});
            skLineSegment(sketch, "E701", {"start": v(2.54, 25.99) * mm, "end": v(2.44, 25.83) * mm});
            skLineSegment(sketch, "E702", {"start": v(2.44, 25.83) * mm, "end": v(2.3, 25.61) * mm});
            skLineSegment(sketch, "E703", {"start": v(2.3, 25.61) * mm, "end": v(2.16, 25.37) * mm});
            skLineSegment(sketch, "E704", {"start": v(2.16, 25.37) * mm, "end": v(2.02, 25.12) * mm});
            skLineSegment(sketch, "E705", {"start": v(2.02, 25.12) * mm, "end": v(1.89, 24.9) * mm});
            skLineSegment(sketch, "E706", {"start": v(1.89, 24.9) * mm, "end": v(1.79, 24.71) * mm});
            skLineSegment(sketch, "E707", {"start": v(1.79, 24.71) * mm, "end": v(1.74, 24.63) * mm});
            skLineSegment(sketch, "E708", {"start": v(1.74, 24.63) * mm, "end": v(1.73, 24.6) * mm});
            skLineSegment(sketch, "E709", {"start": v(1.73, 24.6) * mm, "end": v(1.72, 24.58) * mm});
            skLineSegment(sketch, "E710", {"start": v(1.72, 24.58) * mm, "end": v(1.7, 24.52) * mm});
            skLineSegment(sketch, "E711", {"start": v(1.7, 24.52) * mm, "end": v(1.7, 24.44) * mm});
            skLineSegment(sketch, "E712", {"start": v(1.7, 24.44) * mm, "end": v(1.72, 24.35) * mm});
            skLineSegment(sketch, "E713", {"start": v(1.72, 24.35) * mm, "end": v(1.74, 24.28) * mm});
            skLineSegment(sketch, "E714", {"start": v(1.74, 24.28) * mm, "end": v(1.75, 24.26) * mm});
            skLineSegment(sketch, "E715", {"start": v(1.75, 24.26) * mm, "end": v(1.76, 24.23) * mm});
            skLineSegment(sketch, "E716", {"start": v(1.76, 24.23) * mm, "end": v(1.8, 24.15) * mm});
            skLineSegment(sketch, "E717", {"start": v(1.8, 24.15) * mm, "end": v(1.89, 24.07) * mm});
            skLineSegment(sketch, "E718", {"start": v(1.89, 24.07) * mm, "end": v(1.98, 24.01) * mm});
            skLineSegment(sketch, "E719", {"start": v(1.98, 24.01) * mm, "end": v(2.08, 23.98) * mm});
            skLineSegment(sketch, "E720", {"start": v(2.08, 23.98) * mm, "end": v(2.2, 23.97) * mm});
            skLineSegment(sketch, "E721", {"start": v(2.2, 23.97) * mm, "end": v(2.3, 23.98) * mm});
            skLineSegment(sketch, "E722", {"start": v(2.3, 23.98) * mm, "end": v(2.4, 24.02) * mm});
            skLineSegment(sketch, "E723", {"start": v(2.4, 24.02) * mm, "end": v(2.48, 24.07) * mm});
            skLineSegment(sketch, "E724", {"start": v(2.48, 24.07) * mm, "end": v(2.5, 24.09) * mm});
            skLineSegment(sketch, "E725", {"start": v(2.5, 24.09) * mm, "end": v(2.52, 24.1) * mm});
            skLineSegment(sketch, "E726", {"start": v(2.52, 24.1) * mm, "end": v(2.57, 24.16) * mm});
            skLineSegment(sketch, "E727", {"start": v(2.57, 24.16) * mm, "end": v(2.67, 24.31) * mm});
            skLineSegment(sketch, "E728", {"start": v(2.67, 24.31) * mm, "end": v(2.8, 24.53) * mm});
            skLineSegment(sketch, "E729", {"start": v(2.8, 24.53) * mm, "end": v(2.91, 24.72) * mm});
            skLineSegment(sketch, "E730", {"start": v(2.91, 24.72) * mm, "end": v(2.95, 24.79) * mm});
            skLineSegment(sketch, "E731", {"start": v(2.95, 24.79) * mm, "end": v(3, 24.86) * mm});
            skLineSegment(sketch, "E732", {"start": v(3, 24.86) * mm, "end": v(3.11, 25.07) * mm});
            skLineSegment(sketch, "E733", {"start": v(3.11, 25.07) * mm, "end": v(3.23, 25.29) * mm});
            skLineSegment(sketch, "E734", {"start": v(3.23, 25.29) * mm, "end": v(3.32, 25.45) * mm});
            skLineSegment(sketch, "E735", {"start": v(3.32, 25.45) * mm, "end": v(3.38, 25.57) * mm});
            skLineSegment(sketch, "E736", {"start": v(3.38, 25.57) * mm, "end": v(3.4, 25.66) * mm});
            skLineSegment(sketch, "E737", {"start": v(3.4, 25.66) * mm, "end": v(3.41, 25.72) * mm});
            skLineSegment(sketch, "E738", {"start": v(3.41, 25.72) * mm, "end": v(3.4, 25.79) * mm});
            skLineSegment(sketch, "E739", {"start": v(3.4, 25.79) * mm, "end": v(3.4, 25.84) * mm});
            skLineSegment(sketch, "E740", {"start": v(3.4, 25.84) * mm, "end": v(3.39, 25.85) * mm});
            skLineSegment(sketch, "E741", {"start": v(3.39, 25.85) * mm, "end": v(3.37, 25.9) * mm});
            skLineSegment(sketch, "E742", {"start": v(3.37, 25.9) * mm, "end": v(3.29, 26.03) * mm});
            skLineSegment(sketch, "E743", {"start": v(3.29, 26.03) * mm, "end": v(3.14, 26.14) * mm});
            skLineSegment(sketch, "E744", {"start": v(3.14, 26.14) * mm, "end": v(2.96, 26.2) * mm});
            skLineSegment(sketch, "E745", {"start": v(2.96, 26.2) * mm, "end": v(2.8, 26.18) * mm});
            skLineSegment(sketch, "E746", {"start": v(2.8, 26.18) * mm, "end": v(2.75, 26.17) * mm});
            skLineSegment(sketch, "E747", {"start": v(-5.23, 24.03) * mm, "end": v(-5.28, 24.02) * mm});
            skLineSegment(sketch, "E748", {"start": v(-5.28, 24.02) * mm, "end": v(-5.42, 23.91) * mm});
            skLineSegment(sketch, "E749", {"start": v(-5.42, 23.91) * mm, "end": v(-5.53, 23.74) * mm});
            skLineSegment(sketch, "E750", {"start": v(-5.53, 23.74) * mm, "end": v(-5.56, 23.52) * mm});
            skLineSegment(sketch, "E751", {"start": v(-5.56, 23.52) * mm, "end": v(-5.52, 23.36) * mm});
            skLineSegment(sketch, "E752", {"start": v(-5.52, 23.36) * mm, "end": v(-5.5, 23.31) * mm});
            skLineSegment(sketch, "E753", {"start": v(-5.5, 23.31) * mm, "end": v(-5.49, 23.3) * mm});
            skLineSegment(sketch, "E754", {"start": v(-5.49, 23.3) * mm, "end": v(-5.47, 23.27) * mm});
            skLineSegment(sketch, "E755", {"start": v(-5.47, 23.27) * mm, "end": v(-5.43, 23.24) * mm});
            skLineSegment(sketch, "E756", {"start": v(-5.43, 23.24) * mm, "end": v(-5.38, 23.2) * mm});
            skLineSegment(sketch, "E757", {"start": v(-5.38, 23.2) * mm, "end": v(-5.3, 23.14) * mm});
            skLineSegment(sketch, "E758", {"start": v(-5.3, 23.14) * mm, "end": v(-5.2, 23.07) * mm});
            skLineSegment(sketch, "E759", {"start": v(-5.2, 23.07) * mm, "end": v(-5.04, 22.98) * mm});
            skLineSegment(sketch, "E760", {"start": v(-5.04, 22.98) * mm, "end": v(-4.84, 22.86) * mm});
            skLineSegment(sketch, "E761", {"start": v(-4.84, 22.86) * mm, "end": v(-4.65, 22.75) * mm});
            skLineSegment(sketch, "E762", {"start": v(-4.65, 22.75) * mm, "end": v(-4.59, 22.72) * mm});
            skLineSegment(sketch, "E763", {"start": v(-4.59, 22.72) * mm, "end": v(-4.54, 22.69) * mm});
            skLineSegment(sketch, "E764", {"start": v(-4.54, 22.69) * mm, "end": v(-4.4, 22.6) * mm});
            skLineSegment(sketch, "E765", {"start": v(-4.4, 22.6) * mm, "end": v(-4.25, 22.53) * mm});
            skLineSegment(sketch, "E766", {"start": v(-4.25, 22.53) * mm, "end": v(-4.13, 22.46) * mm});
            skLineSegment(sketch, "E767", {"start": v(-4.13, 22.46) * mm, "end": v(-4.04, 22.41) * mm});
            skLineSegment(sketch, "E768", {"start": v(-4.04, 22.41) * mm, "end": v(-3.96, 22.38) * mm});
            skLineSegment(sketch, "E769", {"start": v(-3.96, 22.38) * mm, "end": v(-3.9, 22.36) * mm});
            skLineSegment(sketch, "E770", {"start": v(-3.9, 22.36) * mm, "end": v(-3.86, 22.35) * mm});
            skLineSegment(sketch, "E771", {"start": v(-3.86, 22.35) * mm, "end": v(-3.83, 22.35) * mm});
            skLineSegment(sketch, "E772", {"start": v(-3.83, 22.35) * mm, "end": v(-3.82, 22.35) * mm});
            skLineSegment(sketch, "E773", {"start": v(-3.82, 22.35) * mm, "end": v(-3.8, 22.35) * mm});
            skLineSegment(sketch, "E774", {"start": v(-3.8, 22.35) * mm, "end": v(-3.73, 22.36) * mm});
            skLineSegment(sketch, "E775", {"start": v(-3.73, 22.36) * mm, "end": v(-3.63, 22.4) * mm});
            skLineSegment(sketch, "E776", {"start": v(-3.63, 22.4) * mm, "end": v(-3.53, 22.45) * mm});
            skLineSegment(sketch, "E777", {"start": v(-3.53, 22.45) * mm, "end": v(-3.48, 22.49) * mm});
            skLineSegment(sketch, "E778", {"start": v(-3.48, 22.49) * mm, "end": v(-3.46, 22.5) * mm});
            skLineSegment(sketch, "E779", {"start": v(-3.46, 22.5) * mm, "end": v(-3.43, 22.54) * mm});
            skLineSegment(sketch, "E780", {"start": v(-3.43, 22.54) * mm, "end": v(-3.36, 22.67) * mm});
            skLineSegment(sketch, "E781", {"start": v(-3.36, 22.67) * mm, "end": v(-3.34, 22.86) * mm});
            skLineSegment(sketch, "E782", {"start": v(-3.34, 22.86) * mm, "end": v(-3.38, 23.04) * mm});
            skLineSegment(sketch, "E783", {"start": v(-3.38, 23.04) * mm, "end": v(-3.46, 23.17) * mm});
            skLineSegment(sketch, "E784", {"start": v(-3.46, 23.17) * mm, "end": v(-3.5, 23.2) * mm});
            skLineSegment(sketch, "E785", {"start": v(-3.5, 23.2) * mm, "end": v(-3.51, 23.21) * mm});
            skLineSegment(sketch, "E786", {"start": v(-3.51, 23.21) * mm, "end": v(-3.57, 23.25) * mm});
            skLineSegment(sketch, "E787", {"start": v(-3.57, 23.25) * mm, "end": v(-3.72, 23.34) * mm});
            skLineSegment(sketch, "E788", {"start": v(-3.72, 23.34) * mm, "end": v(-3.91, 23.46) * mm});
            skLineSegment(sketch, "E789", {"start": v(-3.91, 23.46) * mm, "end": v(-4.14, 23.6) * mm});
            skLineSegment(sketch, "E790", {"start": v(-4.14, 23.6) * mm, "end": v(-4.37, 23.72) * mm});
            skLineSegment(sketch, "E791", {"start": v(-4.37, 23.72) * mm, "end": v(-4.59, 23.85) * mm});
            skLineSegment(sketch, "E792", {"start": v(-4.59, 23.85) * mm, "end": v(-4.77, 23.94) * mm});
            skLineSegment(sketch, "E793", {"start": v(-4.77, 23.94) * mm, "end": v(-4.85, 23.99) * mm});
            skLineSegment(sketch, "E794", {"start": v(-4.85, 23.99) * mm, "end": v(-4.88, 24) * mm});
            skLineSegment(sketch, "E795", {"start": v(-4.88, 24) * mm, "end": v(-4.9, 24.01) * mm});
            skLineSegment(sketch, "E796", {"start": v(-4.9, 24.01) * mm, "end": v(-4.98, 24.04) * mm});
            skLineSegment(sketch, "E797", {"start": v(-4.98, 24.04) * mm, "end": v(-5.06, 24.06) * mm});
            skLineSegment(sketch, "E798", {"start": v(-5.06, 24.06) * mm, "end": v(-5.14, 24.06) * mm});
            skLineSegment(sketch, "E799", {"start": v(-5.14, 24.06) * mm, "end": v(-5.2, 24.04) * mm});
            skLineSegment(sketch, "E800", {"start": v(-5.2, 24.04) * mm, "end": v(-5.23, 24.03) * mm});
            skLineSegment(sketch, "E801", {"start": v(-0.37, 24.04) * mm, "end": v(-0.51, 24.02) * mm});
            skLineSegment(sketch, "E802", {"start": v(-0.51, 24.02) * mm, "end": v(-0.95, 23.93) * mm});
            skLineSegment(sketch, "E803", {"start": v(-0.95, 23.93) * mm, "end": v(-1.48, 23.73) * mm});
            skLineSegment(sketch, "E804", {"start": v(-1.48, 23.73) * mm, "end": v(-1.96, 23.43) * mm});
            skLineSegment(sketch, "E805", {"start": v(-1.96, 23.43) * mm, "end": v(-2.31, 23.15) * mm});
            skLineSegment(sketch, "E806", {"start": v(-2.31, 23.15) * mm, "end": v(-2.41, 23.05) * mm});
            skLineSegment(sketch, "E807", {"start": v(-2.41, 23.05) * mm, "end": v(-2.54, 22.93) * mm});
            skLineSegment(sketch, "E808", {"start": v(-2.54, 22.93) * mm, "end": v(-2.86, 22.52) * mm});
            skLineSegment(sketch, "E809", {"start": v(-2.86, 22.52) * mm, "end": v(-3.17, 21.95) * mm});
            skLineSegment(sketch, "E810", {"start": v(-3.17, 21.95) * mm, "end": v(-3.35, 21.32) * mm});
            skLineSegment(sketch, "E811", {"start": v(-3.35, 21.32) * mm, "end": v(-3.41, 20.81) * mm});
            skLineSegment(sketch, "E812", {"start": v(-3.41, 20.81) * mm, "end": v(-3.41, 20.64) * mm});
            skLineSegment(sketch, "E813", {"start": v(-3.41, 20.64) * mm, "end": v(-3.41, 20.47) * mm});
            skLineSegment(sketch, "E814", {"start": v(-3.41, 20.47) * mm, "end": v(-3.35, 19.96) * mm});
            skLineSegment(sketch, "E815", {"start": v(-3.35, 19.96) * mm, "end": v(-3.17, 19.33) * mm});
            skLineSegment(sketch, "E816", {"start": v(-3.17, 19.33) * mm, "end": v(-2.86, 18.76) * mm});
            skLineSegment(sketch, "E817", {"start": v(-2.86, 18.76) * mm, "end": v(-2.54, 18.35) * mm});
            skLineSegment(sketch, "E818", {"start": v(-2.54, 18.35) * mm, "end": v(-2.41, 18.23) * mm});
            skLineSegment(sketch, "E819", {"start": v(-2.41, 18.23) * mm, "end": v(-2.3, 18.11) * mm});
            skLineSegment(sketch, "E820", {"start": v(-2.3, 18.11) * mm, "end": v(-1.89, 17.8) * mm});
            skLineSegment(sketch, "E821", {"start": v(-1.89, 17.8) * mm, "end": v(-1.32, 17.48) * mm});
            skLineSegment(sketch, "E822", {"start": v(-1.32, 17.48) * mm, "end": v(-0.69, 17.3) * mm});
            skLineSegment(sketch, "E823", {"start": v(-0.69, 17.3) * mm, "end": v(-0.18, 17.23) * mm});
            skLineSegment(sketch, "E824", {"start": v(-0.18, 17.23) * mm, "end": v(0, 17.23) * mm});
            skLineSegment(sketch, "E825", {"start": v(0, 17.23) * mm, "end": v(0.16, 17.23) * mm});
            skLineSegment(sketch, "E826", {"start": v(0.16, 17.23) * mm, "end": v(0.67, 17.3) * mm});
            skLineSegment(sketch, "E827", {"start": v(0.67, 17.3) * mm, "end": v(1.3, 17.48) * mm});
            skLineSegment(sketch, "E828", {"start": v(1.3, 17.48) * mm, "end": v(1.87, 17.8) * mm});
            skLineSegment(sketch, "E829", {"start": v(1.87, 17.8) * mm, "end": v(2.28, 18.11) * mm});
            skLineSegment(sketch, "E830", {"start": v(2.28, 18.11) * mm, "end": v(2.4, 18.23) * mm});
            skLineSegment(sketch, "E831", {"start": v(2.4, 18.23) * mm, "end": v(2.52, 18.35) * mm});
            skLineSegment(sketch, "E832", {"start": v(2.52, 18.35) * mm, "end": v(2.84, 18.76) * mm});
            skLineSegment(sketch, "E833", {"start": v(2.84, 18.76) * mm, "end": v(3.15, 19.33) * mm});
            skLineSegment(sketch, "E834", {"start": v(3.15, 19.33) * mm, "end": v(3.34, 19.96) * mm});
            skLineSegment(sketch, "E835", {"start": v(3.34, 19.96) * mm, "end": v(3.4, 20.47) * mm});
            skLineSegment(sketch, "E836", {"start": v(3.4, 20.47) * mm, "end": v(3.4, 20.64) * mm});
            skLineSegment(sketch, "E837", {"start": v(3.4, 20.64) * mm, "end": v(3.4, 20.81) * mm});
            skLineSegment(sketch, "E838", {"start": v(3.4, 20.81) * mm, "end": v(3.34, 21.32) * mm});
            skLineSegment(sketch, "E839", {"start": v(3.34, 21.32) * mm, "end": v(3.15, 21.95) * mm});
            skLineSegment(sketch, "E840", {"start": v(3.15, 21.95) * mm, "end": v(2.84, 22.52) * mm});
            skLineSegment(sketch, "E841", {"start": v(2.84, 22.52) * mm, "end": v(2.52, 22.93) * mm});
            skLineSegment(sketch, "E842", {"start": v(2.52, 22.93) * mm, "end": v(2.4, 23.05) * mm});
            skLineSegment(sketch, "E843", {"start": v(2.4, 23.05) * mm, "end": v(2.32, 23.12) * mm});
            skLineSegment(sketch, "E844", {"start": v(2.32, 23.12) * mm, "end": v(2.1, 23.33) * mm});
            skLineSegment(sketch, "E845", {"start": v(2.1, 23.33) * mm, "end": v(1.78, 23.55) * mm});
            skLineSegment(sketch, "E846", {"start": v(1.78, 23.55) * mm, "end": v(1.45, 23.73) * mm});
            skLineSegment(sketch, "E847", {"start": v(1.45, 23.73) * mm, "end": v(1.17, 23.85) * mm});
            skLineSegment(sketch, "E848", {"start": v(1.17, 23.85) * mm, "end": v(1.08, 23.88) * mm});
            skLineSegment(sketch, "E849", {"start": v(1.08, 23.88) * mm, "end": v(0.99, 23.9) * mm});
            skLineSegment(sketch, "E850", {"start": v(0.99, 23.9) * mm, "end": v(0.73, 23.97) * mm});
            skLineSegment(sketch, "E851", {"start": v(0.73, 23.97) * mm, "end": v(0.35, 24.03) * mm});
            skLineSegment(sketch, "E852", {"start": v(0.35, 24.03) * mm, "end": v(-0.02, 24.05) * mm});
            skLineSegment(sketch, "E853", {"start": v(-0.02, 24.05) * mm, "end": v(-0.28, 24.05) * mm});
            skLineSegment(sketch, "E854", {"start": v(-0.28, 24.05) * mm, "end": v(-0.37, 24.04) * mm});
            skLineSegment(sketch, "E855", {"start": v(0.59, 23) * mm, "end": v(0.68, 22.98) * mm});
            skLineSegment(sketch, "E856", {"start": v(0.68, 22.98) * mm, "end": v(0.97, 22.87) * mm});
            skLineSegment(sketch, "E857", {"start": v(0.97, 22.87) * mm, "end": v(1.3, 22.7) * mm});
            skLineSegment(sketch, "E858", {"start": v(1.3, 22.7) * mm, "end": v(1.58, 22.49) * mm});
            skLineSegment(sketch, "E859", {"start": v(1.58, 22.49) * mm, "end": v(1.78, 22.29) * mm});
            skLineSegment(sketch, "E860", {"start": v(1.78, 22.29) * mm, "end": v(1.85, 22.22) * mm});
            skLineSegment(sketch, "E861", {"start": v(1.85, 22.22) * mm, "end": v(1.89, 22.17) * mm});
            skLineSegment(sketch, "E862", {"start": v(1.89, 22.17) * mm, "end": v(2, 22.01) * mm});
            skLineSegment(sketch, "E863", {"start": v(2, 22.01) * mm, "end": v(2.14, 21.78) * mm});
            skLineSegment(sketch, "E864", {"start": v(2.14, 21.78) * mm, "end": v(2.26, 21.52) * mm});
            skLineSegment(sketch, "E865", {"start": v(2.26, 21.52) * mm, "end": v(2.34, 21.3) * mm});
            skLineSegment(sketch, "E866", {"start": v(2.34, 21.3) * mm, "end": v(2.37, 21.22) * mm});
            skLineSegment(sketch, "E867", {"start": v(2.37, 21.22) * mm, "end": v(2.37, 21.2) * mm});
            skLineSegment(sketch, "E868", {"start": v(2.37, 21.2) * mm, "end": v(2.39, 21.13) * mm});
            skLineSegment(sketch, "E869", {"start": v(2.39, 21.13) * mm, "end": v(2.4, 21.02) * mm});
            skLineSegment(sketch, "E870", {"start": v(2.4, 21.02) * mm, "end": v(2.4, 20.86) * mm});
            skLineSegment(sketch, "E871", {"start": v(2.4, 20.86) * mm, "end": v(2.4, 20.7) * mm});
            skLineSegment(sketch, "E872", {"start": v(2.4, 20.7) * mm, "end": v(2.4, 20.64) * mm});
            skLineSegment(sketch, "E873", {"start": v(2.4, 20.64) * mm, "end": v(2.4, 20.57) * mm});
            skLineSegment(sketch, "E874", {"start": v(2.4, 20.57) * mm, "end": v(2.4, 20.36) * mm});
            skLineSegment(sketch, "E875", {"start": v(2.4, 20.36) * mm, "end": v(2.39, 20.16) * mm});
            skLineSegment(sketch, "E876", {"start": v(2.39, 20.16) * mm, "end": v(2.34, 19.98) * mm});
            skLineSegment(sketch, "E877", {"start": v(2.34, 19.98) * mm, "end": v(2.28, 19.8) * mm});
            skLineSegment(sketch, "E878", {"start": v(2.28, 19.8) * mm, "end": v(2.26, 19.75) * mm});
            skLineSegment(sketch, "E879", {"start": v(2.26, 19.75) * mm, "end": v(2.24, 19.7) * mm});
            skLineSegment(sketch, "E880", {"start": v(2.24, 19.7) * mm, "end": v(2.16, 19.53) * mm});
            skLineSegment(sketch, "E881", {"start": v(2.16, 19.53) * mm, "end": v(2.03, 19.31) * mm});
            skLineSegment(sketch, "E882", {"start": v(2.03, 19.31) * mm, "end": v(1.88, 19.1) * mm});
            skLineSegment(sketch, "E883", {"start": v(1.88, 19.1) * mm, "end": v(1.71, 18.92) * mm});
            skLineSegment(sketch, "E884", {"start": v(1.71, 18.92) * mm, "end": v(1.52, 18.75) * mm});
            skLineSegment(sketch, "E885", {"start": v(1.52, 18.75) * mm, "end": v(1.32, 18.6) * mm});
            skLineSegment(sketch, "E886", {"start": v(1.32, 18.6) * mm, "end": v(1.1, 18.47) * mm});
            skLineSegment(sketch, "E887", {"start": v(1.1, 18.47) * mm, "end": v(0.94, 18.4) * mm});
            skLineSegment(sketch, "E888", {"start": v(0.94, 18.4) * mm, "end": v(0.88, 18.37) * mm});
            skLineSegment(sketch, "E889", {"start": v(0.88, 18.37) * mm, "end": v(0.83, 18.35) * mm});
            skLineSegment(sketch, "E890", {"start": v(0.83, 18.35) * mm, "end": v(0.65, 18.29) * mm});
            skLineSegment(sketch, "E891", {"start": v(0.65, 18.29) * mm, "end": v(0.47, 18.24) * mm});
            skLineSegment(sketch, "E892", {"start": v(0.47, 18.24) * mm, "end": v(0.27, 18.23) * mm});
            skLineSegment(sketch, "E893", {"start": v(0.27, 18.23) * mm, "end": v(0.06, 18.22) * mm});
            skLineSegment(sketch, "E894", {"start": v(0.06, 18.22) * mm, "end": v(0, 18.22) * mm});
            skLineSegment(sketch, "E895", {"start": v(0, 18.22) * mm, "end": v(-0.08, 18.22) * mm});
            skLineSegment(sketch, "E896", {"start": v(-0.08, 18.22) * mm, "end": v(-0.29, 18.23) * mm});
            skLineSegment(sketch, "E897", {"start": v(-0.29, 18.23) * mm, "end": v(-0.49, 18.24) * mm});
            skLineSegment(sketch, "E898", {"start": v(-0.49, 18.24) * mm, "end": v(-0.67, 18.29) * mm});
            skLineSegment(sketch, "E899", {"start": v(-0.67, 18.29) * mm, "end": v(-0.84, 18.35) * mm});
            skLineSegment(sketch, "E900", {"start": v(-0.84, 18.35) * mm, "end": v(-0.9, 18.37) * mm});
            skLineSegment(sketch, "E901", {"start": v(-0.9, 18.37) * mm, "end": v(-0.96, 18.4) * mm});
            skLineSegment(sketch, "E902", {"start": v(-0.96, 18.4) * mm, "end": v(-1.12, 18.47) * mm});
            skLineSegment(sketch, "E903", {"start": v(-1.12, 18.47) * mm, "end": v(-1.34, 18.6) * mm});
            skLineSegment(sketch, "E904", {"start": v(-1.34, 18.6) * mm, "end": v(-1.54, 18.75) * mm});
            skLineSegment(sketch, "E905", {"start": v(-1.54, 18.75) * mm, "end": v(-1.73, 18.92) * mm});
            skLineSegment(sketch, "E906", {"start": v(-1.73, 18.92) * mm, "end": v(-1.9, 19.1) * mm});
            skLineSegment(sketch, "E907", {"start": v(-1.9, 19.1) * mm, "end": v(-2.05, 19.31) * mm});
            skLineSegment(sketch, "E908", {"start": v(-2.05, 19.31) * mm, "end": v(-2.18, 19.53) * mm});
            skLineSegment(sketch, "E909", {"start": v(-2.18, 19.53) * mm, "end": v(-2.25, 19.7) * mm});
            skLineSegment(sketch, "E910", {"start": v(-2.25, 19.7) * mm, "end": v(-2.28, 19.75) * mm});
            skLineSegment(sketch, "E911", {"start": v(-2.28, 19.75) * mm, "end": v(-2.3, 19.8) * mm});
            skLineSegment(sketch, "E912", {"start": v(-2.3, 19.8) * mm, "end": v(-2.35, 19.95) * mm});
            skLineSegment(sketch, "E913", {"start": v(-2.35, 19.95) * mm, "end": v(-2.4, 20.12) * mm});
            skLineSegment(sketch, "E914", {"start": v(-2.4, 20.12) * mm, "end": v(-2.42, 20.3) * mm});
            skLineSegment(sketch, "E915", {"start": v(-2.42, 20.3) * mm, "end": v(-2.43, 20.46) * mm});
            skLineSegment(sketch, "E916", {"start": v(-2.43, 20.46) * mm, "end": v(-2.43, 20.52) * mm});
            skLineSegment(sketch, "E917", {"start": v(-2.43, 20.52) * mm, "end": v(-2.43, 20.58) * mm});
            skLineSegment(sketch, "E918", {"start": v(-2.43, 20.58) * mm, "end": v(-2.43, 20.78) * mm});
            skLineSegment(sketch, "E919", {"start": v(-2.43, 20.78) * mm, "end": v(-2.42, 21) * mm});
            skLineSegment(sketch, "E920", {"start": v(-2.42, 21) * mm, "end": v(-2.38, 21.2) * mm});
            skLineSegment(sketch, "E921", {"start": v(-2.38, 21.2) * mm, "end": v(-2.34, 21.37) * mm});
            skLineSegment(sketch, "E922", {"start": v(-2.34, 21.37) * mm, "end": v(-2.32, 21.42) * mm});
            skLineSegment(sketch, "E923", {"start": v(-2.32, 21.42) * mm, "end": v(-2.28, 21.53) * mm});
            skLineSegment(sketch, "E924", {"start": v(-2.28, 21.53) * mm, "end": v(-2.12, 21.86) * mm});
            skLineSegment(sketch, "E925", {"start": v(-2.12, 21.86) * mm, "end": v(-1.84, 22.25) * mm});
            skLineSegment(sketch, "E926", {"start": v(-1.84, 22.25) * mm, "end": v(-1.5, 22.57) * mm});
            skLineSegment(sketch, "E927", {"start": v(-1.5, 22.57) * mm, "end": v(-1.2, 22.78) * mm});
            skLineSegment(sketch, "E928", {"start": v(-1.2, 22.78) * mm, "end": v(-1.09, 22.83) * mm});
            skLineSegment(sketch, "E929", {"start": v(-1.09, 22.83) * mm, "end": v(-1.05, 22.85) * mm});
            skLineSegment(sketch, "E930", {"start": v(-1.05, 22.85) * mm, "end": v(-0.95, 22.9) * mm});
            skLineSegment(sketch, "E931", {"start": v(-0.95, 22.9) * mm, "end": v(-0.77, 22.95) * mm});
            skLineSegment(sketch, "E932", {"start": v(-0.77, 22.95) * mm, "end": v(-0.59, 23.01) * mm});
            skLineSegment(sketch, "E933", {"start": v(-0.59, 23.01) * mm, "end": v(-0.48, 23.04) * mm});
            skLineSegment(sketch, "E934", {"start": v(-0.48, 23.04) * mm, "end": v(-0.44, 23.05) * mm});
            skLineSegment(sketch, "E935", {"start": v(-0.44, 23.05) * mm, "end": v(-0.42, 23.05) * mm});
            skLineSegment(sketch, "E936", {"start": v(-0.42, 23.05) * mm, "end": v(-0.35, 23.06) * mm});
            skLineSegment(sketch, "E937", {"start": v(-0.35, 23.06) * mm, "end": v(-0.22, 23.06) * mm});
            skLineSegment(sketch, "E938", {"start": v(-0.22, 23.06) * mm, "end": v(-0.07, 23.06) * mm});
            skLineSegment(sketch, "E939", {"start": v(-0.07, 23.06) * mm, "end": v(0.09, 23.06) * mm});
            skLineSegment(sketch, "E940", {"start": v(0.09, 23.06) * mm, "end": v(0.24, 23.05) * mm});
            skLineSegment(sketch, "E941", {"start": v(0.24, 23.05) * mm, "end": v(0.39, 23.04) * mm});
            skLineSegment(sketch, "E942", {"start": v(0.39, 23.04) * mm, "end": v(0.5, 23.03) * mm});
            skLineSegment(sketch, "E943", {"start": v(0.5, 23.03) * mm, "end": v(0.57, 23.01) * mm});
            skLineSegment(sketch, "E944", {"start": v(0.57, 23.01) * mm, "end": v(0.59, 23) * mm});
            skLineSegment(sketch, "E945", {"start": v(4.98, 24.04) * mm, "end": v(4.97, 24.04) * mm});
            skLineSegment(sketch, "E946", {"start": v(4.97, 24.04) * mm, "end": v(4.94, 24.03) * mm});
            skLineSegment(sketch, "E947", {"start": v(4.94, 24.03) * mm, "end": v(4.9, 24.02) * mm});
            skLineSegment(sketch, "E948", {"start": v(4.9, 24.02) * mm, "end": v(4.85, 24) * mm});
            skLineSegment(sketch, "E949", {"start": v(4.85, 24) * mm, "end": v(4.78, 23.96) * mm});
            skLineSegment(sketch, "E950", {"start": v(4.78, 23.96) * mm, "end": v(4.68, 23.91) * mm});
            skLineSegment(sketch, "E951", {"start": v(4.68, 23.91) * mm, "end": v(4.55, 23.83) * mm});
            skLineSegment(sketch, "E952", {"start": v(4.55, 23.83) * mm, "end": v(4.37, 23.73) * mm});
            skLineSegment(sketch, "E953", {"start": v(4.37, 23.73) * mm, "end": v(4.2, 23.63) * mm});
            skLineSegment(sketch, "E954", {"start": v(4.2, 23.63) * mm, "end": v(4.13, 23.6) * mm});
            skLineSegment(sketch, "E955", {"start": v(4.13, 23.6) * mm, "end": v(4.08, 23.56) * mm});
            skLineSegment(sketch, "E956", {"start": v(4.08, 23.56) * mm, "end": v(3.9, 23.46) * mm});
            skLineSegment(sketch, "E957", {"start": v(3.9, 23.46) * mm, "end": v(3.7, 23.34) * mm});
            skLineSegment(sketch, "E958", {"start": v(3.7, 23.34) * mm, "end": v(3.55, 23.24) * mm});
            skLineSegment(sketch, "E959", {"start": v(3.55, 23.24) * mm, "end": v(3.48, 23.2) * mm});
            skLineSegment(sketch, "E960", {"start": v(3.48, 23.2) * mm, "end": v(3.47, 23.19) * mm});
            skLineSegment(sketch, "E961", {"start": v(3.47, 23.19) * mm, "end": v(3.43, 23.15) * mm});
            skLineSegment(sketch, "E962", {"start": v(3.43, 23.15) * mm, "end": v(3.35, 23) * mm});
            skLineSegment(sketch, "E963", {"start": v(3.35, 23) * mm, "end": v(3.32, 22.79) * mm});
            skLineSegment(sketch, "E964", {"start": v(3.32, 22.79) * mm, "end": v(3.4, 22.58) * mm});
            skLineSegment(sketch, "E965", {"start": v(3.4, 22.58) * mm, "end": v(3.5, 22.45) * mm});
            skLineSegment(sketch, "E966", {"start": v(3.5, 22.45) * mm, "end": v(3.56, 22.42) * mm});
            skLineSegment(sketch, "E967", {"start": v(3.56, 22.42) * mm, "end": v(3.57, 22.42) * mm});
            skLineSegment(sketch, "E968", {"start": v(3.57, 22.42) * mm, "end": v(3.6, 22.4) * mm});
            skLineSegment(sketch, "E969", {"start": v(3.6, 22.4) * mm, "end": v(3.66, 22.38) * mm});
            skLineSegment(sketch, "E970", {"start": v(3.66, 22.38) * mm, "end": v(3.72, 22.37) * mm});
            skLineSegment(sketch, "E971", {"start": v(3.72, 22.37) * mm, "end": v(3.78, 22.36) * mm});
            skLineSegment(sketch, "E972", {"start": v(3.78, 22.36) * mm, "end": v(3.8, 22.36) * mm});
            skLineSegment(sketch, "E973", {"start": v(3.8, 22.36) * mm, "end": v(3.81, 22.36) * mm});
            skLineSegment(sketch, "E974", {"start": v(3.81, 22.36) * mm, "end": v(3.85, 22.36) * mm});
            skLineSegment(sketch, "E975", {"start": v(3.85, 22.36) * mm, "end": v(3.9, 22.37) * mm});
            skLineSegment(sketch, "E976", {"start": v(3.9, 22.37) * mm, "end": v(3.95, 22.38) * mm});
            skLineSegment(sketch, "E977", {"start": v(3.95, 22.38) * mm, "end": v(4, 22.4) * mm});
            skLineSegment(sketch, "E978", {"start": v(4, 22.4) * mm, "end": v(4.09, 22.45) * mm});
            skLineSegment(sketch, "E979", {"start": v(4.09, 22.45) * mm, "end": v(4.2, 22.5) * mm});
            skLineSegment(sketch, "E980", {"start": v(4.2, 22.5) * mm, "end": v(4.34, 22.59) * mm});
            skLineSegment(sketch, "E981", {"start": v(4.34, 22.59) * mm, "end": v(4.49, 22.67) * mm});
            skLineSegment(sketch, "E982", {"start": v(4.49, 22.67) * mm, "end": v(4.53, 22.7) * mm});
            skLineSegment(sketch, "E983", {"start": v(4.53, 22.7) * mm, "end": v(4.6, 22.74) * mm});
            skLineSegment(sketch, "E984", {"start": v(4.6, 22.74) * mm, "end": v(4.8, 22.85) * mm});
            skLineSegment(sketch, "E985", {"start": v(4.8, 22.85) * mm, "end": v(5.02, 22.98) * mm});
            skLineSegment(sketch, "E986", {"start": v(5.02, 22.98) * mm, "end": v(5.18, 23.07) * mm});
            skLineSegment(sketch, "E987", {"start": v(5.18, 23.07) * mm, "end": v(5.3, 23.15) * mm});
            skLineSegment(sketch, "E988", {"start": v(5.3, 23.15) * mm, "end": v(5.37, 23.2) * mm});
            skLineSegment(sketch, "E989", {"start": v(5.37, 23.2) * mm, "end": v(5.43, 23.26) * mm});
            skLineSegment(sketch, "E990", {"start": v(5.43, 23.26) * mm, "end": v(5.47, 23.3) * mm});
            skLineSegment(sketch, "E991", {"start": v(5.47, 23.3) * mm, "end": v(5.49, 23.34) * mm});
            skLineSegment(sketch, "E992", {"start": v(5.49, 23.34) * mm, "end": v(5.5, 23.36) * mm});
            skLineSegment(sketch, "E993", {"start": v(5.5, 23.36) * mm, "end": v(5.51, 23.39) * mm});
            skLineSegment(sketch, "E994", {"start": v(5.51, 23.39) * mm, "end": v(5.54, 23.5) * mm});
            skLineSegment(sketch, "E995", {"start": v(5.54, 23.5) * mm, "end": v(5.54, 23.62) * mm});
            skLineSegment(sketch, "E996", {"start": v(5.54, 23.62) * mm, "end": v(5.5, 23.75) * mm});
            skLineSegment(sketch, "E997", {"start": v(5.5, 23.75) * mm, "end": v(5.45, 23.86) * mm});
            skLineSegment(sketch, "E998", {"start": v(5.45, 23.86) * mm, "end": v(5.36, 23.95) * mm});
            skLineSegment(sketch, "E999", {"start": v(5.36, 23.95) * mm, "end": v(5.24, 24.02) * mm});
            skLineSegment(sketch, "E1000", {"start": v(5.24, 24.02) * mm, "end": v(5.12, 24.05) * mm});
            skLineSegment(sketch, "E1001", {"start": v(5.12, 24.05) * mm, "end": v(5.01, 24.05) * mm});
            skLineSegment(sketch, "E1002", {"start": v(5.01, 24.05) * mm, "end": v(4.98, 24.04) * mm});
            skLineSegment(sketch, "E1003", {"start": v(-5.97, 21.11) * mm, "end": v(-6, 21.1) * mm});
            skLineSegment(sketch, "E1004", {"start": v(-6, 21.1) * mm, "end": v(-6.11, 21.05) * mm});
            skLineSegment(sketch, "E1005", {"start": v(-6.11, 21.05) * mm, "end": v(-6.24, 20.94) * mm});
            skLineSegment(sketch, "E1006", {"start": v(-6.24, 20.94) * mm, "end": v(-6.33, 20.8) * mm});
            skLineSegment(sketch, "E1007", {"start": v(-6.33, 20.8) * mm, "end": v(-6.36, 20.68) * mm});
            skLineSegment(sketch, "E1008", {"start": v(-6.36, 20.68) * mm, "end": v(-6.36, 20.64) * mm});
            skLineSegment(sketch, "E1009", {"start": v(-6.36, 20.64) * mm, "end": v(-6.36, 20.6) * mm});
            skLineSegment(sketch, "E1010", {"start": v(-6.36, 20.6) * mm, "end": v(-6.33, 20.5) * mm});
            skLineSegment(sketch, "E1011", {"start": v(-6.33, 20.5) * mm, "end": v(-6.25, 20.36) * mm});
            skLineSegment(sketch, "E1012", {"start": v(-6.25, 20.36) * mm, "end": v(-6.14, 20.24) * mm});
            skLineSegment(sketch, "E1013", {"start": v(-6.14, 20.24) * mm, "end": v(-6.05, 20.18) * mm});
            skLineSegment(sketch, "E1014", {"start": v(-6.05, 20.18) * mm, "end": v(-6.02, 20.18) * mm});
            skLineSegment(sketch, "E1015", {"start": v(-6.02, 20.18) * mm, "end": v(-6, 20.17) * mm});
            skLineSegment(sketch, "E1016", {"start": v(-6, 20.17) * mm, "end": v(-5.92, 20.17) * mm});
            skLineSegment(sketch, "E1017", {"start": v(-5.92, 20.17) * mm, "end": v(-5.72, 20.16) * mm});
            skLineSegment(sketch, "E1018", {"start": v(-5.72, 20.16) * mm, "end": v(-5.45, 20.16) * mm});
            skLineSegment(sketch, "E1019", {"start": v(-5.45, 20.16) * mm, "end": v(-5.2, 20.16) * mm});
            skLineSegment(sketch, "E1020", {"start": v(-5.2, 20.16) * mm, "end": v(-5.12, 20.16) * mm});
            skLineSegment(sketch, "E1021", {"start": v(-5.12, 20.16) * mm, "end": v(-5.05, 20.16) * mm});
            skLineSegment(sketch, "E1022", {"start": v(-5.05, 20.16) * mm, "end": v(-4.85, 20.16) * mm});
            skLineSegment(sketch, "E1023", {"start": v(-4.85, 20.16) * mm, "end": v(-4.64, 20.16) * mm});
            skLineSegment(sketch, "E1024", {"start": v(-4.64, 20.16) * mm, "end": v(-4.5, 20.16) * mm});
            skLineSegment(sketch, "E1025", {"start": v(-4.5, 20.16) * mm, "end": v(-4.38, 20.16) * mm});
            skLineSegment(sketch, "E1026", {"start": v(-4.38, 20.16) * mm, "end": v(-4.3, 20.17) * mm});
            skLineSegment(sketch, "E1027", {"start": v(-4.3, 20.17) * mm, "end": v(-4.26, 20.18) * mm});
            skLineSegment(sketch, "E1028", {"start": v(-4.26, 20.18) * mm, "end": v(-4.22, 20.2) * mm});
            skLineSegment(sketch, "E1029", {"start": v(-4.22, 20.2) * mm, "end": v(-4.2, 20.2) * mm});
            skLineSegment(sketch, "E1030", {"start": v(-4.2, 20.2) * mm, "end": v(-4.18, 20.21) * mm});
            skLineSegment(sketch, "E1031", {"start": v(-4.18, 20.21) * mm, "end": v(-4.14, 20.24) * mm});
            skLineSegment(sketch, "E1032", {"start": v(-4.14, 20.24) * mm, "end": v(-4.02, 20.35) * mm});
            skLineSegment(sketch, "E1033", {"start": v(-4.02, 20.35) * mm, "end": v(-3.94, 20.55) * mm});
            skLineSegment(sketch, "E1034", {"start": v(-3.94, 20.55) * mm, "end": v(-3.94, 20.76) * mm});
            skLineSegment(sketch, "E1035", {"start": v(-3.94, 20.76) * mm, "end": v(-4, 20.9) * mm});
            skLineSegment(sketch, "E1036", {"start": v(-4, 20.9) * mm, "end": v(-4.03, 20.95) * mm});
            skLineSegment(sketch, "E1037", {"start": v(-4.03, 20.95) * mm, "end": v(-4.04, 20.96) * mm});
            skLineSegment(sketch, "E1038", {"start": v(-4.04, 20.96) * mm, "end": v(-4.06, 20.98) * mm});
            skLineSegment(sketch, "E1039", {"start": v(-4.06, 20.98) * mm, "end": v(-4.1, 21.01) * mm});
            skLineSegment(sketch, "E1040", {"start": v(-4.1, 21.01) * mm, "end": v(-4.14, 21.04) * mm});
            skLineSegment(sketch, "E1041", {"start": v(-4.14, 21.04) * mm, "end": v(-4.17, 21.06) * mm});
            skLineSegment(sketch, "E1042", {"start": v(-4.17, 21.06) * mm, "end": v(-4.18, 21.07) * mm});
            skLineSegment(sketch, "E1043", {"start": v(-4.18, 21.07) * mm, "end": v(-4.2, 21.07) * mm});
            skLineSegment(sketch, "E1044", {"start": v(-4.2, 21.07) * mm, "end": v(-4.22, 21.09) * mm});
            skLineSegment(sketch, "E1045", {"start": v(-4.22, 21.09) * mm, "end": v(-4.26, 21.1) * mm});
            skLineSegment(sketch, "E1046", {"start": v(-4.26, 21.1) * mm, "end": v(-4.3, 21.1) * mm});
            skLineSegment(sketch, "E1047", {"start": v(-4.3, 21.1) * mm, "end": v(-4.38, 21.12) * mm});
            skLineSegment(sketch, "E1048", {"start": v(-4.38, 21.12) * mm, "end": v(-4.49, 21.12) * mm});
            skLineSegment(sketch, "E1049", {"start": v(-4.49, 21.12) * mm, "end": v(-4.63, 21.12) * mm});
            skLineSegment(sketch, "E1050", {"start": v(-4.63, 21.12) * mm, "end": v(-4.83, 21.13) * mm});
            skLineSegment(sketch, "E1051", {"start": v(-4.83, 21.13) * mm, "end": v(-5.02, 21.13) * mm});
            skLineSegment(sketch, "E1052", {"start": v(-5.02, 21.13) * mm, "end": v(-5.08, 21.13) * mm});
            skLineSegment(sketch, "E1053", {"start": v(-5.08, 21.13) * mm, "end": v(-5.16, 21.13) * mm});
            skLineSegment(sketch, "E1054", {"start": v(-5.16, 21.13) * mm, "end": v(-5.4, 21.13) * mm});
            skLineSegment(sketch, "E1055", {"start": v(-5.4, 21.13) * mm, "end": v(-5.67, 21.13) * mm});
            skLineSegment(sketch, "E1056", {"start": v(-5.67, 21.13) * mm, "end": v(-5.87, 21.12) * mm});
            skLineSegment(sketch, "E1057", {"start": v(-5.87, 21.12) * mm, "end": v(-5.96, 21.12) * mm});
            skLineSegment(sketch, "E1058", {"start": v(-5.96, 21.12) * mm, "end": v(-5.97, 21.11) * mm});
            skLineSegment(sketch, "E1059", {"start": v(4.3, 21.11) * mm, "end": v(4.26, 21.1) * mm});
            skLineSegment(sketch, "E1060", {"start": v(4.26, 21.1) * mm, "end": v(4.15, 21.05) * mm});
            skLineSegment(sketch, "E1061", {"start": v(4.15, 21.05) * mm, "end": v(4.03, 20.96) * mm});
            skLineSegment(sketch, "E1062", {"start": v(4.03, 20.96) * mm, "end": v(3.95, 20.84) * mm});
            skLineSegment(sketch, "E1063", {"start": v(3.95, 20.84) * mm, "end": v(3.92, 20.73) * mm});
            skLineSegment(sketch, "E1064", {"start": v(3.92, 20.73) * mm, "end": v(3.92, 20.7) * mm});
            skLineSegment(sketch, "E1065", {"start": v(3.92, 20.7) * mm, "end": v(3.91, 20.65) * mm});
            skLineSegment(sketch, "E1066", {"start": v(3.91, 20.65) * mm, "end": v(3.92, 20.54) * mm});
            skLineSegment(sketch, "E1067", {"start": v(3.92, 20.54) * mm, "end": v(3.96, 20.4) * mm});
            skLineSegment(sketch, "E1068", {"start": v(3.96, 20.4) * mm, "end": v(4.05, 20.3) * mm});
            skLineSegment(sketch, "E1069", {"start": v(4.05, 20.3) * mm, "end": v(4.13, 20.23) * mm});
            skLineSegment(sketch, "E1070", {"start": v(4.13, 20.23) * mm, "end": v(4.17, 20.21) * mm});
            skLineSegment(sketch, "E1071", {"start": v(4.17, 20.21) * mm, "end": v(4.17, 20.2) * mm});
            skLineSegment(sketch, "E1072", {"start": v(4.17, 20.2) * mm, "end": v(4.2, 20.2) * mm});
            skLineSegment(sketch, "E1073", {"start": v(4.2, 20.2) * mm, "end": v(4.24, 20.18) * mm});
            skLineSegment(sketch, "E1074", {"start": v(4.24, 20.18) * mm, "end": v(4.29, 20.17) * mm});
            skLineSegment(sketch, "E1075", {"start": v(4.29, 20.17) * mm, "end": v(4.36, 20.16) * mm});
            skLineSegment(sketch, "E1076", {"start": v(4.36, 20.16) * mm, "end": v(4.45, 20.16) * mm});
            skLineSegment(sketch, "E1077", {"start": v(4.45, 20.16) * mm, "end": v(4.58, 20.15) * mm});
            skLineSegment(sketch, "E1078", {"start": v(4.58, 20.15) * mm, "end": v(4.76, 20.15) * mm});
            skLineSegment(sketch, "E1079", {"start": v(4.76, 20.15) * mm, "end": v(4.93, 20.15) * mm});
            skLineSegment(sketch, "E1080", {"start": v(4.93, 20.15) * mm, "end": v(4.99, 20.15) * mm});
            skLineSegment(sketch, "E1081", {"start": v(4.99, 20.15) * mm, "end": v(5.06, 20.15) * mm});
            skLineSegment(sketch, "E1082", {"start": v(5.06, 20.15) * mm, "end": v(5.29, 20.15) * mm});
            skLineSegment(sketch, "E1083", {"start": v(5.29, 20.15) * mm, "end": v(5.53, 20.15) * mm});
            skLineSegment(sketch, "E1084", {"start": v(5.53, 20.15) * mm, "end": v(5.7, 20.15) * mm});
            skLineSegment(sketch, "E1085", {"start": v(5.7, 20.15) * mm, "end": v(5.84, 20.16) * mm});
            skLineSegment(sketch, "E1086", {"start": v(5.84, 20.16) * mm, "end": v(5.94, 20.17) * mm});
            skLineSegment(sketch, "E1087", {"start": v(5.94, 20.17) * mm, "end": v(6.02, 20.19) * mm});
            skLineSegment(sketch, "E1088", {"start": v(6.02, 20.19) * mm, "end": v(6.07, 20.22) * mm});
            skLineSegment(sketch, "E1089", {"start": v(6.07, 20.22) * mm, "end": v(6.11, 20.24) * mm});
            skLineSegment(sketch, "E1090", {"start": v(6.11, 20.24) * mm, "end": v(6.13, 20.25) * mm});
            skLineSegment(sketch, "E1091", {"start": v(6.13, 20.25) * mm, "end": v(6.15, 20.27) * mm});
            skLineSegment(sketch, "E1092", {"start": v(6.15, 20.27) * mm, "end": v(6.2, 20.33) * mm});
            skLineSegment(sketch, "E1093", {"start": v(6.2, 20.33) * mm, "end": v(6.28, 20.43) * mm});
            skLineSegment(sketch, "E1094", {"start": v(6.28, 20.43) * mm, "end": v(6.32, 20.54) * mm});
            skLineSegment(sketch, "E1095", {"start": v(6.32, 20.54) * mm, "end": v(6.34, 20.6) * mm});
            skLineSegment(sketch, "E1096", {"start": v(6.34, 20.6) * mm, "end": v(6.34, 20.63) * mm});
            skLineSegment(sketch, "E1097", {"start": v(6.34, 20.63) * mm, "end": v(6.34, 20.66) * mm});
            skLineSegment(sketch, "E1098", {"start": v(6.34, 20.66) * mm, "end": v(6.32, 20.76) * mm});
            skLineSegment(sketch, "E1099", {"start": v(6.32, 20.76) * mm, "end": v(6.26, 20.89) * mm});
            skLineSegment(sketch, "E1100", {"start": v(6.26, 20.89) * mm, "end": v(6.17, 21) * mm});
            skLineSegment(sketch, "E1101", {"start": v(6.17, 21) * mm, "end": v(6.09, 21.06) * mm});
            skLineSegment(sketch, "E1102", {"start": v(6.09, 21.06) * mm, "end": v(6.06, 21.08) * mm});
            skLineSegment(sketch, "E1103", {"start": v(6.06, 21.08) * mm, "end": v(6.05, 21.09) * mm});
            skLineSegment(sketch, "E1104", {"start": v(6.05, 21.09) * mm, "end": v(6.03, 21.1) * mm});
            skLineSegment(sketch, "E1105", {"start": v(6.03, 21.1) * mm, "end": v(5.99, 21.1) * mm});
            skLineSegment(sketch, "E1106", {"start": v(5.99, 21.1) * mm, "end": v(5.93, 21.11) * mm});
            skLineSegment(sketch, "E1107", {"start": v(5.93, 21.11) * mm, "end": v(5.85, 21.12) * mm});
            skLineSegment(sketch, "E1108", {"start": v(5.85, 21.12) * mm, "end": v(5.74, 21.12) * mm});
            skLineSegment(sketch, "E1109", {"start": v(5.74, 21.12) * mm, "end": v(5.6, 21.12) * mm});
            skLineSegment(sketch, "E1110", {"start": v(5.6, 21.12) * mm, "end": v(5.41, 21.13) * mm});
            skLineSegment(sketch, "E1111", {"start": v(5.41, 21.13) * mm, "end": v(5.23, 21.13) * mm});
            skLineSegment(sketch, "E1112", {"start": v(5.23, 21.13) * mm, "end": v(5.18, 21.13) * mm});
            skLineSegment(sketch, "E1113", {"start": v(5.18, 21.13) * mm, "end": v(5.1, 21.13) * mm});
            skLineSegment(sketch, "E1114", {"start": v(5.1, 21.13) * mm, "end": v(4.86, 21.13) * mm});
            skLineSegment(sketch, "E1115", {"start": v(4.86, 21.13) * mm, "end": v(4.58, 21.13) * mm});
            skLineSegment(sketch, "E1116", {"start": v(4.58, 21.13) * mm, "end": v(4.39, 21.12) * mm});
            skLineSegment(sketch, "E1117", {"start": v(4.39, 21.12) * mm, "end": v(4.3, 21.12) * mm});
            skLineSegment(sketch, "E1118", {"start": v(4.3, 21.12) * mm, "end": v(4.3, 21.11) * mm});
            skLineSegment(sketch, "E1119", {"start": v(-4, 18.9) * mm, "end": v(-4.01, 18.88) * mm});
            skLineSegment(sketch, "E1120", {"start": v(-4.01, 18.88) * mm, "end": v(-4.08, 18.85) * mm});
            skLineSegment(sketch, "E1121", {"start": v(-4.08, 18.85) * mm, "end": v(-4.24, 18.76) * mm});
            skLineSegment(sketch, "E1122", {"start": v(-4.24, 18.76) * mm, "end": v(-4.45, 18.64) * mm});
            skLineSegment(sketch, "E1123", {"start": v(-4.45, 18.64) * mm, "end": v(-4.68, 18.5) * mm});
            skLineSegment(sketch, "E1124", {"start": v(-4.68, 18.5) * mm, "end": v(-4.9, 18.38) * mm});
            skLineSegment(sketch, "E1125", {"start": v(-4.9, 18.38) * mm, "end": v(-5.11, 18.25) * mm});
            skLineSegment(sketch, "E1126", {"start": v(-5.11, 18.25) * mm, "end": v(-5.27, 18.16) * mm});
            skLineSegment(sketch, "E1127", {"start": v(-5.27, 18.16) * mm, "end": v(-5.34, 18.12) * mm});
            skLineSegment(sketch, "E1128", {"start": v(-5.34, 18.12) * mm, "end": v(-5.36, 18.1) * mm});
            skLineSegment(sketch, "E1129", {"start": v(-5.36, 18.1) * mm, "end": v(-5.39, 18.08) * mm});
            skLineSegment(sketch, "E1130", {"start": v(-5.39, 18.08) * mm, "end": v(-5.46, 18) * mm});
            skLineSegment(sketch, "E1131", {"start": v(-5.46, 18) * mm, "end": v(-5.53, 17.9) * mm});
            skLineSegment(sketch, "E1132", {"start": v(-5.53, 17.9) * mm, "end": v(-5.56, 17.77) * mm});
            skLineSegment(sketch, "E1133", {"start": v(-5.56, 17.77) * mm, "end": v(-5.56, 17.64) * mm});
            skLineSegment(sketch, "E1134", {"start": v(-5.56, 17.64) * mm, "end": v(-5.52, 17.51) * mm});
            skLineSegment(sketch, "E1135", {"start": v(-5.52, 17.51) * mm, "end": v(-5.45, 17.4) * mm});
            skLineSegment(sketch, "E1136", {"start": v(-5.45, 17.4) * mm, "end": v(-5.35, 17.31) * mm});
            skLineSegment(sketch, "E1137", {"start": v(-5.35, 17.31) * mm, "end": v(-5.25, 17.26) * mm});
            skLineSegment(sketch, "E1138", {"start": v(-5.25, 17.26) * mm, "end": v(-5.22, 17.25) * mm});
            skLineSegment(sketch, "E1139", {"start": v(-5.22, 17.25) * mm, "end": v(-5.2, 17.24) * mm});
            skLineSegment(sketch, "E1140", {"start": v(-5.2, 17.24) * mm, "end": v(-5.14, 17.23) * mm});
            skLineSegment(sketch, "E1141", {"start": v(-5.14, 17.23) * mm, "end": v(-5.04, 17.23) * mm});
            skLineSegment(sketch, "E1142", {"start": v(-5.04, 17.23) * mm, "end": v(-4.94, 17.26) * mm});
            skLineSegment(sketch, "E1143", {"start": v(-4.94, 17.26) * mm, "end": v(-4.86, 17.29) * mm});
            skLineSegment(sketch, "E1144", {"start": v(-4.86, 17.29) * mm, "end": v(-4.83, 17.3) * mm});
            skLineSegment(sketch, "E1145", {"start": v(-4.83, 17.3) * mm, "end": v(-4.8, 17.32) * mm});
            skLineSegment(sketch, "E1146", {"start": v(-4.8, 17.32) * mm, "end": v(-4.7, 17.37) * mm});
            skLineSegment(sketch, "E1147", {"start": v(-4.7, 17.37) * mm, "end": v(-4.52, 17.47) * mm});
            skLineSegment(sketch, "E1148", {"start": v(-4.52, 17.47) * mm, "end": v(-4.3, 17.6) * mm});
            skLineSegment(sketch, "E1149", {"start": v(-4.3, 17.6) * mm, "end": v(-4.09, 17.72) * mm});
            skLineSegment(sketch, "E1150", {"start": v(-4.09, 17.72) * mm, "end": v(-3.87, 17.85) * mm});
            skLineSegment(sketch, "E1151", {"start": v(-3.87, 17.85) * mm, "end": v(-3.7, 17.96) * mm});
            skLineSegment(sketch, "E1152", {"start": v(-3.7, 17.96) * mm, "end": v(-3.56, 18.05) * mm});
            skLineSegment(sketch, "E1153", {"start": v(-3.56, 18.05) * mm, "end": v(-3.5, 18.08) * mm});
            skLineSegment(sketch, "E1154", {"start": v(-3.5, 18.08) * mm, "end": v(-3.49, 18.1) * mm});
            skLineSegment(sketch, "E1155", {"start": v(-3.49, 18.1) * mm, "end": v(-3.45, 18.13) * mm});
            skLineSegment(sketch, "E1156", {"start": v(-3.45, 18.13) * mm, "end": v(-3.37, 18.27) * mm});
            skLineSegment(sketch, "E1157", {"start": v(-3.37, 18.27) * mm, "end": v(-3.34, 18.48) * mm});
            skLineSegment(sketch, "E1158", {"start": v(-3.34, 18.48) * mm, "end": v(-3.4, 18.68) * mm});
            skLineSegment(sketch, "E1159", {"start": v(-3.4, 18.68) * mm, "end": v(-3.51, 18.81) * mm});
            skLineSegment(sketch, "E1160", {"start": v(-3.51, 18.81) * mm, "end": v(-3.56, 18.84) * mm});
            skLineSegment(sketch, "E1161", {"start": v(-3.56, 18.84) * mm, "end": v(-3.58, 18.86) * mm});
            skLineSegment(sketch, "E1162", {"start": v(-3.58, 18.86) * mm, "end": v(-3.66, 18.9) * mm});
            skLineSegment(sketch, "E1163", {"start": v(-3.66, 18.9) * mm, "end": v(-3.78, 18.92) * mm});
            skLineSegment(sketch, "E1164", {"start": v(-3.78, 18.92) * mm, "end": v(-3.9, 18.92) * mm});
            skLineSegment(sketch, "E1165", {"start": v(-3.9, 18.92) * mm, "end": v(-3.97, 18.9) * mm});
            skLineSegment(sketch, "E1166", {"start": v(-3.97, 18.9) * mm, "end": v(-4, 18.9) * mm});
            skLineSegment(sketch, "E1167", {"start": v(3.6, 18.88) * mm, "end": v(3.57, 18.87) * mm});
            skLineSegment(sketch, "E1168", {"start": v(3.57, 18.87) * mm, "end": v(3.5, 18.82) * mm});
            skLineSegment(sketch, "E1169", {"start": v(3.5, 18.82) * mm, "end": v(3.41, 18.73) * mm});
            skLineSegment(sketch, "E1170", {"start": v(3.41, 18.73) * mm, "end": v(3.35, 18.63) * mm});
            skLineSegment(sketch, "E1171", {"start": v(3.35, 18.63) * mm, "end": v(3.32, 18.52) * mm});
            skLineSegment(sketch, "E1172", {"start": v(3.32, 18.52) * mm, "end": v(3.32, 18.4) * mm});
            skLineSegment(sketch, "E1173", {"start": v(3.32, 18.4) * mm, "end": v(3.34, 18.29) * mm});
            skLineSegment(sketch, "E1174", {"start": v(3.34, 18.29) * mm, "end": v(3.4, 18.18) * mm});
            skLineSegment(sketch, "E1175", {"start": v(3.4, 18.18) * mm, "end": v(3.46, 18.1) * mm});
            skLineSegment(sketch, "E1176", {"start": v(3.46, 18.1) * mm, "end": v(3.48, 18.08) * mm});
            skLineSegment(sketch, "E1177", {"start": v(3.48, 18.08) * mm, "end": v(3.5, 18.07) * mm});
            skLineSegment(sketch, "E1178", {"start": v(3.5, 18.07) * mm, "end": v(3.55, 18.03) * mm});
            skLineSegment(sketch, "E1179", {"start": v(3.55, 18.03) * mm, "end": v(3.7, 17.94) * mm});
            skLineSegment(sketch, "E1180", {"start": v(3.7, 17.94) * mm, "end": v(3.9, 17.82) * mm});
            skLineSegment(sketch, "E1181", {"start": v(3.9, 17.82) * mm, "end": v(4.12, 17.69) * mm});
            skLineSegment(sketch, "E1182", {"start": v(4.12, 17.69) * mm, "end": v(4.35, 17.56) * mm});
            skLineSegment(sketch, "E1183", {"start": v(4.35, 17.56) * mm, "end": v(4.57, 17.43) * mm});
            skLineSegment(sketch, "E1184", {"start": v(4.57, 17.43) * mm, "end": v(4.75, 17.34) * mm});
            skLineSegment(sketch, "E1185", {"start": v(4.75, 17.34) * mm, "end": v(4.84, 17.3) * mm});
            skLineSegment(sketch, "E1186", {"start": v(4.84, 17.3) * mm, "end": v(4.87, 17.28) * mm});
            skLineSegment(sketch, "E1187", {"start": v(4.87, 17.28) * mm, "end": v(4.89, 17.27) * mm});
            skLineSegment(sketch, "E1188", {"start": v(4.89, 17.27) * mm, "end": v(4.96, 17.24) * mm});
            skLineSegment(sketch, "E1189", {"start": v(4.96, 17.24) * mm, "end": v(5.04, 17.22) * mm});
            skLineSegment(sketch, "E1190", {"start": v(5.04, 17.22) * mm, "end": v(5.12, 17.22) * mm});
            skLineSegment(sketch, "E1191", {"start": v(5.12, 17.22) * mm, "end": v(5.18, 17.24) * mm});
            skLineSegment(sketch, "E1192", {"start": v(5.18, 17.24) * mm, "end": v(5.2, 17.24) * mm});
            skLineSegment(sketch, "E1193", {"start": v(5.2, 17.24) * mm, "end": v(5.24, 17.26) * mm});
            skLineSegment(sketch, "E1194", {"start": v(5.24, 17.26) * mm, "end": v(5.36, 17.32) * mm});
            skLineSegment(sketch, "E1195", {"start": v(5.36, 17.32) * mm, "end": v(5.47, 17.44) * mm});
            skLineSegment(sketch, "E1196", {"start": v(5.47, 17.44) * mm, "end": v(5.53, 17.59) * mm});
            skLineSegment(sketch, "E1197", {"start": v(5.53, 17.59) * mm, "end": v(5.54, 17.71) * mm});
            skLineSegment(sketch, "E1198", {"start": v(5.54, 17.71) * mm, "end": v(5.54, 17.76) * mm});
            skLineSegment(sketch, "E1199", {"start": v(5.54, 17.76) * mm, "end": v(5.54, 17.79) * mm});
            skLineSegment(sketch, "E1200", {"start": v(5.54, 17.79) * mm, "end": v(5.51, 17.88) * mm});
            skLineSegment(sketch, "E1201", {"start": v(5.51, 17.88) * mm, "end": v(5.46, 17.98) * mm});
            skLineSegment(sketch, "E1202", {"start": v(5.46, 17.98) * mm, "end": v(5.37, 18.08) * mm});
            skLineSegment(sketch, "E1203", {"start": v(5.37, 18.08) * mm, "end": v(5.28, 18.15) * mm});
            skLineSegment(sketch, "E1204", {"start": v(5.28, 18.15) * mm, "end": v(5.24, 18.17) * mm});
            skLineSegment(sketch, "E1205", {"start": v(5.24, 18.17) * mm, "end": v(5.2, 18.2) * mm});
            skLineSegment(sketch, "E1206", {"start": v(5.2, 18.2) * mm, "end": v(5.1, 18.26) * mm});
            skLineSegment(sketch, "E1207", {"start": v(5.1, 18.26) * mm, "end": v(4.92, 18.36) * mm});
            skLineSegment(sketch, "E1208", {"start": v(4.92, 18.36) * mm, "end": v(4.72, 18.47) * mm});
            skLineSegment(sketch, "E1209", {"start": v(4.72, 18.47) * mm, "end": v(4.52, 18.59) * mm});
            skLineSegment(sketch, "E1210", {"start": v(4.52, 18.59) * mm, "end": v(4.33, 18.7) * mm});
            skLineSegment(sketch, "E1211", {"start": v(4.33, 18.7) * mm, "end": v(4.17, 18.79) * mm});
            skLineSegment(sketch, "E1212", {"start": v(4.17, 18.79) * mm, "end": v(4.04, 18.85) * mm});
            skLineSegment(sketch, "E1213", {"start": v(4.04, 18.85) * mm, "end": v(4, 18.88) * mm});
            skLineSegment(sketch, "E1214", {"start": v(4, 18.88) * mm, "end": v(3.97, 18.89) * mm});
            skLineSegment(sketch, "E1215", {"start": v(3.97, 18.89) * mm, "end": v(3.94, 18.9) * mm});
            skLineSegment(sketch, "E1216", {"start": v(3.94, 18.9) * mm, "end": v(3.79, 18.92) * mm});
            skLineSegment(sketch, "E1217", {"start": v(3.79, 18.92) * mm, "end": v(3.63, 18.9) * mm});
            skLineSegment(sketch, "E1218", {"start": v(3.63, 18.9) * mm, "end": v(3.6, 18.88) * mm});
            skLineSegment(sketch, "E1219", {"start": v(-2.4, 17.27) * mm, "end": v(-2.41, 17.26) * mm});
            skLineSegment(sketch, "E1220", {"start": v(-2.41, 17.26) * mm, "end": v(-2.45, 17.25) * mm});
            skLineSegment(sketch, "E1221", {"start": v(-2.45, 17.25) * mm, "end": v(-2.5, 17.22) * mm});
            skLineSegment(sketch, "E1222", {"start": v(-2.5, 17.22) * mm, "end": v(-2.53, 17.18) * mm});
            skLineSegment(sketch, "E1223", {"start": v(-2.53, 17.18) * mm, "end": v(-2.56, 17.16) * mm});
            skLineSegment(sketch, "E1224", {"start": v(-2.56, 17.16) * mm, "end": v(-2.57, 17.15) * mm});
            skLineSegment(sketch, "E1225", {"start": v(-2.57, 17.15) * mm, "end": v(-2.58, 17.14) * mm});
            skLineSegment(sketch, "E1226", {"start": v(-2.58, 17.14) * mm, "end": v(-2.62, 17.08) * mm});
            skLineSegment(sketch, "E1227", {"start": v(-2.62, 17.08) * mm, "end": v(-2.7, 16.93) * mm});
            skLineSegment(sketch, "E1228", {"start": v(-2.7, 16.93) * mm, "end": v(-2.83, 16.74) * mm});
            skLineSegment(sketch, "E1229", {"start": v(-2.83, 16.74) * mm, "end": v(-2.96, 16.5) * mm});
            skLineSegment(sketch, "E1230", {"start": v(-2.96, 16.5) * mm, "end": v(-3.1, 16.28) * mm});
            skLineSegment(sketch, "E1231", {"start": v(-3.1, 16.28) * mm, "end": v(-3.22, 16.06) * mm});
            skLineSegment(sketch, "E1232", {"start": v(-3.22, 16.06) * mm, "end": v(-3.31, 15.88) * mm});
            skLineSegment(sketch, "E1233", {"start": v(-3.31, 15.88) * mm, "end": v(-3.36, 15.8) * mm});
            skLineSegment(sketch, "E1234", {"start": v(-3.36, 15.8) * mm, "end": v(-3.37, 15.77) * mm});
            skLineSegment(sketch, "E1235", {"start": v(-3.37, 15.77) * mm, "end": v(-3.38, 15.74) * mm});
            skLineSegment(sketch, "E1236", {"start": v(-3.38, 15.74) * mm, "end": v(-3.41, 15.67) * mm});
            skLineSegment(sketch, "E1237", {"start": v(-3.41, 15.67) * mm, "end": v(-3.43, 15.6) * mm});
            skLineSegment(sketch, "E1238", {"start": v(-3.43, 15.6) * mm, "end": v(-3.43, 15.51) * mm});
            skLineSegment(sketch, "E1239", {"start": v(-3.43, 15.51) * mm, "end": v(-3.41, 15.45) * mm});
            skLineSegment(sketch, "E1240", {"start": v(-3.41, 15.45) * mm, "end": v(-3.4, 15.43) * mm});
            skLineSegment(sketch, "E1241", {"start": v(-3.4, 15.43) * mm, "end": v(-3.4, 15.39) * mm});
            skLineSegment(sketch, "E1242", {"start": v(-3.4, 15.39) * mm, "end": v(-3.32, 15.28) * mm});
            skLineSegment(sketch, "E1243", {"start": v(-3.32, 15.28) * mm, "end": v(-3.2, 15.16) * mm});
            skLineSegment(sketch, "E1244", {"start": v(-3.2, 15.16) * mm, "end": v(-3.06, 15.1) * mm});
            skLineSegment(sketch, "E1245", {"start": v(-3.06, 15.1) * mm, "end": v(-2.93, 15.09) * mm});
            skLineSegment(sketch, "E1246", {"start": v(-2.93, 15.09) * mm, "end": v(-2.9, 15.1) * mm});
            skLineSegment(sketch, "E1247", {"start": v(-2.9, 15.1) * mm, "end": v(-2.86, 15.1) * mm});
            skLineSegment(sketch, "E1248", {"start": v(-2.86, 15.1) * mm, "end": v(-2.77, 15.12) * mm});
            skLineSegment(sketch, "E1249", {"start": v(-2.77, 15.12) * mm, "end": v(-2.66, 15.17) * mm});
            skLineSegment(sketch, "E1250", {"start": v(-2.66, 15.17) * mm, "end": v(-2.57, 15.26) * mm});
            skLineSegment(sketch, "E1251", {"start": v(-2.57, 15.26) * mm, "end": v(-2.5, 15.35) * mm});
            skLineSegment(sketch, "E1252", {"start": v(-2.5, 15.35) * mm, "end": v(-2.48, 15.39) * mm});
            skLineSegment(sketch, "E1253", {"start": v(-2.48, 15.39) * mm, "end": v(-2.46, 15.42) * mm});
            skLineSegment(sketch, "E1254", {"start": v(-2.46, 15.42) * mm, "end": v(-2.4, 15.53) * mm});
            skLineSegment(sketch, "E1255", {"start": v(-2.4, 15.53) * mm, "end": v(-2.29, 15.71) * mm});
            skLineSegment(sketch, "E1256", {"start": v(-2.29, 15.71) * mm, "end": v(-2.18, 15.9) * mm});
            skLineSegment(sketch, "E1257", {"start": v(-2.18, 15.9) * mm, "end": v(-2.06, 16.1) * mm});
            skLineSegment(sketch, "E1258", {"start": v(-2.06, 16.1) * mm, "end": v(-1.95, 16.3) * mm});
            skLineSegment(sketch, "E1259", {"start": v(-1.95, 16.3) * mm, "end": v(-1.86, 16.46) * mm});
            skLineSegment(sketch, "E1260", {"start": v(-1.86, 16.46) * mm, "end": v(-1.8, 16.59) * mm});
            skLineSegment(sketch, "E1261", {"start": v(-1.8, 16.59) * mm, "end": v(-1.77, 16.64) * mm});
            skLineSegment(sketch, "E1262", {"start": v(-1.77, 16.64) * mm, "end": v(-1.76, 16.66) * mm});
            skLineSegment(sketch, "E1263", {"start": v(-1.76, 16.66) * mm, "end": v(-1.75, 16.68) * mm});
            skLineSegment(sketch, "E1264", {"start": v(-1.75, 16.68) * mm, "end": v(-1.73, 16.75) * mm});
            skLineSegment(sketch, "E1265", {"start": v(-1.73, 16.75) * mm, "end": v(-1.72, 16.84) * mm});
            skLineSegment(sketch, "E1266", {"start": v(-1.72, 16.84) * mm, "end": v(-1.73, 16.93) * mm});
            skLineSegment(sketch, "E1267", {"start": v(-1.73, 16.93) * mm, "end": v(-1.76, 17) * mm});
            skLineSegment(sketch, "E1268", {"start": v(-1.76, 17) * mm, "end": v(-1.77, 17.02) * mm});
            skLineSegment(sketch, "E1269", {"start": v(-1.77, 17.02) * mm, "end": v(-1.79, 17.07) * mm});
            skLineSegment(sketch, "E1270", {"start": v(-1.79, 17.07) * mm, "end": v(-1.88, 17.18) * mm});
            skLineSegment(sketch, "E1271", {"start": v(-1.88, 17.18) * mm, "end": v(-2.03, 17.28) * mm});
            skLineSegment(sketch, "E1272", {"start": v(-2.03, 17.28) * mm, "end": v(-2.21, 17.31) * mm});
            skLineSegment(sketch, "E1273", {"start": v(-2.21, 17.31) * mm, "end": v(-2.36, 17.29) * mm});
            skLineSegment(sketch, "E1274", {"start": v(-2.36, 17.29) * mm, "end": v(-2.4, 17.27) * mm});
            skLineSegment(sketch, "E1275", {"start": v(2.03, 17.29) * mm, "end": v(2.02, 17.29) * mm});
            skLineSegment(sketch, "E1276", {"start": v(2.02, 17.29) * mm, "end": v(2, 17.27) * mm});
            skLineSegment(sketch, "E1277", {"start": v(2, 17.27) * mm, "end": v(1.94, 17.24) * mm});
            skLineSegment(sketch, "E1278", {"start": v(1.94, 17.24) * mm, "end": v(1.9, 17.2) * mm});
            skLineSegment(sketch, "E1279", {"start": v(1.9, 17.2) * mm, "end": v(1.86, 17.18) * mm});
            skLineSegment(sketch, "E1280", {"start": v(1.86, 17.18) * mm, "end": v(1.85, 17.17) * mm});
            skLineSegment(sketch, "E1281", {"start": v(1.85, 17.17) * mm, "end": v(1.83, 17.14) * mm});
            skLineSegment(sketch, "E1282", {"start": v(1.83, 17.14) * mm, "end": v(1.76, 17.05) * mm});
            skLineSegment(sketch, "E1283", {"start": v(1.76, 17.05) * mm, "end": v(1.71, 16.92) * mm});
            skLineSegment(sketch, "E1284", {"start": v(1.71, 16.92) * mm, "end": v(1.7, 16.8) * mm});
            skLineSegment(sketch, "E1285", {"start": v(1.7, 16.8) * mm, "end": v(1.72, 16.69) * mm});
            skLineSegment(sketch, "E1286", {"start": v(1.72, 16.69) * mm, "end": v(1.74, 16.66) * mm});
            skLineSegment(sketch, "E1287", {"start": v(1.74, 16.66) * mm, "end": v(1.75, 16.64) * mm});
            skLineSegment(sketch, "E1288", {"start": v(1.75, 16.64) * mm, "end": v(1.78, 16.57) * mm});
            skLineSegment(sketch, "E1289", {"start": v(1.78, 16.57) * mm, "end": v(1.87, 16.42) * mm});
            skLineSegment(sketch, "E1290", {"start": v(1.87, 16.42) * mm, "end": v(1.98, 16.21) * mm});
            skLineSegment(sketch, "E1291", {"start": v(1.98, 16.21) * mm, "end": v(2.11, 15.99) * mm});
            skLineSegment(sketch, "E1292", {"start": v(2.11, 15.99) * mm, "end": v(2.25, 15.76) * mm});
            skLineSegment(sketch, "E1293", {"start": v(2.25, 15.76) * mm, "end": v(2.37, 15.55) * mm});
            skLineSegment(sketch, "E1294", {"start": v(2.37, 15.55) * mm, "end": v(2.47, 15.38) * mm});
            skLineSegment(sketch, "E1295", {"start": v(2.47, 15.38) * mm, "end": v(2.51, 15.31) * mm});
            skLineSegment(sketch, "E1296", {"start": v(2.51, 15.31) * mm, "end": v(2.53, 15.3) * mm});
            skLineSegment(sketch, "E1297", {"start": v(2.53, 15.3) * mm, "end": v(2.55, 15.26) * mm});
            skLineSegment(sketch, "E1298", {"start": v(2.55, 15.26) * mm, "end": v(2.64, 15.17) * mm});
            skLineSegment(sketch, "E1299", {"start": v(2.64, 15.17) * mm, "end": v(2.78, 15.1) * mm});
            skLineSegment(sketch, "E1300", {"start": v(2.78, 15.1) * mm, "end": v(2.92, 15.09) * mm});
            skLineSegment(sketch, "E1301", {"start": v(2.92, 15.09) * mm, "end": v(3.07, 15.11) * mm});
            skLineSegment(sketch, "E1302", {"start": v(3.07, 15.11) * mm, "end": v(3.2, 15.17) * mm});
            skLineSegment(sketch, "E1303", {"start": v(3.2, 15.17) * mm, "end": v(3.3, 15.27) * mm});
            skLineSegment(sketch, "E1304", {"start": v(3.3, 15.27) * mm, "end": v(3.38, 15.4) * mm});
            skLineSegment(sketch, "E1305", {"start": v(3.38, 15.4) * mm, "end": v(3.4, 15.53) * mm});
            skLineSegment(sketch, "E1306", {"start": v(3.4, 15.53) * mm, "end": v(3.4, 15.57) * mm});
            skLineSegment(sketch, "E1307", {"start": v(3.4, 15.57) * mm, "end": v(3.4, 15.59) * mm});
            skLineSegment(sketch, "E1308", {"start": v(3.4, 15.59) * mm, "end": v(3.38, 15.69) * mm});
            skLineSegment(sketch, "E1309", {"start": v(3.38, 15.69) * mm, "end": v(3.35, 15.79) * mm});
            skLineSegment(sketch, "E1310", {"start": v(3.35, 15.79) * mm, "end": v(3.34, 15.8) * mm});
            skLineSegment(sketch, "E1311", {"start": v(3.34, 15.8) * mm, "end": v(3.32, 15.84) * mm});
            skLineSegment(sketch, "E1312", {"start": v(3.32, 15.84) * mm, "end": v(3.27, 15.93) * mm});
            skLineSegment(sketch, "E1313", {"start": v(3.27, 15.93) * mm, "end": v(3.17, 16.12) * mm});
            skLineSegment(sketch, "E1314", {"start": v(3.17, 16.12) * mm, "end": v(3.05, 16.33) * mm});
            skLineSegment(sketch, "E1315", {"start": v(3.05, 16.33) * mm, "end": v(2.92, 16.55) * mm});
            skLineSegment(sketch, "E1316", {"start": v(2.92, 16.55) * mm, "end": v(2.8, 16.77) * mm});
            skLineSegment(sketch, "E1317", {"start": v(2.8, 16.77) * mm, "end": v(2.68, 16.95) * mm});
            skLineSegment(sketch, "E1318", {"start": v(2.68, 16.95) * mm, "end": v(2.6, 17.09) * mm});
            skLineSegment(sketch, "E1319", {"start": v(2.6, 17.09) * mm, "end": v(2.56, 17.14) * mm});
            skLineSegment(sketch, "E1320", {"start": v(2.56, 17.14) * mm, "end": v(2.55, 17.15) * mm});
            skLineSegment(sketch, "E1321", {"start": v(2.55, 17.15) * mm, "end": v(2.53, 17.18) * mm});
            skLineSegment(sketch, "E1322", {"start": v(2.53, 17.18) * mm, "end": v(2.44, 17.24) * mm});
            skLineSegment(sketch, "E1323", {"start": v(2.44, 17.24) * mm, "end": v(2.32, 17.3) * mm});
            skLineSegment(sketch, "E1324", {"start": v(2.32, 17.3) * mm, "end": v(2.18, 17.31) * mm});
            skLineSegment(sketch, "E1325", {"start": v(2.18, 17.31) * mm, "end": v(2.07, 17.3) * mm});
            skLineSegment(sketch, "E1326", {"start": v(2.07, 17.3) * mm, "end": v(2.03, 17.29) * mm});
            skLineSegment(sketch, "E1327", {"start": v(-0.2, 16.68) * mm, "end": v(-0.23, 16.67) * mm});
            skLineSegment(sketch, "E1328", {"start": v(-0.23, 16.67) * mm, "end": v(-0.28, 16.64) * mm});
            skLineSegment(sketch, "E1329", {"start": v(-0.28, 16.64) * mm, "end": v(-0.34, 16.6) * mm});
            skLineSegment(sketch, "E1330", {"start": v(-0.34, 16.6) * mm, "end": v(-0.4, 16.54) * mm});
            skLineSegment(sketch, "E1331", {"start": v(-0.4, 16.54) * mm, "end": v(-0.43, 16.48) * mm});
            skLineSegment(sketch, "E1332", {"start": v(-0.43, 16.48) * mm, "end": v(-0.44, 16.46) * mm});
            skLineSegment(sketch, "E1333", {"start": v(-0.44, 16.46) * mm, "end": v(-0.44, 16.45) * mm});
            skLineSegment(sketch, "E1334", {"start": v(-0.44, 16.45) * mm, "end": v(-0.46, 16.43) * mm});
            skLineSegment(sketch, "E1335", {"start": v(-0.46, 16.43) * mm, "end": v(-0.47, 16.39) * mm});
            skLineSegment(sketch, "E1336", {"start": v(-0.47, 16.39) * mm, "end": v(-0.48, 16.34) * mm});
            skLineSegment(sketch, "E1337", {"start": v(-0.48, 16.34) * mm, "end": v(-0.49, 16.27) * mm});
            skLineSegment(sketch, "E1338", {"start": v(-0.49, 16.27) * mm, "end": v(-0.5, 16.17) * mm});
            skLineSegment(sketch, "E1339", {"start": v(-0.5, 16.17) * mm, "end": v(-0.5, 16.04) * mm});
            skLineSegment(sketch, "E1340", {"start": v(-0.5, 16.04) * mm, "end": v(-0.5, 15.87) * mm});
            skLineSegment(sketch, "E1341", {"start": v(-0.5, 15.87) * mm, "end": v(-0.5, 15.7) * mm});
            skLineSegment(sketch, "E1342", {"start": v(-0.5, 15.7) * mm, "end": v(-0.5, 15.64) * mm});
            skLineSegment(sketch, "E1343", {"start": v(-0.5, 15.64) * mm, "end": v(-0.5, 15.57) * mm});
            skLineSegment(sketch, "E1344", {"start": v(-0.5, 15.57) * mm, "end": v(-0.5, 15.34) * mm});
            skLineSegment(sketch, "E1345", {"start": v(-0.5, 15.34) * mm, "end": v(-0.5, 15.1) * mm});
            skLineSegment(sketch, "E1346", {"start": v(-0.5, 15.1) * mm, "end": v(-0.5, 14.93) * mm});
            skLineSegment(sketch, "E1347", {"start": v(-0.5, 14.93) * mm, "end": v(-0.5, 14.8) * mm});
            skLineSegment(sketch, "E1348", {"start": v(-0.5, 14.8) * mm, "end": v(-0.48, 14.7) * mm});
            skLineSegment(sketch, "E1349", {"start": v(-0.48, 14.7) * mm, "end": v(-0.46, 14.62) * mm});
            skLineSegment(sketch, "E1350", {"start": v(-0.46, 14.62) * mm, "end": v(-0.43, 14.56) * mm});
            skLineSegment(sketch, "E1351", {"start": v(-0.43, 14.56) * mm, "end": v(-0.4, 14.52) * mm});
            skLineSegment(sketch, "E1352", {"start": v(-0.4, 14.52) * mm, "end": v(-0.4, 14.5) * mm});
            skLineSegment(sketch, "E1353", {"start": v(-0.4, 14.5) * mm, "end": v(-0.38, 14.48) * mm});
            skLineSegment(sketch, "E1354", {"start": v(-0.38, 14.48) * mm, "end": v(-0.32, 14.42) * mm});
            skLineSegment(sketch, "E1355", {"start": v(-0.32, 14.42) * mm, "end": v(-0.22, 14.35) * mm});
            skLineSegment(sketch, "E1356", {"start": v(-0.22, 14.35) * mm, "end": v(-0.11, 14.3) * mm});
            skLineSegment(sketch, "E1357", {"start": v(-0.11, 14.3) * mm, "end": v(-0.03, 14.29) * mm});
            skLineSegment(sketch, "E1358", {"start": v(-0.03, 14.29) * mm, "end": v(0, 14.29) * mm});
            skLineSegment(sketch, "E1359", {"start": v(0, 14.29) * mm, "end": v(0.03, 14.3) * mm});
            skLineSegment(sketch, "E1360", {"start": v(0.03, 14.3) * mm, "end": v(0.13, 14.32) * mm});
            skLineSegment(sketch, "E1361", {"start": v(0.13, 14.32) * mm, "end": v(0.27, 14.4) * mm});
            skLineSegment(sketch, "E1362", {"start": v(0.27, 14.4) * mm, "end": v(0.39, 14.5) * mm});
            skLineSegment(sketch, "E1363", {"start": v(0.39, 14.5) * mm, "end": v(0.45, 14.6) * mm});
            skLineSegment(sketch, "E1364", {"start": v(0.45, 14.6) * mm, "end": v(0.46, 14.63) * mm});
            skLineSegment(sketch, "E1365", {"start": v(0.46, 14.63) * mm, "end": v(0.46, 14.64) * mm});
            skLineSegment(sketch, "E1366", {"start": v(0.46, 14.64) * mm, "end": v(0.46, 14.72) * mm});
            skLineSegment(sketch, "E1367", {"start": v(0.46, 14.72) * mm, "end": v(0.47, 14.92) * mm});
            skLineSegment(sketch, "E1368", {"start": v(0.47, 14.92) * mm, "end": v(0.47, 15.2) * mm});
            skLineSegment(sketch, "E1369", {"start": v(0.47, 15.2) * mm, "end": v(0.47, 15.45) * mm});
            skLineSegment(sketch, "E1370", {"start": v(0.47, 15.45) * mm, "end": v(0.47, 15.53) * mm});
            skLineSegment(sketch, "E1371", {"start": v(0.47, 15.53) * mm, "end": v(0.47, 15.6) * mm});
            skLineSegment(sketch, "E1372", {"start": v(0.47, 15.6) * mm, "end": v(0.47, 15.8) * mm});
            skLineSegment(sketch, "E1373", {"start": v(0.47, 15.8) * mm, "end": v(0.47, 16) * mm});
            skLineSegment(sketch, "E1374", {"start": v(0.47, 16) * mm, "end": v(0.47, 16.16) * mm});
            skLineSegment(sketch, "E1375", {"start": v(0.47, 16.16) * mm, "end": v(0.47, 16.27) * mm});
            skLineSegment(sketch, "E1376", {"start": v(0.47, 16.27) * mm, "end": v(0.46, 16.34) * mm});
            skLineSegment(sketch, "E1377", {"start": v(0.46, 16.34) * mm, "end": v(0.45, 16.4) * mm});
            skLineSegment(sketch, "E1378", {"start": v(0.45, 16.4) * mm, "end": v(0.44, 16.43) * mm});
            skLineSegment(sketch, "E1379", {"start": v(0.44, 16.43) * mm, "end": v(0.42, 16.46) * mm});
            skLineSegment(sketch, "E1380", {"start": v(0.42, 16.46) * mm, "end": v(0.42, 16.47) * mm});
            skLineSegment(sketch, "E1381", {"start": v(0.42, 16.47) * mm, "end": v(0.4, 16.5) * mm});
            skLineSegment(sketch, "E1382", {"start": v(0.4, 16.5) * mm, "end": v(0.3, 16.6) * mm});
            skLineSegment(sketch, "E1383", {"start": v(0.3, 16.6) * mm, "end": v(0.14, 16.69) * mm});
            skLineSegment(sketch, "E1384", {"start": v(0.14, 16.69) * mm, "end": v(-0.03, 16.72) * mm});
            skLineSegment(sketch, "E1385", {"start": v(-0.03, 16.72) * mm, "end": v(-0.17, 16.7) * mm});
            skLineSegment(sketch, "E1386", {"start": v(-0.17, 16.7) * mm, "end": v(-0.2, 16.68) * mm});
            skSolve(sketch);
        }
        {
            var Q0;
            Q0=makeQuery(id+"F1.imprint","IMPRINT",FACE,{"disambiguationData":[TD([[makeQuery(id+"F1.imprint","IMPRINT",EDGE,{"derivedFrom":sQuery(id+"F1.wireOp",EDGE,"E6")}),-1.0]])]});
            var sketch = newSketch(context, id + "F4", { "sketchPlane" : qUnion([Q0])});
            skLineSegment(sketch, "E1387", {"start": v(1.6, -30.98) * mm, "end": v(1.5, -30.99) * mm});
            skLineSegment(sketch, "E1388", {"start": v(1.5, -30.99) * mm, "end": v(1.19, -31.03) * mm});
            skLineSegment(sketch, "E1389", {"start": v(1.19, -31.03) * mm, "end": v(0.78, -31.1) * mm});
            skLineSegment(sketch, "E1390", {"start": v(0.78, -31.1) * mm, "end": v(0.39, -31.2) * mm});
            skLineSegment(sketch, "E1391", {"start": v(0.39, -31.2) * mm, "end": v(0, -31.32) * mm});
            skLineSegment(sketch, "E1392", {"start": v(0, -31.32) * mm, "end": v(-0.37, -31.46) * mm});
            skLineSegment(sketch, "E1393", {"start": v(-0.37, -31.46) * mm, "end": v(-0.74, -31.63) * mm});
            skLineSegment(sketch, "E1394", {"start": v(-0.74, -31.63) * mm, "end": v(-1.1, -31.82) * mm});
            skLineSegment(sketch, "E1395", {"start": v(-1.1, -31.82) * mm, "end": v(-1.36, -31.98) * mm});
            skLineSegment(sketch, "E1396", {"start": v(-1.36, -31.98) * mm, "end": v(-1.45, -32.04) * mm});
            skLineSegment(sketch, "E1397", {"start": v(-1.45, -32.04) * mm, "end": v(-1.55, -32.11) * mm});
            skLineSegment(sketch, "E1398", {"start": v(-1.55, -32.11) * mm, "end": v(-1.87, -32.35) * mm});
            skLineSegment(sketch, "E1399", {"start": v(-1.87, -32.35) * mm, "end": v(-2.26, -32.69) * mm});
            skLineSegment(sketch, "E1400", {"start": v(-2.26, -32.69) * mm, "end": v(-2.62, -33.06) * mm});
            skLineSegment(sketch, "E1401", {"start": v(-2.62, -33.06) * mm, "end": v(-2.95, -33.46) * mm});
            skLineSegment(sketch, "E1402", {"start": v(-2.95, -33.46) * mm, "end": v(-3.25, -33.89) * mm});
            skLineSegment(sketch, "E1403", {"start": v(-3.25, -33.89) * mm, "end": v(-3.52, -34.34) * mm});
            skLineSegment(sketch, "E1404", {"start": v(-3.52, -34.34) * mm, "end": v(-3.74, -34.8) * mm});
            skLineSegment(sketch, "E1405", {"start": v(-3.74, -34.8) * mm, "end": v(-3.89, -35.17) * mm});
            skLineSegment(sketch, "E1406", {"start": v(-3.89, -35.17) * mm, "end": v(-3.93, -35.3) * mm});
            skLineSegment(sketch, "E1407", {"start": v(-3.93, -35.3) * mm, "end": v(-3.97, -35.43) * mm});
            skLineSegment(sketch, "E1408", {"start": v(-3.97, -35.43) * mm, "end": v(-4.09, -35.84) * mm});
            skLineSegment(sketch, "E1409", {"start": v(-4.09, -35.84) * mm, "end": v(-4.2, -36.39) * mm});
            skLineSegment(sketch, "E1410", {"start": v(-4.2, -36.39) * mm, "end": v(-4.25, -36.94) * mm});
            skLineSegment(sketch, "E1411", {"start": v(-4.25, -36.94) * mm, "end": v(-4.26, -37.5) * mm});
            skLineSegment(sketch, "E1412", {"start": v(-4.26, -37.5) * mm, "end": v(-4.22, -38.05) * mm});
            skLineSegment(sketch, "E1413", {"start": v(-4.22, -38.05) * mm, "end": v(-4.13, -38.6) * mm});
            skLineSegment(sketch, "E1414", {"start": v(-4.13, -38.6) * mm, "end": v(-4, -39.14) * mm});
            skLineSegment(sketch, "E1415", {"start": v(-4, -39.14) * mm, "end": v(-3.86, -39.55) * mm});
            skLineSegment(sketch, "E1416", {"start": v(-3.86, -39.55) * mm, "end": v(-3.8, -39.68) * mm});
            skLineSegment(sketch, "E1417", {"start": v(-3.8, -39.68) * mm, "end": v(-3.8, -39.7) * mm});
            skLineSegment(sketch, "E1418", {"start": v(-3.8, -39.7) * mm, "end": v(-3.77, -39.78) * mm});
            skLineSegment(sketch, "E1419", {"start": v(-3.77, -39.78) * mm, "end": v(-3.72, -39.9) * mm});
            skLineSegment(sketch, "E1420", {"start": v(-3.72, -39.9) * mm, "end": v(-3.66, -40.01) * mm});
            skLineSegment(sketch, "E1421", {"start": v(-3.66, -40.01) * mm, "end": v(-3.6, -40.14) * mm});
            skLineSegment(sketch, "E1422", {"start": v(-3.6, -40.14) * mm, "end": v(-3.53, -40.27) * mm});
            skLineSegment(sketch, "E1423", {"start": v(-3.53, -40.27) * mm, "end": v(-3.47, -40.4) * mm});
            skLineSegment(sketch, "E1424", {"start": v(-3.47, -40.4) * mm, "end": v(-3.4, -40.5) * mm});
            skLineSegment(sketch, "E1425", {"start": v(-3.4, -40.5) * mm, "end": v(-3.36, -40.58) * mm});
            skLineSegment(sketch, "E1426", {"start": v(-3.36, -40.58) * mm, "end": v(-3.35, -40.6) * mm});
            skLineSegment(sketch, "E1427", {"start": v(-3.35, -40.6) * mm, "end": v(-3.3, -40.68) * mm});
            skLineSegment(sketch, "E1428", {"start": v(-3.3, -40.68) * mm, "end": v(-3.16, -40.9) * mm});
            skLineSegment(sketch, "E1429", {"start": v(-3.16, -40.9) * mm, "end": v(-2.95, -41.19) * mm});
            skLineSegment(sketch, "E1430", {"start": v(-2.95, -41.19) * mm, "end": v(-2.73, -41.46) * mm});
            skLineSegment(sketch, "E1431", {"start": v(-2.73, -41.46) * mm, "end": v(-2.5, -41.72) * mm});
            skLineSegment(sketch, "E1432", {"start": v(-2.5, -41.72) * mm, "end": v(-2.25, -41.96) * mm});
            skLineSegment(sketch, "E1433", {"start": v(-2.25, -41.96) * mm, "end": v(-1.99, -42.2) * mm});
            skLineSegment(sketch, "E1434", {"start": v(-1.99, -42.2) * mm, "end": v(-1.71, -42.41) * mm});
            skLineSegment(sketch, "E1435", {"start": v(-1.71, -42.41) * mm, "end": v(-1.5, -42.56) * mm});
            skLineSegment(sketch, "E1436", {"start": v(-1.5, -42.56) * mm, "end": v(-1.43, -42.61) * mm});
            skLineSegment(sketch, "E1437", {"start": v(-1.43, -42.61) * mm, "end": v(-1.3, -42.7) * mm});
            skLineSegment(sketch, "E1438", {"start": v(-1.3, -42.7) * mm, "end": v(-0.94, -42.9) * mm});
            skLineSegment(sketch, "E1439", {"start": v(-0.94, -42.9) * mm, "end": v(-0.43, -43.15) * mm});
            skLineSegment(sketch, "E1440", {"start": v(-0.43, -43.15) * mm, "end": v(0.1, -43.35) * mm});
            skLineSegment(sketch, "E1441", {"start": v(0.1, -43.35) * mm, "end": v(0.64, -43.5) * mm});
            skLineSegment(sketch, "E1442", {"start": v(0.64, -43.5) * mm, "end": v(1.2, -43.61) * mm});
            skLineSegment(sketch, "E1443", {"start": v(1.2, -43.61) * mm, "end": v(1.75, -43.67) * mm});
            skLineSegment(sketch, "E1444", {"start": v(1.75, -43.67) * mm, "end": v(2.32, -43.67) * mm});
            skLineSegment(sketch, "E1445", {"start": v(2.32, -43.67) * mm, "end": v(2.75, -43.65) * mm});
            skLineSegment(sketch, "E1446", {"start": v(2.75, -43.65) * mm, "end": v(2.89, -43.63) * mm});
            skLineSegment(sketch, "E1447", {"start": v(2.89, -43.63) * mm, "end": v(2.95, -43.62) * mm});
            skLineSegment(sketch, "E1448", {"start": v(2.95, -43.62) * mm, "end": v(3.25, -43.57) * mm});
            skLineSegment(sketch, "E1449", {"start": v(3.25, -43.57) * mm, "end": v(3.57, -43.5) * mm});
            skLineSegment(sketch, "E1450", {"start": v(3.57, -43.5) * mm, "end": v(3.63, -43.49) * mm});
            skLineSegment(sketch, "E1451", {"start": v(3.63, -43.49) * mm, "end": v(3.66, -43.48) * mm});
            skLineSegment(sketch, "E1452", {"start": v(3.66, -43.48) * mm, "end": v(3.76, -43.45) * mm});
            skLineSegment(sketch, "E1453", {"start": v(3.76, -43.45) * mm, "end": v(3.88, -43.42) * mm});
            skLineSegment(sketch, "E1454", {"start": v(3.88, -43.42) * mm, "end": v(3.97, -43.4) * mm});
            skLineSegment(sketch, "E1455", {"start": v(3.97, -43.4) * mm, "end": v(4.04, -43.37) * mm});
            skLineSegment(sketch, "E1456", {"start": v(4.04, -43.37) * mm, "end": v(4.1, -43.34) * mm});
            skLineSegment(sketch, "E1457", {"start": v(4.1, -43.34) * mm, "end": v(4.14, -43.3) * mm});
            skLineSegment(sketch, "E1458", {"start": v(4.14, -43.3) * mm, "end": v(4.17, -43.27) * mm});
            skLineSegment(sketch, "E1459", {"start": v(4.17, -43.27) * mm, "end": v(4.2, -43.24) * mm});
            skLineSegment(sketch, "E1460", {"start": v(4.2, -43.24) * mm, "end": v(4.2, -43.23) * mm});
            skLineSegment(sketch, "E1461", {"start": v(4.2, -43.23) * mm, "end": v(4.21, -43.21) * mm});
            skLineSegment(sketch, "E1462", {"start": v(4.21, -43.21) * mm, "end": v(4.24, -43.17) * mm});
            skLineSegment(sketch, "E1463", {"start": v(4.24, -43.17) * mm, "end": v(4.26, -43.1) * mm});
            skLineSegment(sketch, "E1464", {"start": v(4.26, -43.1) * mm, "end": v(4.27, -43.04) * mm});
            skLineSegment(sketch, "E1465", {"start": v(4.27, -43.04) * mm, "end": v(4.27, -42.99) * mm});
            skLineSegment(sketch, "E1466", {"start": v(4.27, -42.99) * mm, "end": v(4.27, -42.97) * mm});
            skLineSegment(sketch, "E1467", {"start": v(4.27, -42.97) * mm, "end": v(4.26, -42.95) * mm});
            skLineSegment(sketch, "E1468", {"start": v(4.26, -42.95) * mm, "end": v(4.26, -42.9) * mm});
            skLineSegment(sketch, "E1469", {"start": v(4.26, -42.9) * mm, "end": v(4.23, -42.83) * mm});
            skLineSegment(sketch, "E1470", {"start": v(4.23, -42.83) * mm, "end": v(4.2, -42.77) * mm});
            skLineSegment(sketch, "E1471", {"start": v(4.2, -42.77) * mm, "end": v(4.17, -42.73) * mm});
            skLineSegment(sketch, "E1472", {"start": v(4.17, -42.73) * mm, "end": v(4.15, -42.72) * mm});
            skLineSegment(sketch, "E1473", {"start": v(4.15, -42.72) * mm, "end": v(4.14, -42.7) * mm});
            skLineSegment(sketch, "E1474", {"start": v(4.14, -42.7) * mm, "end": v(4.1, -42.68) * mm});
            skLineSegment(sketch, "E1475", {"start": v(4.1, -42.68) * mm, "end": v(4.06, -42.65) * mm});
            skLineSegment(sketch, "E1476", {"start": v(4.06, -42.65) * mm, "end": v(4, -42.62) * mm});
            skLineSegment(sketch, "E1477", {"start": v(4, -42.62) * mm, "end": v(3.92, -42.6) * mm});
            skLineSegment(sketch, "E1478", {"start": v(3.92, -42.6) * mm, "end": v(3.9, -42.58) * mm});
            skLineSegment(sketch, "E1479", {"start": v(3.9, -42.58) * mm, "end": v(3.83, -42.56) * mm});
            skLineSegment(sketch, "E1480", {"start": v(3.83, -42.56) * mm, "end": v(3.63, -42.49) * mm});
            skLineSegment(sketch, "E1481", {"start": v(3.63, -42.49) * mm, "end": v(3.36, -42.38) * mm});
            skLineSegment(sketch, "E1482", {"start": v(3.36, -42.38) * mm, "end": v(3.1, -42.25) * mm});
            skLineSegment(sketch, "E1483", {"start": v(3.1, -42.25) * mm, "end": v(2.85, -42.11) * mm});
            skLineSegment(sketch, "E1484", {"start": v(2.85, -42.11) * mm, "end": v(2.6, -41.96) * mm});
            skLineSegment(sketch, "E1485", {"start": v(2.6, -41.96) * mm, "end": v(2.37, -41.8) * mm});
            skLineSegment(sketch, "E1486", {"start": v(2.37, -41.8) * mm, "end": v(2.14, -41.62) * mm});
            skLineSegment(sketch, "E1487", {"start": v(2.14, -41.62) * mm, "end": v(1.93, -41.44) * mm});
            skLineSegment(sketch, "E1488", {"start": v(1.93, -41.44) * mm, "end": v(1.72, -41.24) * mm});
            skLineSegment(sketch, "E1489", {"start": v(1.72, -41.24) * mm, "end": v(1.52, -41.03) * mm});
            skLineSegment(sketch, "E1490", {"start": v(1.52, -41.03) * mm, "end": v(1.34, -40.81) * mm});
            skLineSegment(sketch, "E1491", {"start": v(1.34, -40.81) * mm, "end": v(1.16, -40.58) * mm});
            skLineSegment(sketch, "E1492", {"start": v(1.16, -40.58) * mm, "end": v(1, -40.35) * mm});
            skLineSegment(sketch, "E1493", {"start": v(1, -40.35) * mm, "end": v(0.85, -40.1) * mm});
            skLineSegment(sketch, "E1494", {"start": v(0.85, -40.1) * mm, "end": v(0.7, -39.85) * mm});
            skLineSegment(sketch, "E1495", {"start": v(0.7, -39.85) * mm, "end": v(0.61, -39.65) * mm});
            skLineSegment(sketch, "E1496", {"start": v(0.61, -39.65) * mm, "end": v(0.58, -39.59) * mm});
            skLineSegment(sketch, "E1497", {"start": v(0.58, -39.59) * mm, "end": v(0.54, -39.49) * mm});
            skLineSegment(sketch, "E1498", {"start": v(0.54, -39.49) * mm, "end": v(0.42, -39.19) * mm});
            skLineSegment(sketch, "E1499", {"start": v(0.42, -39.19) * mm, "end": v(0.3, -38.78) * mm});
            skLineSegment(sketch, "E1500", {"start": v(0.3, -38.78) * mm, "end": v(0.2, -38.37) * mm});
            skLineSegment(sketch, "E1501", {"start": v(0.2, -38.37) * mm, "end": v(0.13, -37.96) * mm});
            skLineSegment(sketch, "E1502", {"start": v(0.13, -37.96) * mm, "end": v(0.1, -37.54) * mm});
            skLineSegment(sketch, "E1503", {"start": v(0.1, -37.54) * mm, "end": v(0.1, -37.11) * mm});
            skLineSegment(sketch, "E1504", {"start": v(0.1, -37.11) * mm, "end": v(0.13, -36.69) * mm});
            skLineSegment(sketch, "E1505", {"start": v(0.13, -36.69) * mm, "end": v(0.18, -36.37) * mm});
            skLineSegment(sketch, "E1506", {"start": v(0.18, -36.37) * mm, "end": v(0.2, -36.26) * mm});
            skLineSegment(sketch, "E1507", {"start": v(0.2, -36.26) * mm, "end": v(0.22, -36.16) * mm});
            skLineSegment(sketch, "E1508", {"start": v(0.22, -36.16) * mm, "end": v(0.3, -35.85) * mm});
            skLineSegment(sketch, "E1509", {"start": v(0.3, -35.85) * mm, "end": v(0.42, -35.45) * mm});
            skLineSegment(sketch, "E1510", {"start": v(0.42, -35.45) * mm, "end": v(0.58, -35.06) * mm});
            skLineSegment(sketch, "E1511", {"start": v(0.58, -35.06) * mm, "end": v(0.77, -34.68) * mm});
            skLineSegment(sketch, "E1512", {"start": v(0.77, -34.68) * mm, "end": v(0.98, -34.32) * mm});
            skLineSegment(sketch, "E1513", {"start": v(0.98, -34.32) * mm, "end": v(1.22, -33.97) * mm});
            skLineSegment(sketch, "E1514", {"start": v(1.22, -33.97) * mm, "end": v(1.5, -33.65) * mm});
            skLineSegment(sketch, "E1515", {"start": v(1.5, -33.65) * mm, "end": v(1.7, -33.41) * mm});
            skLineSegment(sketch, "E1516", {"start": v(1.7, -33.41) * mm, "end": v(1.79, -33.34) * mm});
            skLineSegment(sketch, "E1517", {"start": v(1.79, -33.34) * mm, "end": v(1.9, -33.23) * mm});
            skLineSegment(sketch, "E1518", {"start": v(1.9, -33.23) * mm, "end": v(2.25, -32.94) * mm});
            skLineSegment(sketch, "E1519", {"start": v(2.25, -32.94) * mm, "end": v(2.75, -32.6) * mm});
            skLineSegment(sketch, "E1520", {"start": v(2.75, -32.6) * mm, "end": v(3.28, -32.3) * mm});
            skLineSegment(sketch, "E1521", {"start": v(3.28, -32.3) * mm, "end": v(3.7, -32.12) * mm});
            skLineSegment(sketch, "E1522", {"start": v(3.7, -32.12) * mm, "end": v(3.85, -32.07) * mm});
            skLineSegment(sketch, "E1523", {"start": v(3.85, -32.07) * mm, "end": v(3.89, -32.06) * mm});
            skLineSegment(sketch, "E1524", {"start": v(3.89, -32.06) * mm, "end": v(3.98, -32.03) * mm});
            skLineSegment(sketch, "E1525", {"start": v(3.98, -32.03) * mm, "end": v(4.06, -32) * mm});
            skLineSegment(sketch, "E1526", {"start": v(4.06, -32) * mm, "end": v(4.1, -31.96) * mm});
            skLineSegment(sketch, "E1527", {"start": v(4.1, -31.96) * mm, "end": v(4.14, -31.93) * mm});
            skLineSegment(sketch, "E1528", {"start": v(4.14, -31.93) * mm, "end": v(4.15, -31.92) * mm});
            skLineSegment(sketch, "E1529", {"start": v(4.15, -31.92) * mm, "end": v(4.17, -31.9) * mm});
            skLineSegment(sketch, "E1530", {"start": v(4.17, -31.9) * mm, "end": v(4.2, -31.86) * mm});
            skLineSegment(sketch, "E1531", {"start": v(4.2, -31.86) * mm, "end": v(4.24, -31.8) * mm});
            skLineSegment(sketch, "E1532", {"start": v(4.24, -31.8) * mm, "end": v(4.26, -31.73) * mm});
            skLineSegment(sketch, "E1533", {"start": v(4.26, -31.73) * mm, "end": v(4.26, -31.66) * mm});
            skLineSegment(sketch, "E1534", {"start": v(4.26, -31.66) * mm, "end": v(4.26, -31.64) * mm});
            skLineSegment(sketch, "E1535", {"start": v(4.26, -31.64) * mm, "end": v(4.26, -31.62) * mm});
            skLineSegment(sketch, "E1536", {"start": v(4.26, -31.62) * mm, "end": v(4.26, -31.55) * mm});
            skLineSegment(sketch, "E1537", {"start": v(4.26, -31.55) * mm, "end": v(4.24, -31.47) * mm});
            skLineSegment(sketch, "E1538", {"start": v(4.24, -31.47) * mm, "end": v(4.2, -31.41) * mm});
            skLineSegment(sketch, "E1539", {"start": v(4.2, -31.41) * mm, "end": v(4.16, -31.37) * mm});
            skLineSegment(sketch, "E1540", {"start": v(4.16, -31.37) * mm, "end": v(4.15, -31.35) * mm});
            skLineSegment(sketch, "E1541", {"start": v(4.15, -31.35) * mm, "end": v(4.14, -31.34) * mm});
            skLineSegment(sketch, "E1542", {"start": v(4.14, -31.34) * mm, "end": v(4.1, -31.3) * mm});
            skLineSegment(sketch, "E1543", {"start": v(4.1, -31.3) * mm, "end": v(4.03, -31.27) * mm});
            skLineSegment(sketch, "E1544", {"start": v(4.03, -31.27) * mm, "end": v(3.93, -31.23) * mm});
            skLineSegment(sketch, "E1545", {"start": v(3.93, -31.23) * mm, "end": v(3.82, -31.2) * mm});
            skLineSegment(sketch, "E1546", {"start": v(3.82, -31.2) * mm, "end": v(3.78, -31.2) * mm});
            skLineSegment(sketch, "E1547", {"start": v(3.78, -31.2) * mm, "end": v(3.72, -31.18) * mm});
            skLineSegment(sketch, "E1548", {"start": v(3.72, -31.18) * mm, "end": v(3.54, -31.13) * mm});
            skLineSegment(sketch, "E1549", {"start": v(3.54, -31.13) * mm, "end": v(3.3, -31.08) * mm});
            skLineSegment(sketch, "E1550", {"start": v(3.3, -31.08) * mm, "end": v(3.04, -31.04) * mm});
            skLineSegment(sketch, "E1551", {"start": v(3.04, -31.04) * mm, "end": v(2.84, -31) * mm});
            skLineSegment(sketch, "E1552", {"start": v(2.84, -31) * mm, "end": v(2.78, -31) * mm});
            skLineSegment(sketch, "E1553", {"start": v(2.78, -31) * mm, "end": v(2.75, -31) * mm});
            skLineSegment(sketch, "E1554", {"start": v(2.75, -31) * mm, "end": v(2.67, -31) * mm});
            skLineSegment(sketch, "E1555", {"start": v(2.67, -31) * mm, "end": v(2.53, -30.98) * mm});
            skLineSegment(sketch, "E1556", {"start": v(2.53, -30.98) * mm, "end": v(2.37, -30.98) * mm});
            skLineSegment(sketch, "E1557", {"start": v(2.37, -30.98) * mm, "end": v(2.2, -30.97) * mm});
            skLineSegment(sketch, "E1558", {"start": v(2.2, -30.97) * mm, "end": v(2.01, -30.97) * mm});
            skLineSegment(sketch, "E1559", {"start": v(2.01, -30.97) * mm, "end": v(1.85, -30.97) * mm});
            skLineSegment(sketch, "E1560", {"start": v(1.85, -30.97) * mm, "end": v(1.7, -30.98) * mm});
            skLineSegment(sketch, "E1561", {"start": v(1.7, -30.98) * mm, "end": v(1.63, -30.98) * mm});
            skLineSegment(sketch, "E1562", {"start": v(1.63, -30.98) * mm, "end": v(1.6, -30.98) * mm});
            skLineSegment(sketch, "E1563", {"start": v(2.4, -31.78) * mm, "end": v(2.5, -31.8) * mm});
            skLineSegment(sketch, "E1564", {"start": v(2.5, -31.8) * mm, "end": v(2.43, -31.84) * mm});
            skLineSegment(sketch, "E1565", {"start": v(2.43, -31.84) * mm, "end": v(2.4, -31.85) * mm});
            skLineSegment(sketch, "E1566", {"start": v(2.4, -31.85) * mm, "end": v(2.34, -31.89) * mm});
            skLineSegment(sketch, "E1567", {"start": v(2.34, -31.89) * mm, "end": v(2.25, -31.94) * mm});
            skLineSegment(sketch, "E1568", {"start": v(2.25, -31.94) * mm, "end": v(2.15, -32.01) * mm});
            skLineSegment(sketch, "E1569", {"start": v(2.15, -32.01) * mm, "end": v(2.04, -32.08) * mm});
            skLineSegment(sketch, "E1570", {"start": v(2.04, -32.08) * mm, "end": v(1.94, -32.16) * mm});
            skLineSegment(sketch, "E1571", {"start": v(1.94, -32.16) * mm, "end": v(1.84, -32.23) * mm});
            skLineSegment(sketch, "E1572", {"start": v(1.84, -32.23) * mm, "end": v(1.74, -32.3) * mm});
            skLineSegment(sketch, "E1573", {"start": v(1.74, -32.3) * mm, "end": v(1.67, -32.35) * mm});
            skLineSegment(sketch, "E1574", {"start": v(1.67, -32.35) * mm, "end": v(1.65, -32.37) * mm});
            skLineSegment(sketch, "E1575", {"start": v(1.65, -32.37) * mm, "end": v(1.59, -32.42) * mm});
            skLineSegment(sketch, "E1576", {"start": v(1.59, -32.42) * mm, "end": v(1.4, -32.59) * mm});
            skLineSegment(sketch, "E1577", {"start": v(1.4, -32.59) * mm, "end": v(1.16, -32.81) * mm});
            skLineSegment(sketch, "E1578", {"start": v(1.16, -32.81) * mm, "end": v(0.94, -33.05) * mm});
            skLineSegment(sketch, "E1579", {"start": v(0.94, -33.05) * mm, "end": v(0.72, -33.3) * mm});
            skLineSegment(sketch, "E1580", {"start": v(0.72, -33.3) * mm, "end": v(0.53, -33.55) * mm});
            skLineSegment(sketch, "E1581", {"start": v(0.53, -33.55) * mm, "end": v(0.34, -33.82) * mm});
            skLineSegment(sketch, "E1582", {"start": v(0.34, -33.82) * mm, "end": v(0.17, -34.1) * mm});
            skLineSegment(sketch, "E1583", {"start": v(0.17, -34.1) * mm, "end": v(0.01, -34.37) * mm});
            skLineSegment(sketch, "E1584", {"start": v(0.01, -34.37) * mm, "end": v(-0.13, -34.66) * mm});
            skLineSegment(sketch, "E1585", {"start": v(-0.13, -34.66) * mm, "end": v(-0.26, -34.96) * mm});
            skLineSegment(sketch, "E1586", {"start": v(-0.26, -34.96) * mm, "end": v(-0.37, -35.27) * mm});
            skLineSegment(sketch, "E1587", {"start": v(-0.37, -35.27) * mm, "end": v(-0.47, -35.58) * mm});
            skLineSegment(sketch, "E1588", {"start": v(-0.47, -35.58) * mm, "end": v(-0.55, -35.9) * mm});
            skLineSegment(sketch, "E1589", {"start": v(-0.55, -35.9) * mm, "end": v(-0.62, -36.22) * mm});
            skLineSegment(sketch, "E1590", {"start": v(-0.62, -36.22) * mm, "end": v(-0.67, -36.54) * mm});
            skLineSegment(sketch, "E1591", {"start": v(-0.67, -36.54) * mm, "end": v(-0.7, -36.79) * mm});
            skLineSegment(sketch, "E1592", {"start": v(-0.7, -36.79) * mm, "end": v(-0.7, -36.87) * mm});
            skLineSegment(sketch, "E1593", {"start": v(-0.7, -36.87) * mm, "end": v(-0.7, -36.92) * mm});
            skLineSegment(sketch, "E1594", {"start": v(-0.7, -36.92) * mm, "end": v(-0.7, -37.08) * mm});
            skLineSegment(sketch, "E1595", {"start": v(-0.7, -37.08) * mm, "end": v(-0.71, -37.32) * mm});
            skLineSegment(sketch, "E1596", {"start": v(-0.71, -37.32) * mm, "end": v(-0.7, -37.57) * mm});
            skLineSegment(sketch, "E1597", {"start": v(-0.7, -37.57) * mm, "end": v(-0.7, -37.72) * mm});
            skLineSegment(sketch, "E1598", {"start": v(-0.7, -37.72) * mm, "end": v(-0.7, -37.77) * mm});
            skLineSegment(sketch, "E1599", {"start": v(-0.7, -37.77) * mm, "end": v(-0.7, -37.85) * mm});
            skLineSegment(sketch, "E1600", {"start": v(-0.7, -37.85) * mm, "end": v(-0.66, -38.1) * mm});
            skLineSegment(sketch, "E1601", {"start": v(-0.66, -38.1) * mm, "end": v(-0.61, -38.44) * mm});
            skLineSegment(sketch, "E1602", {"start": v(-0.61, -38.44) * mm, "end": v(-0.55, -38.77) * mm});
            skLineSegment(sketch, "E1603", {"start": v(-0.55, -38.77) * mm, "end": v(-0.46, -39.1) * mm});
            skLineSegment(sketch, "E1604", {"start": v(-0.46, -39.1) * mm, "end": v(-0.36, -39.41) * mm});
            skLineSegment(sketch, "E1605", {"start": v(-0.36, -39.41) * mm, "end": v(-0.24, -39.72) * mm});
            skLineSegment(sketch, "E1606", {"start": v(-0.24, -39.72) * mm, "end": v(-0.11, -40.02) * mm});
            skLineSegment(sketch, "E1607", {"start": v(-0.11, -40.02) * mm, "end": v(0.04, -40.32) * mm});
            skLineSegment(sketch, "E1608", {"start": v(0.04, -40.32) * mm, "end": v(0.2, -40.6) * mm});
            skLineSegment(sketch, "E1609", {"start": v(0.2, -40.6) * mm, "end": v(0.38, -40.89) * mm});
            skLineSegment(sketch, "E1610", {"start": v(0.38, -40.89) * mm, "end": v(0.57, -41.16) * mm});
            skLineSegment(sketch, "E1611", {"start": v(0.57, -41.16) * mm, "end": v(0.78, -41.41) * mm});
            skLineSegment(sketch, "E1612", {"start": v(0.78, -41.41) * mm, "end": v(1, -41.66) * mm});
            skLineSegment(sketch, "E1613", {"start": v(1, -41.66) * mm, "end": v(1.24, -41.9) * mm});
            skLineSegment(sketch, "E1614", {"start": v(1.24, -41.9) * mm, "end": v(1.49, -42.13) * mm});
            skLineSegment(sketch, "E1615", {"start": v(1.49, -42.13) * mm, "end": v(1.68, -42.3) * mm});
            skLineSegment(sketch, "E1616", {"start": v(1.68, -42.3) * mm, "end": v(1.75, -42.35) * mm});
            skLineSegment(sketch, "E1617", {"start": v(1.75, -42.35) * mm, "end": v(1.77, -42.36) * mm});
            skLineSegment(sketch, "E1618", {"start": v(1.77, -42.36) * mm, "end": v(1.82, -42.4) * mm});
            skLineSegment(sketch, "E1619", {"start": v(1.82, -42.4) * mm, "end": v(1.9, -42.46) * mm});
            skLineSegment(sketch, "E1620", {"start": v(1.9, -42.46) * mm, "end": v(2, -42.53) * mm});
            skLineSegment(sketch, "E1621", {"start": v(2, -42.53) * mm, "end": v(2.1, -42.6) * mm});
            skLineSegment(sketch, "E1622", {"start": v(2.1, -42.6) * mm, "end": v(2.2, -42.66) * mm});
            skLineSegment(sketch, "E1623", {"start": v(2.2, -42.66) * mm, "end": v(2.29, -42.72) * mm});
            skLineSegment(sketch, "E1624", {"start": v(2.29, -42.72) * mm, "end": v(2.36, -42.77) * mm});
            skLineSegment(sketch, "E1625", {"start": v(2.36, -42.77) * mm, "end": v(2.41, -42.8) * mm});
            skLineSegment(sketch, "E1626", {"start": v(2.41, -42.8) * mm, "end": v(2.43, -42.8) * mm});
            skLineSegment(sketch, "E1627", {"start": v(2.43, -42.8) * mm, "end": v(2.5, -42.85) * mm});
            skLineSegment(sketch, "E1628", {"start": v(2.5, -42.85) * mm, "end": v(2.38, -42.86) * mm});
            skLineSegment(sketch, "E1629", {"start": v(2.38, -42.86) * mm, "end": v(2.36, -42.86) * mm});
            skLineSegment(sketch, "E1630", {"start": v(2.36, -42.86) * mm, "end": v(2.31, -42.86) * mm});
            skLineSegment(sketch, "E1631", {"start": v(2.31, -42.86) * mm, "end": v(2.22, -42.87) * mm});
            skLineSegment(sketch, "E1632", {"start": v(2.22, -42.87) * mm, "end": v(2.11, -42.87) * mm});
            skLineSegment(sketch, "E1633", {"start": v(2.11, -42.87) * mm, "end": v(2, -42.86) * mm});
            skLineSegment(sketch, "E1634", {"start": v(2, -42.86) * mm, "end": v(1.88, -42.86) * mm});
            skLineSegment(sketch, "E1635", {"start": v(1.88, -42.86) * mm, "end": v(1.76, -42.86) * mm});
            skLineSegment(sketch, "E1636", {"start": v(1.76, -42.86) * mm, "end": v(1.66, -42.85) * mm});
            skLineSegment(sketch, "E1637", {"start": v(1.66, -42.85) * mm, "end": v(1.6, -42.84) * mm});
            skLineSegment(sketch, "E1638", {"start": v(1.6, -42.84) * mm, "end": v(1.57, -42.84) * mm});
            skLineSegment(sketch, "E1639", {"start": v(1.57, -42.84) * mm, "end": v(1.44, -42.83) * mm});
            skLineSegment(sketch, "E1640", {"start": v(1.44, -42.83) * mm, "end": v(1.05, -42.77) * mm});
            skLineSegment(sketch, "E1641", {"start": v(1.05, -42.77) * mm, "end": v(0.55, -42.65) * mm});
            skLineSegment(sketch, "E1642", {"start": v(0.55, -42.65) * mm, "end": v(0.07, -42.48) * mm});
            skLineSegment(sketch, "E1643", {"start": v(0.07, -42.48) * mm, "end": v(-0.29, -42.33) * mm});
            skLineSegment(sketch, "E1644", {"start": v(-0.29, -42.33) * mm, "end": v(-0.4, -42.27) * mm});
            skLineSegment(sketch, "E1645", {"start": v(-0.4, -42.27) * mm, "end": v(-0.5, -42.22) * mm});
            skLineSegment(sketch, "E1646", {"start": v(-0.5, -42.22) * mm, "end": v(-0.8, -42.05) * mm});
            skLineSegment(sketch, "E1647", {"start": v(-0.8, -42.05) * mm, "end": v(-1.16, -41.81) * mm});
            skLineSegment(sketch, "E1648", {"start": v(-1.16, -41.81) * mm, "end": v(-1.5, -41.55) * mm});
            skLineSegment(sketch, "E1649", {"start": v(-1.5, -41.55) * mm, "end": v(-1.74, -41.32) * mm});
            skLineSegment(sketch, "E1650", {"start": v(-1.74, -41.32) * mm, "end": v(-1.82, -41.24) * mm});
            skLineSegment(sketch, "E1651", {"start": v(-1.82, -41.24) * mm, "end": v(-1.9, -41.17) * mm});
            skLineSegment(sketch, "E1652", {"start": v(-1.9, -41.17) * mm, "end": v(-2.1, -40.94) * mm});
            skLineSegment(sketch, "E1653", {"start": v(-2.1, -40.94) * mm, "end": v(-2.36, -40.63) * mm});
            skLineSegment(sketch, "E1654", {"start": v(-2.36, -40.63) * mm, "end": v(-2.59, -40.3) * mm});
            skLineSegment(sketch, "E1655", {"start": v(-2.59, -40.3) * mm, "end": v(-2.8, -39.94) * mm});
            skLineSegment(sketch, "E1656", {"start": v(-2.8, -39.94) * mm, "end": v(-2.97, -39.58) * mm});
            skLineSegment(sketch, "E1657", {"start": v(-2.97, -39.58) * mm, "end": v(-3.12, -39.2) * mm});
            skLineSegment(sketch, "E1658", {"start": v(-3.12, -39.2) * mm, "end": v(-3.24, -38.82) * mm});
            skLineSegment(sketch, "E1659", {"start": v(-3.24, -38.82) * mm, "end": v(-3.32, -38.52) * mm});
            skLineSegment(sketch, "E1660", {"start": v(-3.32, -38.52) * mm, "end": v(-3.34, -38.42) * mm});
            skLineSegment(sketch, "E1661", {"start": v(-3.34, -38.42) * mm, "end": v(-3.35, -38.38) * mm});
            skLineSegment(sketch, "E1662", {"start": v(-3.35, -38.38) * mm, "end": v(-3.37, -38.27) * mm});
            skLineSegment(sketch, "E1663", {"start": v(-3.37, -38.27) * mm, "end": v(-3.4, -38.15) * mm});
            skLineSegment(sketch, "E1664", {"start": v(-3.4, -38.15) * mm, "end": v(-3.4, -38.03) * mm});
            skLineSegment(sketch, "E1665", {"start": v(-3.4, -38.03) * mm, "end": v(-3.42, -37.9) * mm});
            skLineSegment(sketch, "E1666", {"start": v(-3.42, -37.9) * mm, "end": v(-3.43, -37.79) * mm});
            skLineSegment(sketch, "E1667", {"start": v(-3.43, -37.79) * mm, "end": v(-3.44, -37.65) * mm});
            skLineSegment(sketch, "E1668", {"start": v(-3.44, -37.65) * mm, "end": v(-3.44, -37.5) * mm});
            skLineSegment(sketch, "E1669", {"start": v(-3.44, -37.5) * mm, "end": v(-3.44, -37.37) * mm});
            skLineSegment(sketch, "E1670", {"start": v(-3.44, -37.37) * mm, "end": v(-3.44, -37.32) * mm});
            skLineSegment(sketch, "E1671", {"start": v(-3.44, -37.32) * mm, "end": v(-3.44, -37.29) * mm});
            skLineSegment(sketch, "E1672", {"start": v(-3.44, -37.29) * mm, "end": v(-3.44, -37.18) * mm});
            skLineSegment(sketch, "E1673", {"start": v(-3.44, -37.18) * mm, "end": v(-3.44, -37.07) * mm});
            skLineSegment(sketch, "E1674", {"start": v(-3.44, -37.07) * mm, "end": v(-3.44, -36.97) * mm});
            skLineSegment(sketch, "E1675", {"start": v(-3.44, -36.97) * mm, "end": v(-3.43, -36.9) * mm});
            skLineSegment(sketch, "E1676", {"start": v(-3.43, -36.9) * mm, "end": v(-3.43, -36.83) * mm});
            skLineSegment(sketch, "E1677", {"start": v(-3.43, -36.83) * mm, "end": v(-3.43, -36.76) * mm});
            skLineSegment(sketch, "E1678", {"start": v(-3.43, -36.76) * mm, "end": v(-3.42, -36.7) * mm});
            skLineSegment(sketch, "E1679", {"start": v(-3.42, -36.7) * mm, "end": v(-3.41, -36.65) * mm});
            skLineSegment(sketch, "E1680", {"start": v(-3.41, -36.65) * mm, "end": v(-3.4, -36.63) * mm});
            skLineSegment(sketch, "E1681", {"start": v(-3.4, -36.63) * mm, "end": v(-3.4, -36.52) * mm});
            skLineSegment(sketch, "E1682", {"start": v(-3.4, -36.52) * mm, "end": v(-3.33, -36.17) * mm});
            skLineSegment(sketch, "E1683", {"start": v(-3.33, -36.17) * mm, "end": v(-3.21, -35.72) * mm});
            skLineSegment(sketch, "E1684", {"start": v(-3.21, -35.72) * mm, "end": v(-3.06, -35.28) * mm});
            skLineSegment(sketch, "E1685", {"start": v(-3.06, -35.28) * mm, "end": v(-2.88, -34.87) * mm});
            skLineSegment(sketch, "E1686", {"start": v(-2.88, -34.87) * mm, "end": v(-2.66, -34.47) * mm});
            skLineSegment(sketch, "E1687", {"start": v(-2.66, -34.47) * mm, "end": v(-2.41, -34.1) * mm});
            skLineSegment(sketch, "E1688", {"start": v(-2.41, -34.1) * mm, "end": v(-2.13, -33.73) * mm});
            skLineSegment(sketch, "E1689", {"start": v(-2.13, -33.73) * mm, "end": v(-1.9, -33.47) * mm});
            skLineSegment(sketch, "E1690", {"start": v(-1.9, -33.47) * mm, "end": v(-1.81, -33.4) * mm});
            skLineSegment(sketch, "E1691", {"start": v(-1.81, -33.4) * mm, "end": v(-1.73, -33.3) * mm});
            skLineSegment(sketch, "E1692", {"start": v(-1.73, -33.3) * mm, "end": v(-1.47, -33.08) * mm});
            skLineSegment(sketch, "E1693", {"start": v(-1.47, -33.08) * mm, "end": v(-1.11, -32.8) * mm});
            skLineSegment(sketch, "E1694", {"start": v(-1.11, -32.8) * mm, "end": v(-0.73, -32.55) * mm});
            skLineSegment(sketch, "E1695", {"start": v(-0.73, -32.55) * mm, "end": v(-0.32, -32.33) * mm});
            skLineSegment(sketch, "E1696", {"start": v(-0.32, -32.33) * mm, "end": v(0.1, -32.15) * mm});
            skLineSegment(sketch, "E1697", {"start": v(0.1, -32.15) * mm, "end": v(0.53, -32) * mm});
            skLineSegment(sketch, "E1698", {"start": v(0.53, -32) * mm, "end": v(0.98, -31.89) * mm});
            skLineSegment(sketch, "E1699", {"start": v(0.98, -31.89) * mm, "end": v(1.33, -31.83) * mm});
            skLineSegment(sketch, "E1700", {"start": v(1.33, -31.83) * mm, "end": v(1.45, -31.81) * mm});
            skLineSegment(sketch, "E1701", {"start": v(1.45, -31.81) * mm, "end": v(1.5, -31.8) * mm});
            skLineSegment(sketch, "E1702", {"start": v(1.5, -31.8) * mm, "end": v(1.68, -31.8) * mm});
            skLineSegment(sketch, "E1703", {"start": v(1.68, -31.8) * mm, "end": v(1.94, -31.78) * mm});
            skLineSegment(sketch, "E1704", {"start": v(1.94, -31.78) * mm, "end": v(2.2, -31.78) * mm});
            skLineSegment(sketch, "E1705", {"start": v(2.2, -31.78) * mm, "end": v(2.35, -31.78) * mm});
            skLineSegment(sketch, "E1706", {"start": v(2.35, -31.78) * mm, "end": v(2.4, -31.78) * mm});
            skSolve(sketch);
        }
        {
            var Q0;
            Q0=makeQuery(id+"F1.imprint","IMPRINT",FACE,{"disambiguationData":[TD([[makeQuery(id+"F1.imprint","IMPRINT",EDGE,{"derivedFrom":sQuery(id+"F1.wireOp",EDGE,"E6")}),-1.0]])]});
            var sketch = newSketch(context, id + "F5", { "sketchPlane" : qUnion([Q0])});
            skLineSegment(sketch, "E1707", {"start": v(-0.31, -11.8) * mm, "end": v(-0.37, -11.85) * mm});
            skLineSegment(sketch, "E1708", {"start": v(-0.37, -11.85) * mm, "end": v(-0.52, -12.05) * mm});
            skLineSegment(sketch, "E1709", {"start": v(-0.52, -12.05) * mm, "end": v(-0.67, -12.3) * mm});
            skLineSegment(sketch, "E1710", {"start": v(-0.67, -12.3) * mm, "end": v(-0.77, -12.58) * mm});
            skLineSegment(sketch, "E1711", {"start": v(-0.77, -12.58) * mm, "end": v(-0.82, -12.86) * mm});
            skLineSegment(sketch, "E1712", {"start": v(-0.82, -12.86) * mm, "end": v(-0.84, -13.14) * mm});
            skLineSegment(sketch, "E1713", {"start": v(-0.84, -13.14) * mm, "end": v(-0.83, -13.4) * mm});
            skLineSegment(sketch, "E1714", {"start": v(-0.83, -13.4) * mm, "end": v(-0.8, -13.68) * mm});
            skLineSegment(sketch, "E1715", {"start": v(-0.8, -13.68) * mm, "end": v(-0.76, -13.94) * mm});
            skLineSegment(sketch, "E1716", {"start": v(-0.76, -13.94) * mm, "end": v(-0.7, -14.18) * mm});
            skLineSegment(sketch, "E1717", {"start": v(-0.7, -14.18) * mm, "end": v(-0.65, -14.4) * mm});
            skLineSegment(sketch, "E1718", {"start": v(-0.65, -14.4) * mm, "end": v(-0.6, -14.61) * mm});
            skLineSegment(sketch, "E1719", {"start": v(-0.6, -14.61) * mm, "end": v(-0.57, -14.8) * mm});
            skLineSegment(sketch, "E1720", {"start": v(-0.57, -14.8) * mm, "end": v(-0.56, -14.95) * mm});
            skLineSegment(sketch, "E1721", {"start": v(-0.56, -14.95) * mm, "end": v(-0.58, -15.07) * mm});
            skLineSegment(sketch, "E1722", {"start": v(-0.58, -15.07) * mm, "end": v(-0.63, -15.16) * mm});
            skLineSegment(sketch, "E1723", {"start": v(-0.63, -15.16) * mm, "end": v(-0.7, -15.2) * mm});
            skLineSegment(sketch, "E1724", {"start": v(-0.7, -15.2) * mm, "end": v(-0.73, -15.2) * mm});
            skLineSegment(sketch, "E1725", {"start": v(-0.73, -15.2) * mm, "end": v(-0.74, -15.2) * mm});
            skLineSegment(sketch, "E1726", {"start": v(-0.74, -15.2) * mm, "end": v(-0.76, -15.15) * mm});
            skLineSegment(sketch, "E1727", {"start": v(-0.76, -15.15) * mm, "end": v(-0.8, -15.1) * mm});
            skLineSegment(sketch, "E1728", {"start": v(-0.8, -15.1) * mm, "end": v(-0.86, -15.02) * mm});
            skLineSegment(sketch, "E1729", {"start": v(-0.86, -15.02) * mm, "end": v(-0.94, -14.92) * mm});
            skLineSegment(sketch, "E1730", {"start": v(-0.94, -14.92) * mm, "end": v(-1.02, -14.82) * mm});
            skLineSegment(sketch, "E1731", {"start": v(-1.02, -14.82) * mm, "end": v(-1.12, -14.71) * mm});
            skLineSegment(sketch, "E1732", {"start": v(-1.12, -14.71) * mm, "end": v(-1.23, -14.6) * mm});
            skLineSegment(sketch, "E1733", {"start": v(-1.23, -14.6) * mm, "end": v(-1.35, -14.5) * mm});
            skLineSegment(sketch, "E1734", {"start": v(-1.35, -14.5) * mm, "end": v(-1.48, -14.39) * mm});
            skLineSegment(sketch, "E1735", {"start": v(-1.48, -14.39) * mm, "end": v(-1.62, -14.3) * mm});
            skLineSegment(sketch, "E1736", {"start": v(-1.62, -14.3) * mm, "end": v(-1.77, -14.21) * mm});
            skLineSegment(sketch, "E1737", {"start": v(-1.77, -14.21) * mm, "end": v(-1.92, -14.15) * mm});
            skLineSegment(sketch, "E1738", {"start": v(-1.92, -14.15) * mm, "end": v(-2.08, -14.1) * mm});
            skLineSegment(sketch, "E1739", {"start": v(-2.08, -14.1) * mm, "end": v(-2.24, -14.08) * mm});
            skLineSegment(sketch, "E1740", {"start": v(-2.24, -14.08) * mm, "end": v(-2.37, -14.09) * mm});
            skLineSegment(sketch, "E1741", {"start": v(-2.37, -14.09) * mm, "end": v(-2.41, -14.1) * mm});
            skLineSegment(sketch, "E1742", {"start": v(-2.41, -14.1) * mm, "end": v(-2.35, -14.17) * mm});
            skLineSegment(sketch, "E1743", {"start": v(-2.35, -14.17) * mm, "end": v(-2.17, -14.43) * mm});
            skLineSegment(sketch, "E1744", {"start": v(-2.17, -14.43) * mm, "end": v(-1.98, -14.76) * mm});
            skLineSegment(sketch, "E1745", {"start": v(-1.98, -14.76) * mm, "end": v(-1.84, -15.06) * mm});
            skLineSegment(sketch, "E1746", {"start": v(-1.84, -15.06) * mm, "end": v(-1.73, -15.35) * mm});
            skLineSegment(sketch, "E1747", {"start": v(-1.73, -15.35) * mm, "end": v(-1.65, -15.62) * mm});
            skLineSegment(sketch, "E1748", {"start": v(-1.65, -15.62) * mm, "end": v(-1.61, -15.87) * mm});
            skLineSegment(sketch, "E1749", {"start": v(-1.61, -15.87) * mm, "end": v(-1.6, -16.1) * mm});
            skLineSegment(sketch, "E1750", {"start": v(-1.6, -16.1) * mm, "end": v(-1.6, -16.3) * mm});
            skLineSegment(sketch, "E1751", {"start": v(-1.6, -16.3) * mm, "end": v(-1.6, -16.5) * mm});
            skLineSegment(sketch, "E1752", {"start": v(-1.6, -16.5) * mm, "end": v(-1.64, -16.65) * mm});
            skLineSegment(sketch, "E1753", {"start": v(-1.64, -16.65) * mm, "end": v(-1.68, -16.8) * mm});
            skLineSegment(sketch, "E1754", {"start": v(-1.68, -16.8) * mm, "end": v(-1.72, -16.9) * mm});
            skLineSegment(sketch, "E1755", {"start": v(-1.72, -16.9) * mm, "end": v(-1.76, -17) * mm});
            skLineSegment(sketch, "E1756", {"start": v(-1.76, -17) * mm, "end": v(-1.79, -17.06) * mm});
            skLineSegment(sketch, "E1757", {"start": v(-1.79, -17.06) * mm, "end": v(-1.81, -17.1) * mm});
            skLineSegment(sketch, "E1758", {"start": v(-1.81, -17.1) * mm, "end": v(-1.82, -17.11) * mm});
            skLineSegment(sketch, "E1759", {"start": v(-1.82, -17.11) * mm, "end": v(-1.86, -17.06) * mm});
            skLineSegment(sketch, "E1760", {"start": v(-1.86, -17.06) * mm, "end": v(-1.99, -16.92) * mm});
            skLineSegment(sketch, "E1761", {"start": v(-1.99, -16.92) * mm, "end": v(-2.16, -16.75) * mm});
            skLineSegment(sketch, "E1762", {"start": v(-2.16, -16.75) * mm, "end": v(-2.33, -16.6) * mm});
            skLineSegment(sketch, "E1763", {"start": v(-2.33, -16.6) * mm, "end": v(-2.5, -16.48) * mm});
            skLineSegment(sketch, "E1764", {"start": v(-2.5, -16.48) * mm, "end": v(-2.66, -16.37) * mm});
            skLineSegment(sketch, "E1765", {"start": v(-2.66, -16.37) * mm, "end": v(-2.82, -16.29) * mm});
            skLineSegment(sketch, "E1766", {"start": v(-2.82, -16.29) * mm, "end": v(-2.98, -16.22) * mm});
            skLineSegment(sketch, "E1767", {"start": v(-2.98, -16.22) * mm, "end": v(-3.12, -16.17) * mm});
            skLineSegment(sketch, "E1768", {"start": v(-3.12, -16.17) * mm, "end": v(-3.24, -16.13) * mm});
            skLineSegment(sketch, "E1769", {"start": v(-3.24, -16.13) * mm, "end": v(-3.36, -16.1) * mm});
            skLineSegment(sketch, "E1770", {"start": v(-3.36, -16.1) * mm, "end": v(-3.45, -16.1) * mm});
            skLineSegment(sketch, "E1771", {"start": v(-3.45, -16.1) * mm, "end": v(-3.53, -16.1) * mm});
            skLineSegment(sketch, "E1772", {"start": v(-3.53, -16.1) * mm, "end": v(-3.58, -16.1) * mm});
            skLineSegment(sketch, "E1773", {"start": v(-3.58, -16.1) * mm, "end": v(-3.6, -16.12) * mm});
            skLineSegment(sketch, "E1774", {"start": v(-3.6, -16.12) * mm, "end": v(-3.6, -16.14) * mm});
            skLineSegment(sketch, "E1775", {"start": v(-3.6, -16.14) * mm, "end": v(-3.58, -16.17) * mm});
            skLineSegment(sketch, "E1776", {"start": v(-3.58, -16.17) * mm, "end": v(-3.57, -16.17) * mm});
            skLineSegment(sketch, "E1777", {"start": v(-3.57, -16.17) * mm, "end": v(-3.52, -16.2) * mm});
            skLineSegment(sketch, "E1778", {"start": v(-3.52, -16.2) * mm, "end": v(-3.39, -16.32) * mm});
            skLineSegment(sketch, "E1779", {"start": v(-3.39, -16.32) * mm, "end": v(-3.24, -16.5) * mm});
            skLineSegment(sketch, "E1780", {"start": v(-3.24, -16.5) * mm, "end": v(-3.11, -16.7) * mm});
            skLineSegment(sketch, "E1781", {"start": v(-3.11, -16.7) * mm, "end": v(-3.01, -16.9) * mm});
            skLineSegment(sketch, "E1782", {"start": v(-3.01, -16.9) * mm, "end": v(-2.94, -17.13) * mm});
            skLineSegment(sketch, "E1783", {"start": v(-2.94, -17.13) * mm, "end": v(-2.88, -17.36) * mm});
            skLineSegment(sketch, "E1784", {"start": v(-2.88, -17.36) * mm, "end": v(-2.84, -17.58) * mm});
            skLineSegment(sketch, "E1785", {"start": v(-2.84, -17.58) * mm, "end": v(-2.82, -17.8) * mm});
            skLineSegment(sketch, "E1786", {"start": v(-2.82, -17.8) * mm, "end": v(-2.8, -18.02) * mm});
            skLineSegment(sketch, "E1787", {"start": v(-2.8, -18.02) * mm, "end": v(-2.8, -18.22) * mm});
            skLineSegment(sketch, "E1788", {"start": v(-2.8, -18.22) * mm, "end": v(-2.8, -18.4) * mm});
            skLineSegment(sketch, "E1789", {"start": v(-2.8, -18.4) * mm, "end": v(-2.81, -18.57) * mm});
            skLineSegment(sketch, "E1790", {"start": v(-2.81, -18.57) * mm, "end": v(-2.82, -18.7) * mm});
            skLineSegment(sketch, "E1791", {"start": v(-2.82, -18.7) * mm, "end": v(-2.84, -18.8) * mm});
            skLineSegment(sketch, "E1792", {"start": v(-2.84, -18.8) * mm, "end": v(-2.84, -18.86) * mm});
            skLineSegment(sketch, "E1793", {"start": v(-2.84, -18.86) * mm, "end": v(-2.85, -18.89) * mm});
            skLineSegment(sketch, "E1794", {"start": v(-2.85, -18.89) * mm, "end": v(-2.86, -18.88) * mm});
            skLineSegment(sketch, "E1795", {"start": v(-2.86, -18.88) * mm, "end": v(-2.9, -18.85) * mm});
            skLineSegment(sketch, "E1796", {"start": v(-2.9, -18.85) * mm, "end": v(-2.95, -18.8) * mm});
            skLineSegment(sketch, "E1797", {"start": v(-2.95, -18.8) * mm, "end": v(-3.03, -18.74) * mm});
            skLineSegment(sketch, "E1798", {"start": v(-3.03, -18.74) * mm, "end": v(-3.12, -18.68) * mm});
            skLineSegment(sketch, "E1799", {"start": v(-3.12, -18.68) * mm, "end": v(-3.23, -18.6) * mm});
            skLineSegment(sketch, "E1800", {"start": v(-3.23, -18.6) * mm, "end": v(-3.35, -18.54) * mm});
            skLineSegment(sketch, "E1801", {"start": v(-3.35, -18.54) * mm, "end": v(-3.47, -18.47) * mm});
            skLineSegment(sketch, "E1802", {"start": v(-3.47, -18.47) * mm, "end": v(-3.6, -18.4) * mm});
            skLineSegment(sketch, "E1803", {"start": v(-3.6, -18.4) * mm, "end": v(-3.74, -18.35) * mm});
            skLineSegment(sketch, "E1804", {"start": v(-3.74, -18.35) * mm, "end": v(-3.88, -18.31) * mm});
            skLineSegment(sketch, "E1805", {"start": v(-3.88, -18.31) * mm, "end": v(-4.01, -18.29) * mm});
            skLineSegment(sketch, "E1806", {"start": v(-4.01, -18.29) * mm, "end": v(-4.14, -18.28) * mm});
            skLineSegment(sketch, "E1807", {"start": v(-4.14, -18.28) * mm, "end": v(-4.27, -18.3) * mm});
            skLineSegment(sketch, "E1808", {"start": v(-4.27, -18.3) * mm, "end": v(-4.38, -18.35) * mm});
            skLineSegment(sketch, "E1809", {"start": v(-4.38, -18.35) * mm, "end": v(-4.47, -18.4) * mm});
            skLineSegment(sketch, "E1810", {"start": v(-4.47, -18.4) * mm, "end": v(-4.49, -18.43) * mm});
            skLineSegment(sketch, "E1811", {"start": v(-4.49, -18.43) * mm, "end": v(-4.43, -18.46) * mm});
            skLineSegment(sketch, "E1812", {"start": v(-4.43, -18.46) * mm, "end": v(-4.24, -18.56) * mm});
            skLineSegment(sketch, "E1813", {"start": v(-4.24, -18.56) * mm, "end": v(-4.04, -18.7) * mm});
            skLineSegment(sketch, "E1814", {"start": v(-4.04, -18.7) * mm, "end": v(-3.88, -18.85) * mm});
            skLineSegment(sketch, "E1815", {"start": v(-3.88, -18.85) * mm, "end": v(-3.76, -19) * mm});
            skLineSegment(sketch, "E1816", {"start": v(-3.76, -19) * mm, "end": v(-3.67, -19.14) * mm});
            skLineSegment(sketch, "E1817", {"start": v(-3.67, -19.14) * mm, "end": v(-3.6, -19.3) * mm});
            skLineSegment(sketch, "E1818", {"start": v(-3.6, -19.3) * mm, "end": v(-3.57, -19.44) * mm});
            skLineSegment(sketch, "E1819", {"start": v(-3.57, -19.44) * mm, "end": v(-3.55, -19.6) * mm});
            skLineSegment(sketch, "E1820", {"start": v(-3.55, -19.6) * mm, "end": v(-3.55, -19.76) * mm});
            skLineSegment(sketch, "E1821", {"start": v(-3.55, -19.76) * mm, "end": v(-3.56, -19.93) * mm});
            skLineSegment(sketch, "E1822", {"start": v(-3.56, -19.93) * mm, "end": v(-3.59, -20.1) * mm});
            skLineSegment(sketch, "E1823", {"start": v(-3.59, -20.1) * mm, "end": v(-3.61, -20.27) * mm});
            skLineSegment(sketch, "E1824", {"start": v(-3.61, -20.27) * mm, "end": v(-3.64, -20.44) * mm});
            skLineSegment(sketch, "E1825", {"start": v(-3.64, -20.44) * mm, "end": v(-3.67, -20.62) * mm});
            skLineSegment(sketch, "E1826", {"start": v(-3.67, -20.62) * mm, "end": v(-3.7, -20.8) * mm});
            skLineSegment(sketch, "E1827", {"start": v(-3.7, -20.8) * mm, "end": v(-3.7, -20.94) * mm});
            skLineSegment(sketch, "E1828", {"start": v(-3.7, -20.94) * mm, "end": v(-3.7, -20.99) * mm});
            skLineSegment(sketch, "E1829", {"start": v(-3.7, -20.99) * mm, "end": v(-3.7, -21.08) * mm});
            skLineSegment(sketch, "E1830", {"start": v(-3.7, -21.08) * mm, "end": v(-3.7, -21.35) * mm});
            skLineSegment(sketch, "E1831", {"start": v(-3.7, -21.35) * mm, "end": v(-3.66, -21.69) * mm});
            skLineSegment(sketch, "E1832", {"start": v(-3.66, -21.69) * mm, "end": v(-3.6, -22) * mm});
            skLineSegment(sketch, "E1833", {"start": v(-3.6, -22) * mm, "end": v(-3.53, -22.29) * mm});
            skLineSegment(sketch, "E1834", {"start": v(-3.53, -22.29) * mm, "end": v(-3.44, -22.55) * mm});
            skLineSegment(sketch, "E1835", {"start": v(-3.44, -22.55) * mm, "end": v(-3.33, -22.8) * mm});
            skLineSegment(sketch, "E1836", {"start": v(-3.33, -22.8) * mm, "end": v(-3.21, -23.01) * mm});
            skLineSegment(sketch, "E1837", {"start": v(-3.21, -23.01) * mm, "end": v(-3.09, -23.2) * mm});
            skLineSegment(sketch, "E1838", {"start": v(-3.09, -23.2) * mm, "end": v(-2.96, -23.38) * mm});
            skLineSegment(sketch, "E1839", {"start": v(-2.96, -23.38) * mm, "end": v(-2.84, -23.53) * mm});
            skLineSegment(sketch, "E1840", {"start": v(-2.84, -23.53) * mm, "end": v(-2.71, -23.66) * mm});
            skLineSegment(sketch, "E1841", {"start": v(-2.71, -23.66) * mm, "end": v(-2.6, -23.78) * mm});
            skLineSegment(sketch, "E1842", {"start": v(-2.6, -23.78) * mm, "end": v(-2.5, -23.87) * mm});
            skLineSegment(sketch, "E1843", {"start": v(-2.5, -23.87) * mm, "end": v(-2.4, -23.94) * mm});
            skLineSegment(sketch, "E1844", {"start": v(-2.4, -23.94) * mm, "end": v(-2.32, -24) * mm});
            skLineSegment(sketch, "E1845", {"start": v(-2.32, -24) * mm, "end": v(-2.28, -24.02) * mm});
            skLineSegment(sketch, "E1846", {"start": v(-2.28, -24.02) * mm, "end": v(-2.27, -24.03) * mm});
            skLineSegment(sketch, "E1847", {"start": v(-2.27, -24.03) * mm, "end": v(-2.87, -24.03) * mm});
            skLineSegment(sketch, "E1848", {"start": v(-2.87, -24.03) * mm, "end": v(-2.87, -24.5) * mm});
            skLineSegment(sketch, "E1849", {"start": v(-2.87, -24.5) * mm, "end": v(2.8, -24.5) * mm});
            skLineSegment(sketch, "E1850", {"start": v(2.8, -24.5) * mm, "end": v(2.8, -24.03) * mm});
            skLineSegment(sketch, "E1851", {"start": v(2.8, -24.03) * mm, "end": v(2.1, -24.03) * mm});
            skLineSegment(sketch, "E1852", {"start": v(2.1, -24.03) * mm, "end": v(2.12, -24.02) * mm});
            skLineSegment(sketch, "E1853", {"start": v(2.12, -24.02) * mm, "end": v(2.2, -23.99) * mm});
            skLineSegment(sketch, "E1854", {"start": v(2.2, -23.99) * mm, "end": v(2.32, -23.93) * mm});
            skLineSegment(sketch, "E1855", {"start": v(2.32, -23.93) * mm, "end": v(2.46, -23.85) * mm});
            skLineSegment(sketch, "E1856", {"start": v(2.46, -23.85) * mm, "end": v(2.63, -23.75) * mm});
            skLineSegment(sketch, "E1857", {"start": v(2.63, -23.75) * mm, "end": v(2.8, -23.63) * mm});
            skLineSegment(sketch, "E1858", {"start": v(2.8, -23.63) * mm, "end": v(2.98, -23.5) * mm});
            skLineSegment(sketch, "E1859", {"start": v(2.98, -23.5) * mm, "end": v(3.17, -23.34) * mm});
            skLineSegment(sketch, "E1860", {"start": v(3.17, -23.34) * mm, "end": v(3.36, -23.16) * mm});
            skLineSegment(sketch, "E1861", {"start": v(3.36, -23.16) * mm, "end": v(3.55, -22.95) * mm});
            skLineSegment(sketch, "E1862", {"start": v(3.55, -22.95) * mm, "end": v(3.73, -22.72) * mm});
            skLineSegment(sketch, "E1863", {"start": v(3.73, -22.72) * mm, "end": v(3.9, -22.47) * mm});
            skLineSegment(sketch, "E1864", {"start": v(3.9, -22.47) * mm, "end": v(4.04, -22.2) * mm});
            skLineSegment(sketch, "E1865", {"start": v(4.04, -22.2) * mm, "end": v(4.17, -21.9) * mm});
            skLineSegment(sketch, "E1866", {"start": v(4.17, -21.9) * mm, "end": v(4.27, -21.56) * mm});
            skLineSegment(sketch, "E1867", {"start": v(4.27, -21.56) * mm, "end": v(4.35, -21.2) * mm});
            skLineSegment(sketch, "E1868", {"start": v(4.35, -21.2) * mm, "end": v(4.39, -20.91) * mm});
            skLineSegment(sketch, "E1869", {"start": v(4.39, -20.91) * mm, "end": v(4.4, -20.81) * mm});
            skLineSegment(sketch, "E1870", {"start": v(4.4, -20.81) * mm, "end": v(4.4, -20.8) * mm});
            skLineSegment(sketch, "E1871", {"start": v(4.4, -20.8) * mm, "end": v(4.4, -20.76) * mm});
            skLineSegment(sketch, "E1872", {"start": v(4.4, -20.76) * mm, "end": v(4.4, -20.7) * mm});
            skLineSegment(sketch, "E1873", {"start": v(4.4, -20.7) * mm, "end": v(4.4, -20.61) * mm});
            skLineSegment(sketch, "E1874", {"start": v(4.4, -20.61) * mm, "end": v(4.39, -20.5) * mm});
            skLineSegment(sketch, "E1875", {"start": v(4.39, -20.5) * mm, "end": v(4.38, -20.4) * mm});
            skLineSegment(sketch, "E1876", {"start": v(4.38, -20.4) * mm, "end": v(4.38, -20.26) * mm});
            skLineSegment(sketch, "E1877", {"start": v(4.38, -20.26) * mm, "end": v(4.36, -20.13) * mm});
            skLineSegment(sketch, "E1878", {"start": v(4.36, -20.13) * mm, "end": v(4.34, -19.98) * mm});
            skLineSegment(sketch, "E1879", {"start": v(4.34, -19.98) * mm, "end": v(4.32, -19.84) * mm});
            skLineSegment(sketch, "E1880", {"start": v(4.32, -19.84) * mm, "end": v(4.3, -19.7) * mm});
            skLineSegment(sketch, "E1881", {"start": v(4.3, -19.7) * mm, "end": v(4.25, -19.55) * mm});
            skLineSegment(sketch, "E1882", {"start": v(4.25, -19.55) * mm, "end": v(4.2, -19.4) * mm});
            skLineSegment(sketch, "E1883", {"start": v(4.2, -19.4) * mm, "end": v(4.16, -19.28) * mm});
            skLineSegment(sketch, "E1884", {"start": v(4.16, -19.28) * mm, "end": v(4.1, -19.16) * mm});
            skLineSegment(sketch, "E1885", {"start": v(4.1, -19.16) * mm, "end": v(4.04, -19.09) * mm});
            skLineSegment(sketch, "E1886", {"start": v(4.04, -19.09) * mm, "end": v(4.02, -19.06) * mm});
            skLineSegment(sketch, "E1887", {"start": v(4.02, -19.06) * mm, "end": v(4.01, -19.1) * mm});
            skLineSegment(sketch, "E1888", {"start": v(4.01, -19.1) * mm, "end": v(3.97, -19.22) * mm});
            skLineSegment(sketch, "E1889", {"start": v(3.97, -19.22) * mm, "end": v(3.91, -19.33) * mm});
            skLineSegment(sketch, "E1890", {"start": v(3.91, -19.33) * mm, "end": v(3.85, -19.42) * mm});
            skLineSegment(sketch, "E1891", {"start": v(3.85, -19.42) * mm, "end": v(3.78, -19.49) * mm});
            skLineSegment(sketch, "E1892", {"start": v(3.78, -19.49) * mm, "end": v(3.72, -19.53) * mm});
            skLineSegment(sketch, "E1893", {"start": v(3.72, -19.53) * mm, "end": v(3.67, -19.55) * mm});
            skLineSegment(sketch, "E1894", {"start": v(3.67, -19.55) * mm, "end": v(3.64, -19.56) * mm});
            skLineSegment(sketch, "E1895", {"start": v(3.64, -19.56) * mm, "end": v(3.63, -19.57) * mm});
            skLineSegment(sketch, "E1896", {"start": v(3.63, -19.57) * mm, "end": v(3.62, -19.57) * mm});
            skLineSegment(sketch, "E1897", {"start": v(3.62, -19.57) * mm, "end": v(3.6, -19.56) * mm});
            skLineSegment(sketch, "E1898", {"start": v(3.6, -19.56) * mm, "end": v(3.59, -19.53) * mm});
            skLineSegment(sketch, "E1899", {"start": v(3.59, -19.53) * mm, "end": v(3.58, -19.48) * mm});
            skLineSegment(sketch, "E1900", {"start": v(3.58, -19.48) * mm, "end": v(3.6, -19.4) * mm});
            skLineSegment(sketch, "E1901", {"start": v(3.6, -19.4) * mm, "end": v(3.6, -19.32) * mm});
            skLineSegment(sketch, "E1902", {"start": v(3.6, -19.32) * mm, "end": v(3.63, -19.22) * mm});
            skLineSegment(sketch, "E1903", {"start": v(3.63, -19.22) * mm, "end": v(3.65, -19.12) * mm});
            skLineSegment(sketch, "E1904", {"start": v(3.65, -19.12) * mm, "end": v(3.68, -19) * mm});
            skLineSegment(sketch, "E1905", {"start": v(3.68, -19) * mm, "end": v(3.71, -18.88) * mm});
            skLineSegment(sketch, "E1906", {"start": v(3.71, -18.88) * mm, "end": v(3.75, -18.75) * mm});
            skLineSegment(sketch, "E1907", {"start": v(3.75, -18.75) * mm, "end": v(3.78, -18.63) * mm});
            skLineSegment(sketch, "E1908", {"start": v(3.78, -18.63) * mm, "end": v(3.8, -18.5) * mm});
            skLineSegment(sketch, "E1909", {"start": v(3.8, -18.5) * mm, "end": v(3.83, -18.39) * mm});
            skLineSegment(sketch, "E1910", {"start": v(3.83, -18.39) * mm, "end": v(3.85, -18.27) * mm});
            skLineSegment(sketch, "E1911", {"start": v(3.85, -18.27) * mm, "end": v(3.86, -18.17) * mm});
            skLineSegment(sketch, "E1912", {"start": v(3.86, -18.17) * mm, "end": v(3.87, -18.1) * mm});
            skLineSegment(sketch, "E1913", {"start": v(3.87, -18.1) * mm, "end": v(3.87, -18.08) * mm});
            skLineSegment(sketch, "E1914", {"start": v(3.87, -18.08) * mm, "end": v(3.87, -17.99) * mm});
            skLineSegment(sketch, "E1915", {"start": v(3.87, -17.99) * mm, "end": v(3.84, -17.71) * mm});
            skLineSegment(sketch, "E1916", {"start": v(3.84, -17.71) * mm, "end": v(3.75, -17.4) * mm});
            skLineSegment(sketch, "E1917", {"start": v(3.75, -17.4) * mm, "end": v(3.63, -17.16) * mm});
            skLineSegment(sketch, "E1918", {"start": v(3.63, -17.16) * mm, "end": v(3.5, -16.96) * mm});
            skLineSegment(sketch, "E1919", {"start": v(3.5, -16.96) * mm, "end": v(3.36, -16.81) * mm});
            skLineSegment(sketch, "E1920", {"start": v(3.36, -16.81) * mm, "end": v(3.24, -16.7) * mm});
            skLineSegment(sketch, "E1921", {"start": v(3.24, -16.7) * mm, "end": v(3.16, -16.65) * mm});
            skLineSegment(sketch, "E1922", {"start": v(3.16, -16.65) * mm, "end": v(3.12, -16.63) * mm});
            skLineSegment(sketch, "E1923", {"start": v(3.12, -16.63) * mm, "end": v(3.13, -16.64) * mm});
            skLineSegment(sketch, "E1924", {"start": v(3.13, -16.64) * mm, "end": v(3.13, -16.68) * mm});
            skLineSegment(sketch, "E1925", {"start": v(3.13, -16.68) * mm, "end": v(3.14, -16.74) * mm});
            skLineSegment(sketch, "E1926", {"start": v(3.14, -16.74) * mm, "end": v(3.14, -16.82) * mm});
            skLineSegment(sketch, "E1927", {"start": v(3.14, -16.82) * mm, "end": v(3.14, -16.91) * mm});
            skLineSegment(sketch, "E1928", {"start": v(3.14, -16.91) * mm, "end": v(3.14, -17.02) * mm});
            skLineSegment(sketch, "E1929", {"start": v(3.14, -17.02) * mm, "end": v(3.14, -17.13) * mm});
            skLineSegment(sketch, "E1930", {"start": v(3.14, -17.13) * mm, "end": v(3.13, -17.26) * mm});
            skLineSegment(sketch, "E1931", {"start": v(3.13, -17.26) * mm, "end": v(3.11, -17.39) * mm});
            skLineSegment(sketch, "E1932", {"start": v(3.11, -17.39) * mm, "end": v(3.08, -17.52) * mm});
            skLineSegment(sketch, "E1933", {"start": v(3.08, -17.52) * mm, "end": v(3.05, -17.64) * mm});
            skLineSegment(sketch, "E1934", {"start": v(3.05, -17.64) * mm, "end": v(3, -17.77) * mm});
            skLineSegment(sketch, "E1935", {"start": v(3, -17.77) * mm, "end": v(2.93, -17.88) * mm});
            skLineSegment(sketch, "E1936", {"start": v(2.93, -17.88) * mm, "end": v(2.85, -18) * mm});
            skLineSegment(sketch, "E1937", {"start": v(2.85, -18) * mm, "end": v(2.76, -18.09) * mm});
            skLineSegment(sketch, "E1938", {"start": v(2.76, -18.09) * mm, "end": v(2.67, -18.15) * mm});
            skLineSegment(sketch, "E1939", {"start": v(2.67, -18.15) * mm, "end": v(2.64, -18.16) * mm});
            skLineSegment(sketch, "E1940", {"start": v(2.64, -18.16) * mm, "end": v(2.63, -18.15) * mm});
            skLineSegment(sketch, "E1941", {"start": v(2.63, -18.15) * mm, "end": v(2.62, -18.08) * mm});
            skLineSegment(sketch, "E1942", {"start": v(2.62, -18.08) * mm, "end": v(2.62, -17.94) * mm});
            skLineSegment(sketch, "E1943", {"start": v(2.62, -17.94) * mm, "end": v(2.62, -17.76) * mm});
            skLineSegment(sketch, "E1944", {"start": v(2.62, -17.76) * mm, "end": v(2.62, -17.53) * mm});
            skLineSegment(sketch, "E1945", {"start": v(2.62, -17.53) * mm, "end": v(2.62, -17.27) * mm});
            skLineSegment(sketch, "E1946", {"start": v(2.62, -17.27) * mm, "end": v(2.6, -16.98) * mm});
            skLineSegment(sketch, "E1947", {"start": v(2.6, -16.98) * mm, "end": v(2.59, -16.68) * mm});
            skLineSegment(sketch, "E1948", {"start": v(2.59, -16.68) * mm, "end": v(2.55, -16.36) * mm});
            skLineSegment(sketch, "E1949", {"start": v(2.55, -16.36) * mm, "end": v(2.5, -16.04) * mm});
            skLineSegment(sketch, "E1950", {"start": v(2.5, -16.04) * mm, "end": v(2.41, -15.72) * mm});
            skLineSegment(sketch, "E1951", {"start": v(2.41, -15.72) * mm, "end": v(2.3, -15.41) * mm});
            skLineSegment(sketch, "E1952", {"start": v(2.3, -15.41) * mm, "end": v(2.16, -15.12) * mm});
            skLineSegment(sketch, "E1953", {"start": v(2.16, -15.12) * mm, "end": v(1.97, -14.86) * mm});
            skLineSegment(sketch, "E1954", {"start": v(1.97, -14.86) * mm, "end": v(1.75, -14.64) * mm});
            skLineSegment(sketch, "E1955", {"start": v(1.75, -14.64) * mm, "end": v(1.48, -14.45) * mm});
            skLineSegment(sketch, "E1956", {"start": v(1.48, -14.45) * mm, "end": v(1.24, -14.34) * mm});
            skLineSegment(sketch, "E1957", {"start": v(1.24, -14.34) * mm, "end": v(1.16, -14.31) * mm});
            skLineSegment(sketch, "E1958", {"start": v(1.16, -14.31) * mm, "end": v(1.2, -14.4) * mm});
            skLineSegment(sketch, "E1959", {"start": v(1.2, -14.4) * mm, "end": v(1.3, -14.65) * mm});
            skLineSegment(sketch, "E1960", {"start": v(1.3, -14.65) * mm, "end": v(1.42, -14.94) * mm});
            skLineSegment(sketch, "E1961", {"start": v(1.42, -14.94) * mm, "end": v(1.48, -15.17) * mm});
            skLineSegment(sketch, "E1962", {"start": v(1.48, -15.17) * mm, "end": v(1.52, -15.36) * mm});
            skLineSegment(sketch, "E1963", {"start": v(1.52, -15.36) * mm, "end": v(1.54, -15.5) * mm});
            skLineSegment(sketch, "E1964", {"start": v(1.54, -15.5) * mm, "end": v(1.54, -15.6) * mm});
            skLineSegment(sketch, "E1965", {"start": v(1.54, -15.6) * mm, "end": v(1.53, -15.65) * mm});
            skLineSegment(sketch, "E1966", {"start": v(1.53, -15.65) * mm, "end": v(1.53, -15.67) * mm});
            skLineSegment(sketch, "E1967", {"start": v(1.53, -15.67) * mm, "end": v(1.53, -15.69) * mm});
            skLineSegment(sketch, "E1968", {"start": v(1.53, -15.69) * mm, "end": v(1.52, -15.74) * mm});
            skLineSegment(sketch, "E1969", {"start": v(1.52, -15.74) * mm, "end": v(1.51, -15.82) * mm});
            skLineSegment(sketch, "E1970", {"start": v(1.51, -15.82) * mm, "end": v(1.5, -15.9) * mm});
            skLineSegment(sketch, "E1971", {"start": v(1.5, -15.9) * mm, "end": v(1.5, -15.98) * mm});
            skLineSegment(sketch, "E1972", {"start": v(1.5, -15.98) * mm, "end": v(1.48, -16.04) * mm});
            skLineSegment(sketch, "E1973", {"start": v(1.48, -16.04) * mm, "end": v(1.47, -16.06) * mm});
            skLineSegment(sketch, "E1974", {"start": v(1.47, -16.06) * mm, "end": v(1.46, -16.05) * mm});
            skLineSegment(sketch, "E1975", {"start": v(1.46, -16.05) * mm, "end": v(1.46, -16.04) * mm});
            skLineSegment(sketch, "E1976", {"start": v(1.46, -16.04) * mm, "end": v(1.45, -16) * mm});
            skLineSegment(sketch, "E1977", {"start": v(1.45, -16) * mm, "end": v(1.43, -15.86) * mm});
            skLineSegment(sketch, "E1978", {"start": v(1.43, -15.86) * mm, "end": v(1.38, -15.68) * mm});
            skLineSegment(sketch, "E1979", {"start": v(1.38, -15.68) * mm, "end": v(1.32, -15.5) * mm});
            skLineSegment(sketch, "E1980", {"start": v(1.32, -15.5) * mm, "end": v(1.24, -15.33) * mm});
            skLineSegment(sketch, "E1981", {"start": v(1.24, -15.33) * mm, "end": v(1.16, -15.17) * mm});
            skLineSegment(sketch, "E1982", {"start": v(1.16, -15.17) * mm, "end": v(1.08, -15.01) * mm});
            skLineSegment(sketch, "E1983", {"start": v(1.08, -15.01) * mm, "end": v(1, -14.86) * mm});
            skLineSegment(sketch, "E1984", {"start": v(1, -14.86) * mm, "end": v(0.9, -14.72) * mm});
            skLineSegment(sketch, "E1985", {"start": v(0.9, -14.72) * mm, "end": v(0.82, -14.6) * mm});
            skLineSegment(sketch, "E1986", {"start": v(0.82, -14.6) * mm, "end": v(0.74, -14.48) * mm});
            skLineSegment(sketch, "E1987", {"start": v(0.74, -14.48) * mm, "end": v(0.66, -14.38) * mm});
            skLineSegment(sketch, "E1988", {"start": v(0.66, -14.38) * mm, "end": v(0.6, -14.3) * mm});
            skLineSegment(sketch, "E1989", {"start": v(0.6, -14.3) * mm, "end": v(0.54, -14.23) * mm});
            skLineSegment(sketch, "E1990", {"start": v(0.54, -14.23) * mm, "end": v(0.5, -14.18) * mm});
            skLineSegment(sketch, "E1991", {"start": v(0.5, -14.18) * mm, "end": v(0.46, -14.15) * mm});
            skLineSegment(sketch, "E1992", {"start": v(0.46, -14.15) * mm, "end": v(0.46, -14.14) * mm});
            skLineSegment(sketch, "E1993", {"start": v(0.46, -14.14) * mm, "end": v(0.45, -14.13) * mm});
            skLineSegment(sketch, "E1994", {"start": v(0.45, -14.13) * mm, "end": v(0.43, -14.11) * mm});
            skLineSegment(sketch, "E1995", {"start": v(0.43, -14.11) * mm, "end": v(0.4, -14.08) * mm});
            skLineSegment(sketch, "E1996", {"start": v(0.4, -14.08) * mm, "end": v(0.38, -14.04) * mm});
            skLineSegment(sketch, "E1997", {"start": v(0.38, -14.04) * mm, "end": v(0.34, -13.98) * mm});
            skLineSegment(sketch, "E1998", {"start": v(0.34, -13.98) * mm, "end": v(0.29, -13.9) * mm});
            skLineSegment(sketch, "E1999", {"start": v(0.29, -13.9) * mm, "end": v(0.24, -13.8) * mm});
            skLineSegment(sketch, "E2000", {"start": v(0.24, -13.8) * mm, "end": v(0.18, -13.69) * mm});
            skLineSegment(sketch, "E2001", {"start": v(0.18, -13.69) * mm, "end": v(0.12, -13.55) * mm});
            skLineSegment(sketch, "E2002", {"start": v(0.12, -13.55) * mm, "end": v(0.06, -13.38) * mm});
            skLineSegment(sketch, "E2003", {"start": v(0.06, -13.38) * mm, "end": v(0, -13.19) * mm});
            skLineSegment(sketch, "E2004", {"start": v(0, -13.19) * mm, "end": v(-0.07, -12.97) * mm});
            skLineSegment(sketch, "E2005", {"start": v(-0.07, -12.97) * mm, "end": v(-0.13, -12.72) * mm});
            skLineSegment(sketch, "E2006", {"start": v(-0.13, -12.72) * mm, "end": v(-0.2, -12.45) * mm});
            skLineSegment(sketch, "E2007", {"start": v(-0.2, -12.45) * mm, "end": v(-0.25, -12.14) * mm});
            skLineSegment(sketch, "E2008", {"start": v(-0.25, -12.14) * mm, "end": v(-0.3, -11.88) * mm});
            skLineSegment(sketch, "E2009", {"start": v(-0.3, -11.88) * mm, "end": v(-0.31, -11.8) * mm});
            skSolve(sketch);
        }
        {
            var Q0;
            Q0=makeQuery(id+"F1.imprint","IMPRINT",FACE,{"disambiguationData":[TD([[makeQuery(id+"F1.imprint","IMPRINT",EDGE,{"derivedFrom":sQuery(id+"F1.wireOp",EDGE,"E170")}),1.0]])]});
            var Q1;
            Q1=makeQuery(id+"F1.imprint","IMPRINT",FACE,{"disambiguationData":[TD([[makeQuery(id+"F1.imprint","IMPRINT",EDGE,{"derivedFrom":sQuery(id+"F1.wireOp",EDGE,"E84")}),1.0]])]});
            var Q2;
            Q2=makeQuery(id+"F1.imprint","IMPRINT",FACE,{"disambiguationData":[TD([[makeQuery(id+"F1.imprint","IMPRINT",EDGE,{"derivedFrom":sQuery(id+"F1.wireOp",EDGE,"E110")}),1.0]])]});
            var Q3;
            Q3=makeQuery(id+"F1.imprint","IMPRINT",FACE,{"disambiguationData":[TD([[makeQuery(id+"F1.imprint","IMPRINT",EDGE,{"derivedFrom":sQuery(id+"F1.wireOp",EDGE,"E136")}),1.0]])]});
            var Q4;
            Q4=makeQuery(id+"F1.imprint","IMPRINT",FACE,{"disambiguationData":[TD([[makeQuery(id+"F1.imprint","IMPRINT",EDGE,{"derivedFrom":sQuery(id+"F1.wireOp",EDGE,"E58")}),1.0]])]});
            var Q5;
            Q5=makeQuery(id+"F1.imprint","IMPRINT",FACE,{"disambiguationData":[TD([[makeQuery(id+"F1.imprint","IMPRINT",EDGE,{"derivedFrom":sQuery(id+"F1.wireOp",EDGE,"E6")}),1.0]])]});
            var Q6;
            Q6=makeQuery(id+"F1.imprint","IMPRINT",FACE,{"disambiguationData":[TD([[makeQuery(id+"F1.imprint","IMPRINT",EDGE,{"derivedFrom":sQuery(id+"F1.wireOp",EDGE,"E32")}),1.0]])]});
            extrude(context, id + "F6", {"entities" : qUnion([Q0, Q1, Q2, Q3, Q4, Q5, Q6]), "depth" : 0.13 * mm, "offsetDistance" : 25.4 * mm});
        }
        {
            var Q0;
            Q0=makeQuery(id+"F2.imprint","IMPRINT",FACE,{"disambiguationData":[TD([[makeQuery(id+"F2.imprint","IMPRINT",EDGE,{"derivedFrom":sQuery(id+"F2.wireOp",EDGE,"E504")}),1.0]])]});
            var Q1;
            Q1=makeQuery(id+"F2.imprint","IMPRINT",FACE,{"disambiguationData":[TD([[makeQuery(id+"F2.imprint","IMPRINT",EDGE,{"derivedFrom":sQuery(id+"F2.wireOp",EDGE,"E450")}),1.0]])]});
            var Q2;
            Q2=makeQuery(id+"F2.imprint","IMPRINT",FACE,{"disambiguationData":[TD([[makeQuery(id+"F2.imprint","IMPRINT",EDGE,{"derivedFrom":sQuery(id+"F2.wireOp",EDGE,"E310")}),1.0]])]});
            var Q3;
            Q3=makeQuery(id+"F2.imprint","IMPRINT",FACE,{"disambiguationData":[TD([[makeQuery(id+"F2.imprint","IMPRINT",EDGE,{"derivedFrom":sQuery(id+"F2.wireOp",EDGE,"E230")}),1.0]])]});
            var Q4;
            Q4=makeQuery(id+"F2.imprint","IMPRINT",FACE,{"disambiguationData":[TD([[makeQuery(id+"F2.imprint","IMPRINT",EDGE,{"derivedFrom":sQuery(id+"F2.wireOp",EDGE,"E276")}),1.0]])]});
            var Q5;
            Q5=makeQuery(id+"F2.imprint","IMPRINT",FACE,{"disambiguationData":[TD([[makeQuery(id+"F2.imprint","IMPRINT",EDGE,{"derivedFrom":sQuery(id+"F2.wireOp",EDGE,"E398")}),1.0]])]});
            var Q6;
            Q6=makeQuery(id+"F2.imprint","IMPRINT",FACE,{"disambiguationData":[TD([[makeQuery(id+"F2.imprint","IMPRINT",EDGE,{"derivedFrom":sQuery(id+"F2.wireOp",EDGE,"E342")}),1.0]])]});
            extrude(context, id + "F7", {"entities" : qUnion([Q0, Q1, Q2, Q3, Q4, Q5, Q6]), "depth" : 0.13 * mm, "offsetDistance" : 25.4 * mm});
        }
        {
            var Q0;
            Q0=makeQuery(id+"F3.imprint","IMPRINT",FACE,{"disambiguationData":[TD([[makeQuery(id+"F3.imprint","IMPRINT",EDGE,{"derivedFrom":sQuery(id+"F3.wireOp",EDGE,"E1119")}),1.0]])]});
            var Q1;
            Q1=makeQuery(id+"F3.imprint","IMPRINT",FACE,{"disambiguationData":[TD([[makeQuery(id+"F3.imprint","IMPRINT",EDGE,{"derivedFrom":sQuery(id+"F3.wireOp",EDGE,"E1003")}),1.0]])]});
            var Q2;
            Q2=makeQuery(id+"F3.imprint","IMPRINT",FACE,{"disambiguationData":[TD([[makeQuery(id+"F3.imprint","IMPRINT",EDGE,{"derivedFrom":sQuery(id+"F3.wireOp",EDGE,"E747")}),1.0]])]});
            var Q3;
            Q3=makeQuery(id+"F3.imprint","IMPRINT",FACE,{"disambiguationData":[TD([[makeQuery(id+"F3.imprint","IMPRINT",EDGE,{"derivedFrom":sQuery(id+"F3.wireOp",EDGE,"E643")}),1.0]])]});
            var Q4;
            Q4=makeQuery(id+"F3.imprint","IMPRINT",FACE,{"disambiguationData":[TD([[makeQuery(id+"F3.imprint","IMPRINT",EDGE,{"derivedFrom":sQuery(id+"F3.wireOp",EDGE,"E801")}),1.0]])]});
            var Q5;
            Q5=makeQuery(id+"F3.imprint","IMPRINT",FACE,{"disambiguationData":[TD([[makeQuery(id+"F3.imprint","IMPRINT",EDGE,{"derivedFrom":sQuery(id+"F3.wireOp",EDGE,"E1167")}),1.0]])]});
            var Q6;
            Q6=makeQuery(id+"F3.imprint","IMPRINT",FACE,{"disambiguationData":[TD([[makeQuery(id+"F3.imprint","IMPRINT",EDGE,{"derivedFrom":sQuery(id+"F3.wireOp",EDGE,"E693")}),1.0]])]});
            var Q7;
            Q7=makeQuery(id+"F3.imprint","IMPRINT",FACE,{"disambiguationData":[TD([[makeQuery(id+"F3.imprint","IMPRINT",EDGE,{"derivedFrom":sQuery(id+"F3.wireOp",EDGE,"E579")}),1.0]])]});
            var Q8;
            Q8=makeQuery(id+"F3.imprint","IMPRINT",FACE,{"disambiguationData":[TD([[makeQuery(id+"F3.imprint","IMPRINT",EDGE,{"derivedFrom":sQuery(id+"F3.wireOp",EDGE,"E945")}),1.0]])]});
            var Q9;
            Q9=makeQuery(id+"F3.imprint","IMPRINT",FACE,{"disambiguationData":[TD([[makeQuery(id+"F3.imprint","IMPRINT",EDGE,{"derivedFrom":sQuery(id+"F3.wireOp",EDGE,"E1059")}),1.0]])]});
            var Q10;
            Q10=makeQuery(id+"F3.imprint","IMPRINT",FACE,{"disambiguationData":[TD([[makeQuery(id+"F3.imprint","IMPRINT",EDGE,{"derivedFrom":sQuery(id+"F3.wireOp",EDGE,"E1327")}),1.0]])]});
            var Q11;
            Q11=makeQuery(id+"F3.imprint","IMPRINT",FACE,{"disambiguationData":[TD([[makeQuery(id+"F3.imprint","IMPRINT",EDGE,{"derivedFrom":sQuery(id+"F3.wireOp",EDGE,"E1275")}),1.0]])]});
            var Q12;
            Q12=makeQuery(id+"F3.imprint","IMPRINT",FACE,{"disambiguationData":[TD([[makeQuery(id+"F3.imprint","IMPRINT",EDGE,{"derivedFrom":sQuery(id+"F3.wireOp",EDGE,"E1219")}),1.0]])]});
            extrude(context, id + "F8", {"entities" : qUnion([Q0, Q1, Q2, Q3, Q4, Q5, Q6, Q7, Q8, Q9, Q10, Q11, Q12]), "depth" : 0.13 * mm, "offsetDistance" : 25.4 * mm});
        }
        {
            var Q0;
            Q0=qSketchRegion(id+"F4",true);
            extrude(context, id + "F9", {"entities" : qUnion([Q0]), "depth" : 0.13 * mm, "offsetDistance" : 25.4 * mm});
        }
        {
            var Q0;
            Q0=qSketchRegion(id+"F5",true);
            extrude(context, id + "F10", {"entities" : qUnion([Q0]), "depth" : 0.13 * mm, "offsetDistance" : 25.4 * mm});
        }
    });
